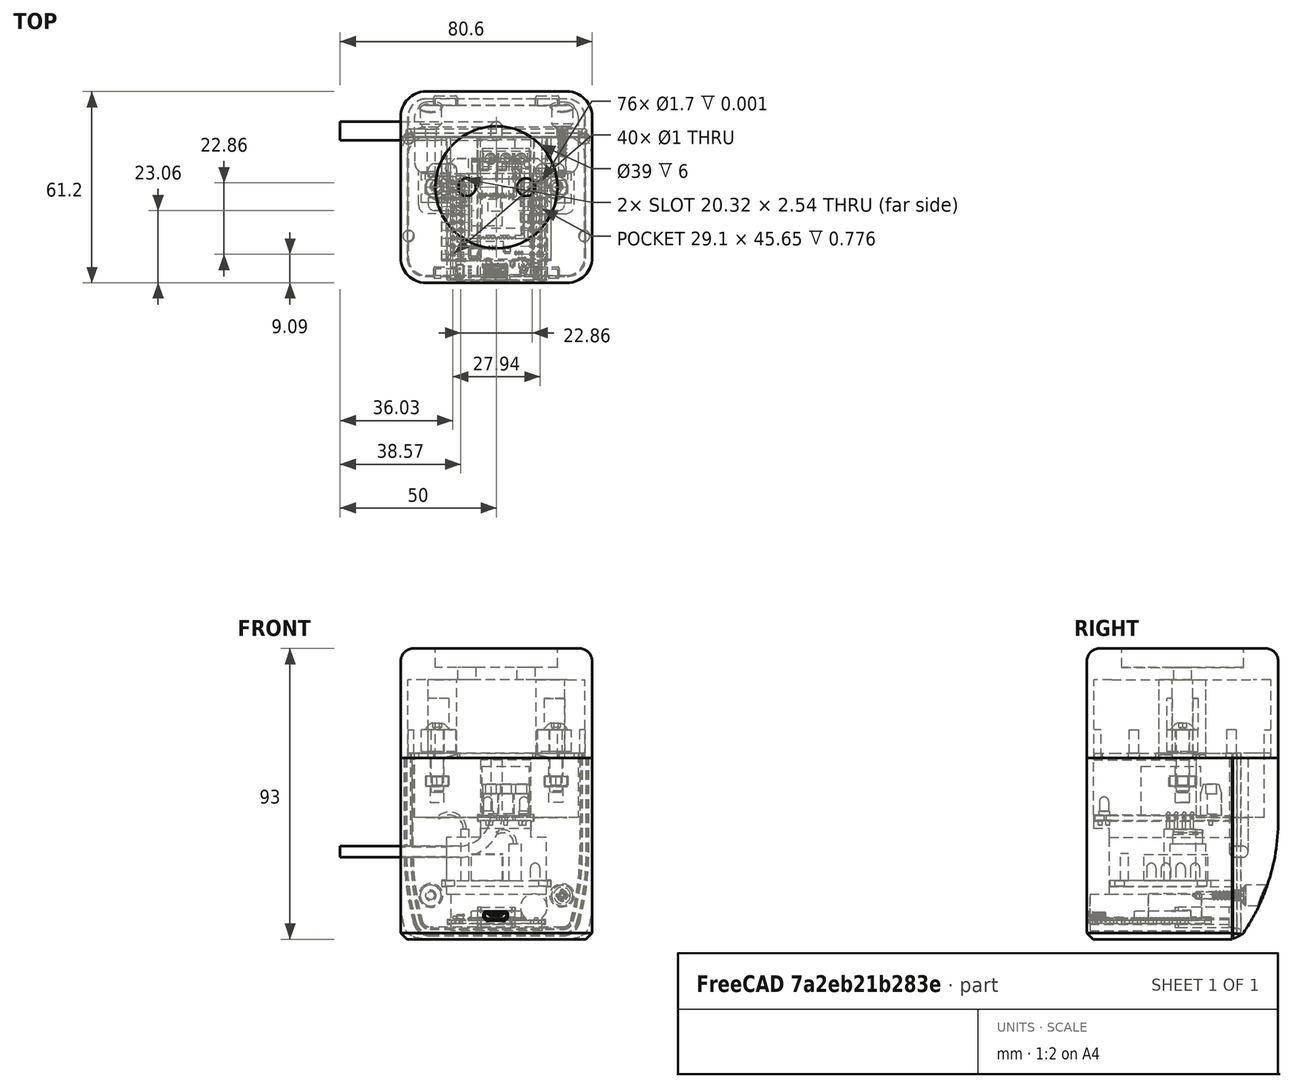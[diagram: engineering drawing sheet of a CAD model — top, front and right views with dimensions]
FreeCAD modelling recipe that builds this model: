
FCSTD DOCUMENT  (FreeCAD 1.0R39109 (Git))
Label: BedroomFan V3
License: All rights reserved
LicenseURL: http://en.wikipedia.org/wiki/All_rights_reserved
objects: Sketcher::SketchObject×80, PartDesign::SubShapeBinder×46, PartDesign::Plane×24, PartDesign::Body×22, PartDesign::Pad×19, PartDesign::Pocket×17, PartDesign::Revolution×11, PartDesign::Mirrored×6, Part::FeaturePython×4, PartDesign::Fillet×3, PartDesign::AdditivePipe×3, PartDesign::Point×3, PartDesign::Chamfer×3, PartDesign::SubtractivePipe×3, Part::Compound×2, PartDesign::Groove×2, PartDesign::LinearPattern×2, Part::MultiCommon×2, Part::Feature×1, PartDesign::MultiTransform×1, +2 more types
note: 470 computed .brp shape members not serialized (recipe doc carries the construction recipe); baked Part::Feature solids carry a one-line shape summary decoded from their .brp

FEATURE [Part::Feature] Part__Feature  label="MH-ET_LIVE_MiniKit"
  shape: bbox 31.02 x 99.68 x 39.44 mm, 5494 faces, 23 solids (baked)
FEATURE [Sketcher::SketchObject] Sketch009
  ArcFitTolerance = 0
  AttachmentSupport = -> [XY_Plane001]
  FullyConstrained = true
  MakeInternals = false
  MapMode = 5
  sketch-geometry (8):
    g0: LineSegment StartX=0 StartY=8.8 StartZ=0 EndX=43.2 EndY=8.8 EndZ=0
    g1: LineSegment StartX=43.2 StartY=8.8 StartZ=0 EndX=43.2 EndY=-8.8 EndZ=0
    g2: LineSegment StartX=43.2 StartY=-8.8 StartZ=0 EndX=0 EndY=-8.8 EndZ=0
    g3: LineSegment StartX=0 StartY=-8.8 StartZ=0 EndX=0 EndY=8.8 EndZ=0
    g4: Circle CenterX=3.2 CenterY=2.54 CenterZ=0 NormalX=0 NormalY=0 NormalZ=1 AngleXU=0 Radius=0.4
    g5: Circle CenterX=3.2 CenterY=0 CenterZ=0 NormalX=0 NormalY=0 NormalZ=1 AngleXU=0 Radius=0.4
    g6: Circle CenterX=3.2 CenterY=-2.54 CenterZ=0 NormalX=0 NormalY=0 NormalZ=1 AngleXU=0 Radius=0.4
    g7: LineSegment [constr] StartX=3.2 StartY=2.54 StartZ=0 EndX=3.2 EndY=-2.54 EndZ=0
  constraints (21):
    c: Coincident(g0,g1)
    c: Coincident(g1,g2)
    c: Coincident(g2,g3)
    c: Coincident(g3,g0)
    c: Horizontal(g0)
    c: Horizontal(g2)
    c: Vertical(g3)
    c: PointOnObject(g0,g-2)
    c: Symmetric(g1,g0,g-1)
    c: DistanceY(g1,g1) = 17.6
    c: DistanceX(g0,g0) = 43.2
    c: PointOnObject(g5,g-1)
    c: Symmetric(g6,g4,g-1)
    c: Coincident(g7,g4)
    c: Coincident(g7,g6)
    c: PointOnObject(g5,g7)
    c: Equal(g6,g5)
    c: Equal(g5,g4)
    c: Radius(g4) = 0.4
    c: DistanceY(g7,g7) = 5.08
    c: DistanceX(g4) = 3.2
FEATURE [PartDesign::Pad] Pad006
  Direction = (0,0,1)
  Length = 1.6
  Length2 = 100
  Profile = -> Sketch009
  Suppressed = false
  Type = 0
FEATURE [PartDesign::Body] Body001  label="PCB"
  AllowCompound = false
  Group = -> [Sketch009,Pad006]
  Origin = -> Origin001
  Tip = -> Pad006
FEATURE [Sketcher::SketchObject] Sketch010
  ArcFitTolerance = 0
  AttachmentOffset = pos=(0,0,1.6) rot=(0,0,1;0rad)
  AttachmentSupport = -> [XY_Plane002]
  FullyConstrained = true
  MakeInternals = false
  MapMode = 5
  Placement = pos=(0,0,1.6) rot=(0,0,1;0rad)
  sketch-geometry (4):
    g0: LineSegment StartX=14.8 StartY=7.6 StartZ=0 EndX=33.8 EndY=7.6 EndZ=0
    g1: LineSegment StartX=33.8 StartY=7.6 StartZ=0 EndX=33.8 EndY=-7.6 EndZ=0
    g2: LineSegment StartX=33.8 StartY=-7.6 StartZ=0 EndX=14.8 EndY=-7.6 EndZ=0
    g3: LineSegment StartX=14.8 StartY=-7.6 StartZ=0 EndX=14.8 EndY=7.6 EndZ=0
  constraints (11):
    c: Coincident(g0,g1)
    c: Coincident(g1,g2)
    c: Coincident(g2,g3)
    c: Coincident(g3,g0)
    c: Horizontal(g0)
    c: Horizontal(g2)
    c: Vertical(g3)
    c: Symmetric(g1,g0,g-1)
    c: DistanceX(g0,g0) = 19
    c: DistanceY(g1,g1) = 15.2
    c: DistanceX(g0) = 14.8
FEATURE [PartDesign::Pad] Pad007
  Direction = (0,0,1)
  Length = 15.7
  Length2 = 100
  Profile = -> Sketch010
  Suppressed = false
  Type = 0
FEATURE [PartDesign::Body] Body002  label="JQC-3FF-S-Z"
  AllowCompound = false
  Group = -> [Sketch010,Pad007]
  Origin = -> Origin002
  Tip = -> Pad007
FEATURE [Sketcher::SketchObject] Sketch011
  ArcFitTolerance = 0
  AttachmentSupport = -> [XZ_Plane003]
  FullyConstrained = true
  MakeInternals = false
  MapMode = 5
  Placement = pos=(0,0,0) rot=(1,0,0;1.5708rad)
  sketch-geometry (7):
    g0: LineSegment StartX=34.6 StartY=11.6 StartZ=0 EndX=39.6 EndY=11.6 EndZ=0
    g1: LineSegment StartX=40.4 StartY=8.6 StartZ=0 EndX=40.4 EndY=1.6 EndZ=0
    g2: LineSegment StartX=40.4 StartY=1.6 StartZ=0 EndX=33.8 EndY=1.6 EndZ=0
    g3: LineSegment StartX=33.8 StartY=1.6 StartZ=0 EndX=33.8 EndY=8.6 EndZ=0
    g4: LineSegment StartX=34.6 StartY=11.6 StartZ=0 EndX=33.8 EndY=8.6 EndZ=0
    g5: LineSegment StartX=39.6 StartY=11.6 StartZ=0 EndX=40.4 EndY=8.6 EndZ=0
    g6: LineSegment [constr] StartX=37.1 StartY=11.6 StartZ=0 EndX=37.1 EndY=1.6 EndZ=0
  constraints (19):
    c: Coincident(g1,g2)
    c: Coincident(g2,g3)
    c: Horizontal(g0)
    c: Vertical(g1)
    c: DistanceY(g1) = 1.6
    c: Coincident(g3,g4)
    c: Coincident(g4,g0)
    c: Coincident(g0,g5)
    c: Coincident(g1,g5)
    c: PointOnObject(g6,g0)
    c: PointOnObject(g6,g2)
    c: Symmetric(g1,g2,g6)
    c: Symmetric(g1,g3,g6)
    c: Symmetric(g0,g0,g6)
    c: DistanceX(g2) = 33.8
    c: DistanceX(g0,g0) = 5
    c: DistanceY(g1,g0) = 10
    c: DistanceY(g1,g1) = 7
    c: DistanceX(g1) = 40.4
FEATURE [PartDesign::Pad] Pad008
  Direction = (0,-1,2e-16)
  Length = 15
  Length2 = 100
  Midplane = true
  Placement = pos=(0,0,0) rot=(1,0,0;1.5708rad)
  Profile = -> Sketch011
  Suppressed = false
  Type = 0
FEATURE [Sketcher::SketchObject] Sketch012
  ArcFitTolerance = 0
  AttachmentOffset = pos=(0,0,36) rot=(0,0,1;0rad)
  AttachmentSupport = -> [YZ_Plane003]
  FullyConstrained = true
  MakeInternals = false
  MapMode = 5
  Placement = pos=(36,0,0) rot=(0.57735,0.57735,0.57735;2.0944rad)
  sketch-geometry (16):
    g0: LineSegment StartX=-7.05 StartY=8.6 StartZ=0 EndX=-2.65 EndY=8.6 EndZ=0
    g1: LineSegment StartX=-2.65 StartY=8.6 StartZ=0 EndX=-2.65 EndY=2.1 EndZ=0
    g2: LineSegment StartX=-2.65 StartY=2.1 StartZ=0 EndX=-7.05 EndY=2.1 EndZ=0
    g3: LineSegment StartX=-7.05 StartY=2.1 StartZ=0 EndX=-7.05 EndY=8.6 EndZ=0
    g4: LineSegment [constr] StartX=-7.05 StartY=8.6 StartZ=0 EndX=-7.5 EndY=8.6 EndZ=0
    g5: LineSegment [constr] StartX=-2.2 StartY=8.6 StartZ=0 EndX=-2.65 EndY=8.6 EndZ=0
    g6: LineSegment StartX=-2.2 StartY=8.6 StartZ=0 EndX=2.2 EndY=8.6 EndZ=0
    g7: LineSegment StartX=2.2 StartY=8.6 StartZ=0 EndX=2.2 EndY=2.1 EndZ=0
    g8: LineSegment StartX=2.2 StartY=2.1 StartZ=0 EndX=-2.2 EndY=2.1 EndZ=0
    g9: LineSegment StartX=-2.2 StartY=2.1 StartZ=0 EndX=-2.2 EndY=8.6 EndZ=0
    g10: LineSegment StartX=2.65 StartY=8.6 StartZ=0 EndX=7.05 EndY=8.6 EndZ=0
    g11: LineSegment StartX=7.05 StartY=8.6 StartZ=0 EndX=7.05 EndY=2.1 EndZ=0
    g12: LineSegment StartX=7.05 StartY=2.1 StartZ=0 EndX=2.65 EndY=2.1 EndZ=0
    g13: LineSegment StartX=2.65 StartY=2.1 StartZ=0 EndX=2.65 EndY=8.6 EndZ=0
    g14: LineSegment [constr] StartX=2.65 StartY=8.6 StartZ=0 EndX=2.2 EndY=8.6 EndZ=0
    g15: LineSegment [constr] StartX=7.05 StartY=8.6 StartZ=0 EndX=7.5 EndY=8.6 EndZ=0
  constraints (45):
    c: Coincident(g0,g1)
    c: Coincident(g1,g2)
    c: Coincident(g2,g3)
    c: Coincident(g3,g0)
    c: Horizontal(g0)
    c: Horizontal(g2)
    c: Vertical(g1)
    c: Vertical(g3)
    c: DistanceX(g0,g0) = 4.4
    c: DistanceY(g0) = 8.6
    c: DistanceY(g3,g3) = 6.5
    c: Coincident(g4,g0)
    c: Horizontal(g4)
    c: Coincident(g5,g0)
    c: Equal(g5,g4)
    c: Horizontal(g5)
    c: Coincident(g6,g7)
    c: Coincident(g7,g8)
    c: Coincident(g8,g9)
    c: Coincident(g9,g6)
    c: Horizontal(g6)
    c: Horizontal(g8)
    c: Vertical(g7)
    c: Vertical(g9)
    c: Coincident(g6,g5)
    c: Coincident(g10,g11)
    c: Coincident(g11,g12)
    c: Coincident(g12,g13)
    c: Coincident(g13,g10)
    c: Horizontal(g10)
    c: Horizontal(g12)
    c: Vertical(g11)
    c: Vertical(g13)
    c: Coincident(g14,g10)
    c: Coincident(g14,g6)
    c: Horizontal(g14)
    c: Coincident(g15,g10)
    c: Equal(g15,g14)
    c: Equal(g14,g5)
    c: DistanceX(g4,g15) = 15
    c: Equal(g0,g6)
    c: Equal(g6,g10)
    c: Symmetric(g4,g15,g-2)
    c: Equal(g1,g9)
    c: Equal(g9,g13)
FEATURE [PartDesign::Pocket] Pocket
  BaseFeature = -> Pad008
  Direction = (-1,0,0)
  Length = 5
  Length2 = 100
  Placement = pos=(0,0,0) rot=(1,0,0;1.5708rad)
  Profile = -> Sketch012
  Reversed = true
  Suppressed = false
  Type = 1
FEATURE [Sketcher::SketchObject] Sketch013
  ArcFitTolerance = 0
  AttachmentOffset = pos=(0,0,8.6) rot=(0,0,1;0rad)
  AttachmentSupport = -> [XY_Plane003]
  ExternalGeometry = -> [Pocket]
  FullyConstrained = true
  MakeInternals = false
  MapMode = 5
  Placement = pos=(0,0,8.6) rot=(0,0,1;0rad)
  sketch-geometry (5):
    g0: Circle CenterX=37.1 CenterY=-4.85 CenterZ=0 NormalX=0 NormalY=0 NormalZ=1 AngleXU=0 Radius=1.75
    g1: LineSegment [constr] StartX=37.1 StartY=-2.65 StartZ=0 EndX=37.1 EndY=-7.05 EndZ=0
    g2: LineSegment [constr] StartX=38.85 StartY=-4.85 StartZ=0 EndX=35.35 EndY=-4.85 EndZ=0
    g3: Circle CenterX=37.1 CenterY=4.85 CenterZ=0 NormalX=0 NormalY=0 NormalZ=1 AngleXU=0 Radius=1.75
    g4: Circle CenterX=37.1 CenterY=0 CenterZ=0 NormalX=0 NormalY=0 NormalZ=1 AngleXU=0 Radius=1.75
  constraints (14):
    c: PointOnObject(g1,g-3)
    c: PointOnObject(g1,g-4)
    c: PointOnObject(g2,g0)
    c: PointOnObject(g2,g0)
    c: PointOnObject(g0,g1)
    c: PointOnObject(g0,g2)
    c: Symmetric(g-3,g-4,g2)
    c: Radius(g0) = 1.75
    c: Symmetric(g-5,g-6,g1)
    c: PointOnObject(g4,g-1)
    c: Symmetric(g3,g0,g-1)
    c: PointOnObject(g4,g1)
    c: Equal(g0,g4)
    c: Equal(g4,g3)
FEATURE [PartDesign::Pocket] Pocket001
  BaseFeature = -> Pocket
  Direction = (0,0,-1)
  Length = 5
  Length2 = 100
  Placement = pos=(0,0,0) rot=(1,0,0;1.5708rad)
  Profile = -> Sketch013
  Reversed = true
  Suppressed = false
  Type = 1
FEATURE [PartDesign::Body] Body003  label="Connectors"
  AllowCompound = false
  Group = -> [Sketch011,Pad008,Sketch012,Pocket,Sketch013,Pocket001]
  Origin = -> Origin003
  Tip = -> Pocket001
FEATURE [Sketcher::SketchObject] Sketch014
  ArcFitTolerance = 0
  AttachmentOffset = pos=(0,0,2.9) rot=(0,0,1;0rad)
  AttachmentSupport = -> [YZ_Plane004]
  FullyConstrained = true
  MakeInternals = false
  MapMode = 5
  Placement = pos=(2.9,0,0) rot=(0.57735,0.57735,0.57735;2.0944rad)
  sketch-geometry (6):
    g0: ArcOfCircle CenterX=0 CenterY=6.05 CenterZ=0 NormalX=0 NormalY=0 NormalZ=1 AngleXU=0 Radius=1.45 StartAngle=1.5708 EndAngle=3.14159
    g1: LineSegment StartX=-1.45 StartY=6.05 StartZ=0 EndX=-1.45 EndY=3 EndZ=0
    g2: LineSegment StartX=-1.45 StartY=3 StartZ=0 EndX=-1.75 EndY=3 EndZ=0
    g3: LineSegment StartX=-1.75 StartY=3 StartZ=0 EndX=-1.75 EndY=1.6 EndZ=0
    g4: LineSegment StartX=-1.75 StartY=1.6 StartZ=0 EndX=0 EndY=1.6 EndZ=0
    g5: LineSegment StartX=0 StartY=1.6 StartZ=0 EndX=0 EndY=7.5 EndZ=0
  constraints (18):
    c: Vertical(g1)
    c: Coincident(g1,g2)
    c: Coincident(g2,g3)
    c: Coincident(g3,g4)
    c: Horizontal(g4)
    c: Coincident(g4,g5)
    c: Coincident(g5,g0)
    c: Vertical(g5)
    c: Tangent(g0,g1) = -1.5708
    c: PointOnObject(g0,g5)
    c: Horizontal(g2)
    c: Vertical(g3)
    c: DistanceY(g3) = 1.6
    c: DistanceY(g0) = 7.5
    c: DistanceX(g0,g0) = 1.45
    c: DistanceX(g4,g4) = 1.75
    c: DistanceY(g2) = 3
    c: PointOnObject(g4,g-2)
FEATURE [PartDesign::Revolution] Revolution001
  Angle = 360
  Angle2 = 60
  Axis = (0,0,1)
  Base = (2.9,0,0)
  Placement = pos=(0,0,0) rot=(0.57735,0.57735,0.57735;2.0944rad)
  Profile = -> Sketch014
  ReferenceAxis = -> Sketch014 [V_Axis]
  Suppressed = false
  Type = 0
FEATURE [PartDesign::Body] Body004  label="LEDgreen"
  AllowCompound = false
  Group = -> [Sketch014,Revolution001]
  Origin = -> Origin004
  Placement = pos=(0,5.8,0) rot=(0,0,1;0rad)
  Tip = -> Revolution001
FEATURE [Sketcher::SketchObject] Sketch015
  ArcFitTolerance = 0
  AttachmentOffset = pos=(0,0,2.9) rot=(0,0,1;0rad)
  AttachmentSupport = -> [YZ_Plane004]
  FullyConstrained = true
  MakeInternals = false
  MapMode = 5
  Placement = pos=(2.9,0,0) rot=(0.57735,0.57735,0.57735;2.0944rad)
  sketch-geometry (6):
    g0: ArcOfCircle CenterX=0 CenterY=6.05 CenterZ=0 NormalX=0 NormalY=0 NormalZ=1 AngleXU=0 Radius=1.45 StartAngle=1.5708 EndAngle=3.14159
    g1: LineSegment StartX=-1.45 StartY=6.05 StartZ=0 EndX=-1.45 EndY=3 EndZ=0
    g2: LineSegment StartX=-1.45 StartY=3 StartZ=0 EndX=-1.75 EndY=3 EndZ=0
    g3: LineSegment StartX=-1.75 StartY=3 StartZ=0 EndX=-1.75 EndY=1.6 EndZ=0
    g4: LineSegment StartX=-1.75 StartY=1.6 StartZ=0 EndX=0 EndY=1.6 EndZ=0
    g5: LineSegment StartX=1e-16 StartY=1.6 StartZ=0 EndX=1e-16 EndY=7.5 EndZ=0
  constraints (18):
    c: Vertical(g1)
    c: Coincident(g1,g2)
    c: Coincident(g2,g3)
    c: Coincident(g3,g4)
    c: Horizontal(g4)
    c: Coincident(g4,g5)
    c: Coincident(g5,g0)
    c: Vertical(g5)
    c: Tangent(g0,g1) = -1.5708
    c: PointOnObject(g0,g5)
    c: Horizontal(g2)
    c: Vertical(g3)
    c: DistanceY(g3) = 1.6
    c: DistanceY(g0) = 7.5
    c: DistanceX(g0,g0) = 1.45
    c: DistanceX(g4,g4) = 1.75
    c: DistanceY(g2) = 3
    c: PointOnObject(g4,g-2)
FEATURE [PartDesign::Revolution] Revolution002
  Angle = 360
  Angle2 = 60
  Axis = (0,0,1)
  Base = (2.9,0,0)
  Placement = pos=(0,0,0) rot=(0.57735,0.57735,0.57735;2.0944rad)
  Profile = -> Sketch015
  ReferenceAxis = -> Sketch015 [V_Axis]
  Suppressed = false
  Type = 0
FEATURE [PartDesign::Body] Body005  label="LEDred"
  AllowCompound = false
  Group = -> [Sketch015,Revolution002]
  Origin = -> Origin005
  Placement = pos=(0,-5.8,0) rot=(0,0,1;0rad)
  Tip = -> Revolution002
FEATURE [Sketcher::SketchObject] Sketch016
  ArcFitTolerance = 0
  AttachmentSupport = -> [YZ_Plane006]
  FullyConstrained = true
  MakeInternals = false
  MapMode = 5
  Placement = pos=(0,0,0) rot=(0.57735,0.57735,0.57735;2.0944rad)
  sketch-geometry (5):
    g0: LineSegment StartX=1.2 StartY=0 StartZ=0 EndX=0 EndY=0 EndZ=0
    g1: LineSegment StartX=0 StartY=0 StartZ=0 EndX=0 EndY=-1.5 EndZ=0
    g2: LineSegment StartX=0 StartY=-1.5 StartZ=0 EndX=0.6 EndY=-1.5 EndZ=0
    g3: LineSegment StartX=0.6 StartY=-1.5 StartZ=0 EndX=0.6 EndY=-0.6 EndZ=0
    g4: ArcOfCircle CenterX=1.2 CenterY=-0.6 CenterZ=0 NormalX=0 NormalY=0 NormalZ=1 AngleXU=0 Radius=0.6 StartAngle=1.5708 EndAngle=3.14159
  constraints (13):
    c: PointOnObject(g0,g-1)
    c: Coincident(g0,g-1)
    c: Coincident(g0,g1)
    c: PointOnObject(g1,g-2)
    c: Coincident(g1,g2)
    c: Horizontal(g2)
    c: Coincident(g2,g3)
    c: Vertical(g3)
    c: Tangent(g0,g4) = -1.5708
    c: Tangent(g3,g4) = 1.5708
    c: DistanceX(g2,g2) = 0.6
    c: DistanceY(g1,g1) = 1.5
    c: Radius(g4) = 0.6
FEATURE [PartDesign::Revolution] Revolution003
  Angle = 360
  Angle2 = 60
  Axis = (0,0,1)
  Base = (0,0,0)
  Placement = pos=(0,0,0) rot=(0.57735,0.57735,0.57735;2.0944rad)
  Profile = -> Sketch016
  ReferenceAxis = -> Sketch016 [V_Axis]
  Reversed = true
  Suppressed = false
  Type = 0
FEATURE [PartDesign::Body] Body006  label="Pin001"
  AllowCompound = false
  Group = -> [Sketch016,Revolution003]
  Origin = -> Origin006
  Placement = pos=(1.7,5.7,0) rot=(0,0,1;0rad)
  Tip = -> Revolution003
FEATURE [Sketcher::SketchObject] Sketch017
  ArcFitTolerance = 0
  AttachmentSupport = -> [YZ_Plane006]
  FullyConstrained = true
  MakeInternals = false
  MapMode = 5
  Placement = pos=(0,0,0) rot=(0.57735,0.57735,0.57735;2.0944rad)
  sketch-geometry (5):
    g0: LineSegment StartX=1.2 StartY=0 StartZ=0 EndX=0 EndY=0 EndZ=0
    g1: LineSegment StartX=0 StartY=0 StartZ=0 EndX=0 EndY=-1.5 EndZ=0
    g2: LineSegment StartX=0 StartY=-1.5 StartZ=0 EndX=0.6 EndY=-1.5 EndZ=0
    g3: LineSegment StartX=0.6 StartY=-1.5 StartZ=0 EndX=0.6 EndY=-0.6 EndZ=0
    g4: ArcOfCircle CenterX=1.2 CenterY=-0.6 CenterZ=0 NormalX=0 NormalY=0 NormalZ=1 AngleXU=0 Radius=0.6 StartAngle=1.5708 EndAngle=3.14159
  constraints (13):
    c: PointOnObject(g0,g-1)
    c: Coincident(g0,g-1)
    c: Coincident(g0,g1)
    c: PointOnObject(g1,g-2)
    c: Coincident(g1,g2)
    c: Horizontal(g2)
    c: Coincident(g2,g3)
    c: Vertical(g3)
    c: Tangent(g0,g4) = -1.5708
    c: Tangent(g3,g4) = 1.5708
    c: DistanceX(g2,g2) = 0.6
    c: DistanceY(g1,g1) = 1.5
    c: Radius(g4) = 0.6
FEATURE [PartDesign::Revolution] Revolution004
  Angle = 360
  Angle2 = 60
  Axis = (0,0,1)
  Base = (0,0,0)
  Placement = pos=(0,0,0) rot=(0.57735,0.57735,0.57735;2.0944rad)
  Profile = -> Sketch017
  ReferenceAxis = -> Sketch017 [V_Axis]
  Reversed = true
  Suppressed = false
  Type = 0
FEATURE [PartDesign::Body] Body007  label="Pin002"
  AllowCompound = false
  Group = -> [Sketch017,Revolution004]
  Origin = -> Origin007
  Placement = pos=(4.1,5.7,0) rot=(0,0,1;0rad)
  Tip = -> Revolution004
FEATURE [Sketcher::SketchObject] Sketch018
  ArcFitTolerance = 0
  AttachmentSupport = -> [YZ_Plane006]
  FullyConstrained = true
  MakeInternals = false
  MapMode = 5
  Placement = pos=(0,0,0) rot=(0.57735,0.57735,0.57735;2.0944rad)
  sketch-geometry (5):
    g0: LineSegment StartX=1.2 StartY=0 StartZ=0 EndX=0 EndY=0 EndZ=0
    g1: LineSegment StartX=0 StartY=0 StartZ=0 EndX=0 EndY=-1.5 EndZ=0
    g2: LineSegment StartX=0 StartY=-1.5 StartZ=0 EndX=0.6 EndY=-1.5 EndZ=0
    g3: LineSegment StartX=0.6 StartY=-1.5 StartZ=0 EndX=0.6 EndY=-0.6 EndZ=0
    g4: ArcOfCircle CenterX=1.2 CenterY=-0.6 CenterZ=0 NormalX=0 NormalY=0 NormalZ=1 AngleXU=0 Radius=0.6 StartAngle=1.5708 EndAngle=3.14159
  constraints (13):
    c: PointOnObject(g0,g-1)
    c: Coincident(g0,g-1)
    c: Coincident(g0,g1)
    c: PointOnObject(g1,g-2)
    c: Coincident(g1,g2)
    c: Horizontal(g2)
    c: Coincident(g2,g3)
    c: Vertical(g3)
    c: Tangent(g0,g4) = -1.5708
    c: Tangent(g3,g4) = 1.5708
    c: DistanceX(g2,g2) = 0.6
    c: DistanceY(g1,g1) = 1.5
    c: Radius(g4) = 0.6
FEATURE [PartDesign::Revolution] Revolution005
  Angle = 360
  Angle2 = 60
  Axis = (0,0,1)
  Base = (0,0,0)
  Placement = pos=(0,0,0) rot=(0.57735,0.57735,0.57735;2.0944rad)
  Profile = -> Sketch018
  ReferenceAxis = -> Sketch018 [V_Axis]
  Reversed = true
  Suppressed = false
  Type = 0
FEATURE [PartDesign::Body] Body008  label="Pin003"
  AllowCompound = false
  Group = -> [Sketch018,Revolution005]
  Origin = -> Origin008
  Placement = pos=(4.1,-5.9,0) rot=(0,0,1;0rad)
  Tip = -> Revolution005
FEATURE [Sketcher::SketchObject] Sketch019
  ArcFitTolerance = 0
  AttachmentSupport = -> [YZ_Plane006]
  FullyConstrained = true
  MakeInternals = false
  MapMode = 5
  Placement = pos=(0,0,0) rot=(0.57735,0.57735,0.57735;2.0944rad)
  sketch-geometry (5):
    g0: LineSegment StartX=1.2 StartY=0 StartZ=0 EndX=0 EndY=0 EndZ=0
    g1: LineSegment StartX=0 StartY=0 StartZ=0 EndX=0 EndY=-1.5 EndZ=0
    g2: LineSegment StartX=0 StartY=-1.5 StartZ=0 EndX=0.6 EndY=-1.5 EndZ=0
    g3: LineSegment StartX=0.6 StartY=-1.5 StartZ=0 EndX=0.6 EndY=-0.6 EndZ=0
    g4: ArcOfCircle CenterX=1.2 CenterY=-0.6 CenterZ=0 NormalX=0 NormalY=0 NormalZ=1 AngleXU=0 Radius=0.6 StartAngle=1.5708 EndAngle=3.14159
  constraints (13):
    c: PointOnObject(g0,g-1)
    c: Coincident(g0,g-1)
    c: Coincident(g0,g1)
    c: PointOnObject(g1,g-2)
    c: Coincident(g1,g2)
    c: Horizontal(g2)
    c: Coincident(g2,g3)
    c: Vertical(g3)
    c: Tangent(g0,g4) = -1.5708
    c: Tangent(g3,g4) = 1.5708
    c: DistanceX(g2,g2) = 0.6
    c: DistanceY(g1,g1) = 1.5
    c: Radius(g4) = 0.6
FEATURE [PartDesign::Revolution] Revolution006
  Angle = 360
  Angle2 = 60
  Axis = (0,0,1)
  Base = (0,0,0)
  Placement = pos=(0,0,0) rot=(0.57735,0.57735,0.57735;2.0944rad)
  Profile = -> Sketch019
  ReferenceAxis = -> Sketch019 [V_Axis]
  Reversed = true
  Suppressed = false
  Type = 0
FEATURE [PartDesign::Body] Body009  label="Pin004"
  AllowCompound = false
  Group = -> [Sketch019,Revolution006]
  Origin = -> Origin009
  Placement = pos=(1.7,-5.9,0) rot=(0,0,1;0rad)
  Tip = -> Revolution006
FEATURE [Sketcher::SketchObject] Sketch020
  ArcFitTolerance = 0
  AttachmentSupport = -> [YZ_Plane006]
  FullyConstrained = true
  MakeInternals = false
  MapMode = 5
  Placement = pos=(0,0,0) rot=(0.57735,0.57735,0.57735;2.0944rad)
  sketch-geometry (5):
    g0: LineSegment StartX=1.2 StartY=0 StartZ=0 EndX=0 EndY=0 EndZ=0
    g1: LineSegment StartX=0 StartY=0 StartZ=0 EndX=0 EndY=-1.5 EndZ=0
    g2: LineSegment StartX=0 StartY=-1.5 StartZ=0 EndX=0.6 EndY=-1.5 EndZ=0
    g3: LineSegment StartX=0.6 StartY=-1.5 StartZ=0 EndX=0.6 EndY=-0.6 EndZ=0
    g4: ArcOfCircle CenterX=1.2 CenterY=-0.6 CenterZ=0 NormalX=0 NormalY=0 NormalZ=1 AngleXU=0 Radius=0.6 StartAngle=1.5708 EndAngle=3.14159
  constraints (13):
    c: PointOnObject(g0,g-1)
    c: Coincident(g0,g-1)
    c: Coincident(g0,g1)
    c: PointOnObject(g1,g-2)
    c: Coincident(g1,g2)
    c: Horizontal(g2)
    c: Coincident(g2,g3)
    c: Vertical(g3)
    c: Tangent(g0,g4) = -1.5708
    c: Tangent(g3,g4) = 1.5708
    c: DistanceX(g2,g2) = 0.6
    c: DistanceY(g1,g1) = 1.5
    c: Radius(g4) = 0.6
FEATURE [PartDesign::Revolution] Revolution007
  Angle = 360
  Angle2 = 60
  Axis = (0,0,1)
  Base = (0,0,0)
  Placement = pos=(0,0,0) rot=(0.57735,0.57735,0.57735;2.0944rad)
  Profile = -> Sketch020
  ReferenceAxis = -> Sketch020 [V_Axis]
  Reversed = true
  Suppressed = false
  Type = 0
FEATURE [PartDesign::Body] Body010  label="Pin005"
  AllowCompound = false
  Group = -> [Sketch020,Revolution007]
  Origin = -> Origin010
  Placement = pos=(37.1,-4.8,0) rot=(0,0,1;0rad)
  Tip = -> Revolution007
FEATURE [Sketcher::SketchObject] Sketch021
  ArcFitTolerance = 0
  AttachmentSupport = -> [YZ_Plane006]
  FullyConstrained = true
  MakeInternals = false
  MapMode = 5
  Placement = pos=(0,0,0) rot=(0.57735,0.57735,0.57735;2.0944rad)
  sketch-geometry (5):
    g0: LineSegment StartX=1.2 StartY=0 StartZ=0 EndX=0 EndY=0 EndZ=0
    g1: LineSegment StartX=0 StartY=0 StartZ=0 EndX=0 EndY=-1.5 EndZ=0
    g2: LineSegment StartX=0 StartY=-1.5 StartZ=0 EndX=0.6 EndY=-1.5 EndZ=0
    g3: LineSegment StartX=0.6 StartY=-1.5 StartZ=0 EndX=0.6 EndY=-0.6 EndZ=0
    g4: ArcOfCircle CenterX=1.2 CenterY=-0.6 CenterZ=0 NormalX=0 NormalY=0 NormalZ=1 AngleXU=0 Radius=0.6 StartAngle=1.5708 EndAngle=3.14159
  constraints (13):
    c: PointOnObject(g0,g-1)
    c: Coincident(g0,g-1)
    c: Coincident(g0,g1)
    c: PointOnObject(g1,g-2)
    c: Coincident(g1,g2)
    c: Horizontal(g2)
    c: Coincident(g2,g3)
    c: Vertical(g3)
    c: Tangent(g0,g4) = -1.5708
    c: Tangent(g3,g4) = 1.5708
    c: DistanceX(g2,g2) = 0.6
    c: DistanceY(g1,g1) = 1.5
    c: Radius(g4) = 0.6
FEATURE [PartDesign::Revolution] Revolution008
  Angle = 360
  Angle2 = 60
  Axis = (0,0,1)
  Base = (0,0,0)
  Placement = pos=(0,0,0) rot=(0.57735,0.57735,0.57735;2.0944rad)
  Profile = -> Sketch021
  ReferenceAxis = -> Sketch021 [V_Axis]
  Reversed = true
  Suppressed = false
  Type = 0
FEATURE [PartDesign::Body] Body011  label="Pin006"
  AllowCompound = false
  Group = -> [Sketch021,Revolution008]
  Origin = -> Origin011
  Placement = pos=(37.1,9e-16,0) rot=(0,0,1;0rad)
  Tip = -> Revolution008
FEATURE [Sketcher::SketchObject] Sketch022
  ArcFitTolerance = 0
  AttachmentSupport = -> [YZ_Plane006]
  FullyConstrained = true
  MakeInternals = false
  MapMode = 5
  Placement = pos=(0,0,0) rot=(0.57735,0.57735,0.57735;2.0944rad)
  sketch-geometry (5):
    g0: LineSegment StartX=1.2 StartY=0 StartZ=0 EndX=0 EndY=0 EndZ=0
    g1: LineSegment StartX=0 StartY=0 StartZ=0 EndX=0 EndY=-1.5 EndZ=0
    g2: LineSegment StartX=0 StartY=-1.5 StartZ=0 EndX=0.6 EndY=-1.5 EndZ=0
    g3: LineSegment StartX=0.6 StartY=-1.5 StartZ=0 EndX=0.6 EndY=-0.6 EndZ=0
    g4: ArcOfCircle CenterX=1.2 CenterY=-0.6 CenterZ=0 NormalX=0 NormalY=0 NormalZ=1 AngleXU=0 Radius=0.6 StartAngle=1.5708 EndAngle=3.14159
  constraints (13):
    c: PointOnObject(g0,g-1)
    c: Coincident(g0,g-1)
    c: Coincident(g0,g1)
    c: PointOnObject(g1,g-2)
    c: Coincident(g1,g2)
    c: Horizontal(g2)
    c: Coincident(g2,g3)
    c: Vertical(g3)
    c: Tangent(g0,g4) = -1.5708
    c: Tangent(g3,g4) = 1.5708
    c: DistanceX(g2,g2) = 0.6
    c: DistanceY(g1,g1) = 1.5
    c: Radius(g4) = 0.6
FEATURE [PartDesign::Revolution] Revolution009
  Angle = 360
  Angle2 = 60
  Axis = (0,0,1)
  Base = (0,0,0)
  Placement = pos=(0,0,0) rot=(0.57735,0.57735,0.57735;2.0944rad)
  Profile = -> Sketch022
  ReferenceAxis = -> Sketch022 [V_Axis]
  Reversed = true
  Suppressed = false
  Type = 0
FEATURE [PartDesign::Body] Body012  label="Pin007"
  AllowCompound = false
  Group = -> [Sketch022,Revolution009]
  Origin = -> Origin012
  Placement = pos=(37.1,4.8,0) rot=(0,0,1;0rad)
  Tip = -> Revolution009
FEATURE [Part::Compound] Compound  label="Relay JQC-3FF-S-Z"
  Links = -> [Body001,Body002,Body003,Body004,Body005,Body006,Body007,Body008,Body009,Body010,Body011,Body012]
  Placement = pos=(3,-28,-20) rot=(0,0,1;1.5708rad)
FEATURE [Sketcher::SketchObject] Sketch023
  ArcFitTolerance = 0
  AttachmentSupport = -> [XY_Plane013]
  FullyConstrained = true
  MakeInternals = false
  MapMode = 5
  sketch-geometry (12):
    g0: LineSegment StartX=-22.6 StartY=30.6 StartZ=0 EndX=22.6 EndY=30.6 EndZ=0
    g1: LineSegment StartX=30.6 StartY=22.6 StartZ=0 EndX=30.6 EndY=-22.6 EndZ=0
    g2: LineSegment StartX=22.6 StartY=-30.6 StartZ=0 EndX=-22.6 EndY=-30.6 EndZ=0
    g3: LineSegment StartX=-30.6 StartY=-22.6 StartZ=0 EndX=-30.6 EndY=22.6 EndZ=0
    g4: ArcOfCircle CenterX=-22.6 CenterY=22.6 CenterZ=0 NormalX=0 NormalY=0 NormalZ=1 AngleXU=0 Radius=8 StartAngle=1.5708 EndAngle=3.14159
    g5: ArcOfCircle CenterX=22.6 CenterY=22.6 CenterZ=0 NormalX=0 NormalY=0 NormalZ=1 AngleXU=0 Radius=8 StartAngle=2.39e-14 EndAngle=1.5708
    g6: ArcOfCircle CenterX=22.6 CenterY=-22.6 CenterZ=0 NormalX=0 NormalY=0 NormalZ=1 AngleXU=0 Radius=8 StartAngle=4.71239 EndAngle=6.28319
    g7: ArcOfCircle CenterX=-22.6 CenterY=-22.6 CenterZ=0 NormalX=0 NormalY=0 NormalZ=1 AngleXU=0 Radius=8 StartAngle=3.14159 EndAngle=4.71239
    g8: LineSegment [constr] StartX=-22.6 StartY=22.6 StartZ=0 EndX=22.6 EndY=22.6 EndZ=0
    g9: LineSegment [constr] StartX=22.6 StartY=22.6 StartZ=0 EndX=22.6 EndY=-22.6 EndZ=0
    g10: LineSegment [constr] StartX=22.6 StartY=-22.6 StartZ=0 EndX=-22.6 EndY=-22.6 EndZ=0
    g11: LineSegment [constr] StartX=-22.6 StartY=-22.6 StartZ=0 EndX=-22.6 EndY=22.6 EndZ=0
  constraints (26):
    c: Horizontal(g0)
    c: Horizontal(g2)
    c: Vertical(g1)
    c: Vertical(g3)
    c: Tangent(g3,g4) = 1.5708
    c: Tangent(g0,g4) = 1.5708
    c: Tangent(g0,g5) = 1.5708
    c: Tangent(g1,g5) = 1.5708
    c: Tangent(g1,g6) = 1.5708
    c: Tangent(g2,g6) = 1.5708
    c: Tangent(g2,g7) = 1.5708
    c: Tangent(g3,g7) = 1.5708
    c: Coincident(g8,g9)
    c: Coincident(g9,g10)
    c: Coincident(g10,g11)
    c: Coincident(g11,g8)
    c: Horizontal(g10)
    c: Coincident(g8,g4)
    c: Coincident(g9,g6)
    c: Coincident(g5,g8)
    c: Coincident(g7,g10)
    c: Symmetric(g5,g6,g-1)
    c: Symmetric(g5,g4,g-2)
    c: Equal(g9,g8)
    c: DistanceX(g3,g1) = 61.2
    c: Radius(g5) = 8
FEATURE [PartDesign::Pad] Pad009
  Direction = (0,0,1)
  Length = 35
  Length2 = 100
  Profile = -> Sketch023
  Suppressed = false
  Type = 0
FEATURE [Sketcher::SketchObject] Sketch024
  ArcFitTolerance = 0
  AttachmentSupport = -> [XY_Plane013]
  ExternalGeometry = -> [Sketch023]
  FullyConstrained = true
  MakeInternals = false
  MapMode = 5
  sketch-geometry (12):
    g0: LineSegment [constr] StartX=22.6 StartY=22.6 StartZ=0 EndX=-22.6 EndY=22.6 EndZ=0
    g1: LineSegment [constr] StartX=-22.6 StartY=22.6 StartZ=0 EndX=-22.6 EndY=-22.6 EndZ=0
    g2: LineSegment [constr] StartX=-22.6 StartY=-22.6 StartZ=0 EndX=22.6 EndY=-22.6 EndZ=0
    g3: LineSegment [constr] StartX=22.6 StartY=-22.6 StartZ=0 EndX=22.6 EndY=22.6 EndZ=0
    g4: LineSegment StartX=-22.6 StartY=28.3 StartZ=0 EndX=22.6 EndY=28.3 EndZ=0
    g5: LineSegment StartX=28.3 StartY=22.6 StartZ=0 EndX=28.3 EndY=-22.6 EndZ=0
    g6: LineSegment StartX=22.6 StartY=-28.3 StartZ=0 EndX=-22.6 EndY=-28.3 EndZ=0
    g7: LineSegment StartX=-28.3 StartY=-22.6 StartZ=0 EndX=-28.3 EndY=22.6 EndZ=0
    g8: ArcOfCircle CenterX=22.6 CenterY=22.6 CenterZ=0 NormalX=0 NormalY=0 NormalZ=1 AngleXU=0 Radius=5.7 StartAngle=0 EndAngle=1.5708
    g9: ArcOfCircle CenterX=-22.6 CenterY=22.6 CenterZ=0 NormalX=0 NormalY=0 NormalZ=1 AngleXU=0 Radius=5.7 StartAngle=1.5708 EndAngle=3.14159
    g10: ArcOfCircle CenterX=-22.6 CenterY=-22.6 CenterZ=0 NormalX=0 NormalY=0 NormalZ=1 AngleXU=0 Radius=5.7 StartAngle=3.14159 EndAngle=4.71239
    g11: ArcOfCircle CenterX=22.6 CenterY=-22.6 CenterZ=0 NormalX=0 NormalY=0 NormalZ=1 AngleXU=0 Radius=5.7 StartAngle=4.71239 EndAngle=6.28319
  constraints (25):
    c: Coincident(g0,g1)
    c: Coincident(g1,g2)
    c: Coincident(g2,g3)
    c: Coincident(g3,g0)
    c: Horizontal(g2)
    c: Vertical(g1)
    c: Coincident(g0,g-3)
    c: Symmetric(g0,g2,g-1)
    c: Symmetric(g0,g0,g-2)
    c: Horizontal(g4)
    c: Horizontal(g6)
    c: Vertical(g5)
    c: Tangent(g5,g8) = 1.5708
    c: Tangent(g4,g8) = 1.5708
    c: Tangent(g4,g9) = 1.5708
    c: Tangent(g7,g9) = 1.5708
    c: Tangent(g7,g10) = 1.5708
    c: Tangent(g6,g10) = 1.5708
    c: Tangent(g6,g11) = 1.5708
    c: Tangent(g5,g11) = 1.5708
    c: Coincident(g0,g8)
    c: Coincident(g0,g9)
    c: Coincident(g1,g10)
    c: Coincident(g2,g11)
    c: DistanceX(g5,g-3) = 2.3
FEATURE [PartDesign::Pocket] Pocket002
  BaseFeature = -> Pad009
  Direction = (0,0,-1)
  Length = 25
  Length2 = 100
  Profile = -> Sketch024
  Reversed = true
  Suppressed = false
  Type = 0
FEATURE [Sketcher::SketchObject] Sketch025
  ArcFitTolerance = 0
  AttachmentSupport = -> [XY_Plane013]
  FullyConstrained = true
  MakeInternals = false
  MapMode = 5
  sketch-geometry (4):
    g0: LineSegment StartX=19.5 StartY=28.6 StartZ=0 EndX=13.1 EndY=28.6 EndZ=0
    g1: LineSegment StartX=13.1 StartY=28.6 StartZ=0 EndX=13.1 EndY=26.1 EndZ=0
    g2: LineSegment StartX=13.1 StartY=26.1 StartZ=0 EndX=19.5 EndY=26.1 EndZ=0
    g3: LineSegment StartX=19.5 StartY=26.1 StartZ=0 EndX=19.5 EndY=28.6 EndZ=0
  constraints (12):
    c: Coincident(g0,g1)
    c: Coincident(g1,g2)
    c: Coincident(g2,g3)
    c: Coincident(g3,g0)
    c: Horizontal(g0)
    c: Horizontal(g2)
    c: Vertical(g1)
    c: Vertical(g3)
    c: DistanceX(g2) = 19.5
    c: DistanceX(g2,g2) = 6.4
    c: DistanceY(g2) = 26.1
    c: DistanceY(g3,g3) = 2.5
FEATURE [PartDesign::Pad] Pad010
  BaseFeature = -> Pocket002
  Direction = (0,0,1)
  Length = 9
  Length2 = 100
  Profile = -> Sketch025
  Suppressed = false
  Type = 0
FEATURE [Sketcher::SketchObject] Sketch026
  ArcFitTolerance = 0
  AttachmentSupport = -> [XY_Plane013]
  FullyConstrained = true
  MakeInternals = false
  MapMode = 5
  sketch-geometry (2):
    g0: Circle CenterX=28.1 CenterY=15.6 CenterZ=0 NormalX=0 NormalY=0 NormalZ=1 AngleXU=0 Radius=1.55
    g1: LineSegment [constr] StartX=28.1 StartY=15.6 StartZ=0 EndX=26.55 EndY=15.6 EndZ=0
  constraints (6):
    c: Radius(g0) = 1.55
    c: Coincident(g1,g0)
    c: PointOnObject(g1,g0)
    c: Horizontal(g1)
    c: DistanceX(g1) = 26.55
    c: DistanceY(g0) = 15.6
FEATURE [PartDesign::Pad] Pad011
  BaseFeature = -> Pad010
  Direction = (0,0,1)
  Length = 9
  Length2 = 100
  Profile = -> Sketch026
  Suppressed = false
  Type = 0
FEATURE [Sketcher::SketchObject] Sketch027
  ArcFitTolerance = 0
  AttachmentSupport = -> [XY_Plane013]
  FullyConstrained = true
  MakeInternals = false
  MapMode = 5
  sketch-geometry (6):
    g0: LineSegment StartX=21.8 StartY=3.3 StartZ=0 EndX=12.7 EndY=3.3 EndZ=0
    g1: LineSegment StartX=12.7 StartY=3.3 StartZ=0 EndX=12.7 EndY=5.5 EndZ=0
    g2: LineSegment StartX=14.7 StartY=7.5 StartZ=0 EndX=19.8 EndY=7.5 EndZ=0
    g3: LineSegment StartX=21.8 StartY=5.5 StartZ=0 EndX=21.8 EndY=3.3 EndZ=0
    g4: ArcOfCircle CenterX=19.8 CenterY=5.5 CenterZ=0 NormalX=0 NormalY=0 NormalZ=1 AngleXU=0 Radius=2 StartAngle=6.77e-14 EndAngle=1.5708
    g5: ArcOfCircle CenterX=14.7 CenterY=5.5 CenterZ=0 NormalX=0 NormalY=0 NormalZ=1 AngleXU=0 Radius=2 StartAngle=1.5708 EndAngle=3.14159
  constraints (16):
    c: Coincident(g0,g1)
    c: Coincident(g3,g0)
    c: Horizontal(g0)
    c: Horizontal(g2)
    c: Vertical(g1)
    c: Vertical(g3)
    c: Tangent(g3,g4) = 1.5708
    c: Tangent(g2,g4) = 1.5708
    c: Tangent(g2,g5) = 1.5708
    c: Tangent(g1,g5) = 1.5708
    c: DistanceX(g0,g0) = 9.1
    c: DistanceY(g0,g2) = 4.2
    c: DistanceY(g0) = 3.3
    c: DistanceX(g3) = 21.8
    c: Equal(g5,g4)
    c: Radius(g4) = 2
FEATURE [PartDesign::Pad] Pad012
  BaseFeature = -> Pad011
  Direction = (0,0,1)
  Length = 33
  Length2 = 100
  Profile = -> Sketch027
  Suppressed = false
  Type = 0
FEATURE [PartDesign::Mirrored] Mirrored
  MirrorPlane = -> YZ_Plane014
  Suppressed = false
  TransformMode = 0
FEATURE [PartDesign::Mirrored] Mirrored001
  MirrorPlane = -> XZ_Plane013
  Suppressed = false
  TransformMode = 0
FEATURE [PartDesign::MultiTransform] MultiTransform
  BaseFeature = -> Pad012
  Originals = -> [Pad010,Pad012,Pad011]
  Suppressed = false
  TransformMode = 0
  Transformations = -> [Mirrored,Mirrored001]
FEATURE [Sketcher::SketchObject] Sketch028
  ArcFitTolerance = 0
  AttachmentSupport = -> [XZ_Plane013]
  FullyConstrained = true
  MakeInternals = false
  MapMode = 5
  Placement = pos=(0,0,0) rot=(1,0,0;1.5708rad)
  sketch-geometry (4):
    g0: LineSegment StartX=-12.75 StartY=1 StartZ=0 EndX=12.75 EndY=1 EndZ=0
    g1: LineSegment StartX=12.75 StartY=1 StartZ=0 EndX=17.5 EndY=0 EndZ=0
    g2: LineSegment StartX=17.5 StartY=0 StartZ=0 EndX=-17.5 EndY=0 EndZ=0
    g3: LineSegment StartX=-17.5 StartY=0 StartZ=0 EndX=-12.75 EndY=1 EndZ=0
  constraints (10):
    c: Coincident(g0,g1)
    c: Coincident(g1,g2)
    c: Coincident(g2,g3)
    c: Coincident(g3,g0)
    c: PointOnObject(g1,g-1)
    c: Symmetric(g0,g0,g-2)
    c: Symmetric(g1,g2,g-2)
    c: DistanceX(g2,g2) = 35
    c: DistanceX(g0,g0) = 25.5
    c: DistanceY(g1,g1) = 1
FEATURE [PartDesign::Pocket] Pocket003
  BaseFeature = -> MultiTransform
  Direction = (0,1,-2e-16)
  Length = 20
  Length2 = 100
  Midplane = true
  Profile = -> Sketch028
  Suppressed = false
  Type = 0
FEATURE [Sketcher::SketchObject] Sketch029
  ArcFitTolerance = 0
  AttachmentOffset = pos=(0,0,2) rot=(0,0,1;0rad)
  AttachmentSupport = -> [XY_Plane013]
  FullyConstrained = true
  MakeInternals = false
  MapMode = 5
  Placement = pos=(0,0,2) rot=(0,0,1;0rad)
  sketch-geometry (9):
    g0: LineSegment StartX=23.95 StartY=5 StartZ=0 EndX=12.95 EndY=5 EndZ=0
    g1: LineSegment StartX=12.95 StartY=5 StartZ=0 EndX=12.95 EndY=-5 EndZ=0
    g2: LineSegment StartX=12.95 StartY=-5 StartZ=0 EndX=23.95 EndY=-5 EndZ=0
    g3: LineSegment StartX=23.95 StartY=-5 StartZ=0 EndX=23.95 EndY=-2.25 EndZ=0
    g4: ArcOfCircle CenterX=19 CenterY=0 CenterZ=0 NormalX=0 NormalY=0 NormalZ=1 AngleXU=0 Radius=2.25 StartAngle=1.5708 EndAngle=4.71239
    g5: LineSegment StartX=19 StartY=-2.25 StartZ=0 EndX=23.95 EndY=-2.25 EndZ=0
    g6: LineSegment StartX=19 StartY=2.25 StartZ=0 EndX=23.95 EndY=2.25 EndZ=0
    g7: LineSegment StartX=23.95 StartY=2.25 StartZ=0 EndX=23.95 EndY=5 EndZ=0
    g8: GeomPoint [constr] X=16.75 Y=0 Z=0
  constraints (23):
    c: Coincident(g0,g1)
    c: Coincident(g1,g2)
    c: Coincident(g2,g3)
    c: Coincident(g7,g0)
    c: Horizontal(g0)
    c: Horizontal(g2)
    c: Vertical(g1)
    c: Symmetric(g2,g0,g-1)
    c: Tangent(g4,g6) = 1.5708
    c: Tangent(g4,g5) = -1.5708
    c: Horizontal(g5)
    c: PointOnObject(g4,g-1)
    c: Coincident(g7,g6)
    c: Tangent(g3,g7)
    c: Coincident(g5,g3)
    c: Radius(g4) = 2.25
    c: Horizontal(g6)
    c: PointOnObject(g8,g4)
    c: PointOnObject(g8,g-1)
    c: DistanceX(g4) = 19
    c: DistanceX(g0) = 23.95
    c: DistanceY(g2,g0) = 10
    c: DistanceX(g0,g0) = 11
FEATURE [PartDesign::Pad] Pad013
  BaseFeature = -> Pocket003
  Direction = (0,0,1)
  Length = 7
  Length2 = 100
  Profile = -> Sketch029
  Suppressed = false
  Type = 0
FEATURE [Sketcher::SketchObject] Sketch030
  ArcFitTolerance = 0
  AttachmentOffset = pos=(0,0,9) rot=(0,0,1;0rad)
  AttachmentSupport = -> [XY_Plane013]
  FullyConstrained = true
  MakeInternals = false
  MapMode = 5
  Placement = pos=(0,0,9) rot=(0,0,1;0rad)
  sketch-geometry (4):
    g0: ArcOfCircle CenterX=19 CenterY=0 CenterZ=0 NormalX=0 NormalY=0 NormalZ=1 AngleXU=0 Radius=5 StartAngle=1.5708 EndAngle=4.71239
    g1: LineSegment StartX=19 StartY=-5 StartZ=0 EndX=25 EndY=-5 EndZ=0
    g2: LineSegment StartX=19 StartY=5 StartZ=0 EndX=25 EndY=5 EndZ=0
    g3: LineSegment StartX=25 StartY=5 StartZ=0 EndX=25 EndY=-5 EndZ=0
  constraints (11):
    c: Tangent(g0,g2) = 1.5708
    c: Tangent(g0,g1) = -1.5708
    c: Coincident(g1,g3) = -1.5708
    c: Coincident(g2,g3) = 1.5708
    c: Horizontal(g1)
    c: PointOnObject(g0,g-1)
    c: Vertical(g3)
    c: DistanceX(g0) = 19
    c: Radius(g0) = 5
    c: Horizontal(g2)
    c: DistanceX(g2) = 25
FEATURE [PartDesign::Pocket] Pocket004
  BaseFeature = -> Pad013
  Direction = (0,0,-1)
  Length = 10
  Length2 = 100
  Profile = -> Sketch030
  Reversed = true
  Suppressed = false
  Type = 0
FEATURE [PartDesign::Mirrored] Mirrored002
  BaseFeature = -> Pocket004
  MirrorPlane = -> YZ_Plane014
  Originals = -> [Pad013,Pocket004]
  Suppressed = false
  TransformMode = 0
FEATURE [Sketcher::SketchObject] Sketch031
  ArcFitTolerance = 0
  AttachmentSupport = -> [XZ_Plane013]
  FullyConstrained = true
  MakeInternals = false
  MapMode = 5
  Placement = pos=(0,0,0) rot=(1,0,0;1.5708rad)
  sketch-geometry (4):
    g0: LineSegment StartX=0 StartY=35 StartZ=0 EndX=0 EndY=29 EndZ=0
    g1: LineSegment StartX=0 StartY=29 StartZ=0 EndX=19.5 EndY=29 EndZ=0
    g2: LineSegment StartX=19.5 StartY=29 StartZ=0 EndX=19.5 EndY=35 EndZ=0
    g3: LineSegment StartX=0 StartY=35 StartZ=0 EndX=19.5 EndY=35 EndZ=0
  constraints (12):
    c: Coincident(g0,g1)
    c: Coincident(g1,g2)
    c: Horizontal(g1)
    c: Vertical(g0)
    c: Vertical(g2)
    c: PointOnObject(g0,g-2)
    c: DistanceX(g2) = 19.5
    c: DistanceY(g2) = 35
    c: DistanceY(g2,g2) = 6
    c: Coincident(g3,g0)
    c: Coincident(g3,g2)
    c: Horizontal(g3)
FEATURE [PartDesign::Groove] Groove
  Angle = 360
  Angle2 = 60
  Axis = (-3e-16,3e-16,1)
  Base = (0,0,0)
  BaseFeature = -> Mirrored002
  Profile = -> Sketch031
  ReferenceAxis = -> Z_Axis013
  Suppressed = false
  Type = 0
FEATURE [Sketcher::SketchObject] Sketch032
  ArcFitTolerance = 0
  AttachmentSupport = -> [XY_Plane013]
  FullyConstrained = true
  MakeInternals = false
  MapMode = 5
  sketch-geometry (2):
    g0: Circle CenterX=9.5 CenterY=0 CenterZ=0 NormalX=0 NormalY=0 NormalZ=1 AngleXU=0 Radius=2.85
    g1: Circle CenterX=-9.5 CenterY=0 CenterZ=0 NormalX=0 NormalY=0 NormalZ=1 AngleXU=0 Radius=2.85
  constraints (5):
    c: PointOnObject(g0,g-1)
    c: Symmetric(g0,g1,g-2)
    c: DistanceX(g1,g0) = 19
    c: Equal(g1,g0)
    c: Radius(g0) = 2.85
FEATURE [PartDesign::Pocket] Pocket005
  BaseFeature = -> Groove
  Direction = (0,0,-1)
  Length = 5
  Length2 = 100
  Midplane = true
  Profile = -> Sketch032
  Suppressed = false
  Type = 1
FEATURE [PartDesign::Fillet] Fillet001
  Base = -> Pocket005 [Edge52]
  BaseFeature = -> Pocket005
  Radius = 4
  SupportTransform = false
  Suppressed = false
  UseAllEdges = false
FEATURE [PartDesign::Body] Body013  label="Wallsocket"
  AllowCompound = false
  Group = -> [Sketch023,Pad009,Sketch024,Pocket002,Sketch025,Pad010,Sketch026,Pad011,Sketch027,Pad012,MultiTransform,Mirrored,Mirrored001,Sketch028,Pocket003,Sketch029,Pad013,Sketch030,Pocket004,Mirrored002,Sketch031,Groove,Sketch032,Pocket005,Fillet001]
  Origin = -> Origin013
  Tip = -> Fillet001
FEATURE [Sketcher::SketchObject] Sketch039  label="c cable trj"
  ArcFitTolerance = 0
  AttachmentOffset = pos=(0,0,-18) rot=(0,0,1;0rad)
  AttachmentSupport = -> [XZ_Plane015]
  FullyConstrained = true
  MakeInternals = false
  MapMode = 5
  Placement = pos=(0,18,-4e-15) rot=(1,0,0;1.5708rad)
  sketch-geometry (3):
    g0: LineSegment StartX=0 StartY=0 StartZ=0 EndX=0 EndY=-18 EndZ=0
    g1: ArcOfCircle CenterX=-12 CenterY=-18 CenterZ=0 NormalX=0 NormalY=0 NormalZ=1 AngleXU=0 Radius=12 StartAngle=4.71239 EndAngle=6.28319
    g2: LineSegment StartX=-12 StartY=-30 StartZ=0 EndX=-50 EndY=-30 EndZ=0
  constraints (8):
    c: Vertical(g0)
    c: Tangent(g0,g1) = 1.5708
    c: Tangent(g2,g1) = 1.5708
    c: Horizontal(g2)
    c: DistanceY(g2,g-1) = 30
    c: Radius(g1) = 12
    c: DistanceX(g2,g-1) = 50
    c: Coincident(g0,g-1)
FEATURE [Sketcher::SketchObject] Sketch096  label="pcb"
  ArcFitTolerance = 0
  AttachmentSupport = -> [XY_Plane020]
  FullyConstrained = true
  MakeInternals = false
  MapMode = 5
  sketch-geometry (12):
    g0: LineSegment StartX=-17.35 StartY=16.15 StartZ=0 EndX=17.35 EndY=16.15 EndZ=0
    g1: LineSegment StartX=17.35 StartY=16.15 StartZ=0 EndX=17.35 EndY=-16.15 EndZ=0
    g2: LineSegment StartX=17.35 StartY=-16.15 StartZ=0 EndX=-17.35 EndY=-16.15 EndZ=0
    g3: LineSegment StartX=-17.35 StartY=-16.15 StartZ=0 EndX=-17.35 EndY=16.15 EndZ=0
    g4: LineSegment [constr] StartX=-14.9 StartY=13.2 StartZ=0 EndX=14.9 EndY=13.2 EndZ=0
    g5: LineSegment [constr] StartX=14.9 StartY=13.2 StartZ=0 EndX=14.9 EndY=-13.2 EndZ=0
    g6: LineSegment [constr] StartX=14.9 StartY=-13.2 StartZ=0 EndX=-14.9 EndY=-13.2 EndZ=0
    g7: LineSegment [constr] StartX=-14.9 StartY=-13.2 StartZ=0 EndX=-14.9 EndY=13.2 EndZ=0
    g8: Circle CenterX=14.9 CenterY=13.2 CenterZ=0 NormalX=0 NormalY=0 NormalZ=1 AngleXU=0 Radius=1.5
    g9: Circle CenterX=-14.9 CenterY=13.2 CenterZ=0 NormalX=0 NormalY=0 NormalZ=1 AngleXU=0 Radius=1.5
    g10: Circle CenterX=-14.9 CenterY=-13.2 CenterZ=0 NormalX=0 NormalY=0 NormalZ=1 AngleXU=0 Radius=1.5
    g11: Circle CenterX=14.9 CenterY=-13.2 CenterZ=0 NormalX=0 NormalY=0 NormalZ=1 AngleXU=0 Radius=1.5
  constraints (28):
    c: Coincident(g0,g1)
    c: Coincident(g1,g2)
    c: Coincident(g2,g3)
    c: Coincident(g3,g0)
    c: Horizontal(g2)
    c: Vertical(g3)
    c: DistanceX(g0,g0) = 34.7
    c: Symmetric(g0,g0,g-2)
    c: Symmetric(g1,g0,g-1)
    c: DistanceY(g1,g1) = 32.3
    c: Coincident(g4,g5)
    c: Coincident(g5,g6)
    c: Coincident(g6,g7)
    c: Coincident(g7,g4)
    c: Horizontal(g6)
    c: Vertical(g7)
    c: Symmetric(g4,g4,g-2)
    c: Symmetric(g5,g4,g-1)
    c: DistanceX(g4,g4) = 29.8
    c: DistanceY(g5,g5) = 26.4
    c: Coincident(g8,g4)
    c: Radius(g8) = 1.5
    c: Coincident(g9,g4)
    c: Coincident(g10,g6)
    c: Coincident(g11,g5)
    c: Equal(g11,g10)
    c: Equal(g10,g9)
    c: Equal(g9,g8)
FEATURE [PartDesign::Pad] Pad016  label="PCB001"
  AllowMultiFace = false
  Direction = (0,0,1)
  Length = 1.8
  Length2 = 100
  Profile = -> Sketch096
  Suppressed = false
  Type = 0
FEATURE [PartDesign::Plane] DatumPlane  label="top of pcb"
  AttachmentOffset = pos=(0,0,1.8) rot=(0,0,1;0rad)
  AttachmentSupport = -> [XY_Plane020]
  Length = 60
  MapMode = 5
  Placement = pos=(0,0,1.8) rot=(0,0,1;0rad)
  ResizeMode = 0
  Width = 60
FEATURE [Sketcher::SketchObject] Sketch097
  ArcFitTolerance = 0
  AttachmentSupport = -> [DatumPlane]
  FullyConstrained = true
  MakeInternals = false
  MapMode = 5
  Placement = pos=(0,0,1.8) rot=(0,0,1;0rad)
  sketch-geometry (4):
    g0: LineSegment StartX=4 StartY=14.5 StartZ=0 EndX=8 EndY=14.5 EndZ=0
    g1: LineSegment StartX=8 StartY=14.5 StartZ=0 EndX=8 EndY=3 EndZ=0
    g2: LineSegment StartX=8 StartY=3 StartZ=0 EndX=4 EndY=3 EndZ=0
    g3: LineSegment StartX=4 StartY=3 StartZ=0 EndX=4 EndY=14.5 EndZ=0
  constraints (12):
    c: Coincident(g0,g1)
    c: Coincident(g1,g2)
    c: Coincident(g2,g3)
    c: Coincident(g3,g0)
    c: Horizontal(g0)
    c: Horizontal(g2)
    c: Vertical(g1)
    c: Vertical(g3)
    c: DistanceX(g2) = 4
    c: DistanceY(g2) = 3
    c: DistanceY(g1,g1) = 11.5
    c: DistanceX(g0,g0) = 4
FEATURE [PartDesign::Pad] Pad017
  AllowMultiFace = false
  BaseFeature = -> Pad016
  Direction = (0,0,1)
  Length = 11.8
  Length2 = 100
  Profile = -> Sketch097
  Suppressed = false
  Type = 0
FEATURE [Sketcher::SketchObject] Sketch098
  ArcFitTolerance = 0
  AttachmentOffset = pos=(0,0,-1) rot=(0,0,1;0rad)
  AttachmentSupport = -> [Pad017]
  ExternalGeometry = -> [DatumPlane,Sketch097]
  FullyConstrained = true
  MakeInternals = false
  MapMode = 5
  Placement = pos=(0,4,-2e-16) rot=(1,0,0;1.5708rad)
  sketch-geometry (8):
    g0: ArcOfCircle CenterX=2.1 CenterY=13.6 CenterZ=0 NormalX=0 NormalY=0 NormalZ=1 AngleXU=0 Radius=3.4 StartAngle=0 EndAngle=2.0944
    g1: ArcOfCircle CenterX=2.1 CenterY=13.6 CenterZ=0 NormalX=0 NormalY=0 NormalZ=1 AngleXU=0 Radius=4.4 StartAngle=0 EndAngle=2.0944
    g2: LineSegment StartX=-0.1 StartY=17.4105 StartZ=0 EndX=0.4 EndY=16.5445 EndZ=0
    g3: LineSegment [constr] StartX=2.1 StartY=18 StartZ=0 EndX=2.1 EndY=13.6 EndZ=0
    g4: LineSegment [constr] StartX=6 StartY=1.8 StartZ=0 EndX=6 EndY=13.6 EndZ=0
    g5: LineSegment StartX=6.5 StartY=13.6 StartZ=0 EndX=6.5 EndY=1.8 EndZ=0
    g6: LineSegment StartX=6.5 StartY=1.8 StartZ=0 EndX=5.5 EndY=1.8 EndZ=0
    g7: LineSegment StartX=5.5 StartY=1.8 StartZ=0 EndX=5.5 EndY=13.6 EndZ=0
  constraints (22):
    c: Coincident(g1,g0)
    c: Coincident(g2,g1)
    c: Coincident(g2,g0)
    c: PointOnObject(g0,g2)
    c: PointOnObject(g3,g1)
    c: Coincident(g3,g0)
    c: DistanceY(g3) = 18
    c: Distance(g2) = 1
    c: Symmetric(g1,g0,g4)
    c: Vertical(g3)
    c: Angle(g3,g2) = 0.523599
    c: Coincident(g5,g6)
    c: Coincident(g6,g7)
    c: Horizontal(g6)
    c: Vertical(g5)
    c: PointOnObject(g5,g-3)
    c: Symmetric(g-4,g-4,g4)
    c: PointOnObject(g4,g-3)
    c: DistanceY(g1) = 13.6
    c: Tangent(g0,g7) = -1.5708
    c: Tangent(g1,g5) = 1.5708
    c: Equal(g5,g4)
FEATURE [PartDesign::Pad] Pad018
  AllowMultiFace = false
  BaseFeature = -> Pad017
  Direction = (0,-1,2e-16)
  Length = 9.5
  Length2 = 100
  Profile = -> Sketch098
  Reversed = true
  Suppressed = false
  Type = 0
FEATURE [PartDesign::Fillet] Fillet004
  Base = -> Pad018 [Edge41,Edge46,Edge42,Edge45]
  BaseFeature = -> Pad018
  Radius = 0.4
  SupportTransform = false
  Suppressed = false
  UseAllEdges = false
FEATURE [Sketcher::SketchObject] Sketch099
  ArcFitTolerance = 0
  AttachmentOffset = pos=(0,0,3) rot=(0,0,1;0rad)
  AttachmentSupport = -> [XZ_Plane020]
  ExternalGeometry = -> [DatumPlane]
  FullyConstrained = true
  MakeInternals = false
  MapMode = 5
  Placement = pos=(0,-3,7e-16) rot=(1,0,0;1.5708rad)
  sketch-geometry (5):
    g0: ArcOfCircle CenterX=12.35 CenterY=5.8 CenterZ=0 NormalX=0 NormalY=0 NormalZ=1 AngleXU=0 Radius=1.5 StartAngle=3e-16 EndAngle=1.5708
    g1: LineSegment StartX=13.85 StartY=5.8 StartZ=0 EndX=13.85 EndY=1.8 EndZ=0
    g2: LineSegment StartX=13.85 StartY=1.8 StartZ=0 EndX=12.35 EndY=1.8 EndZ=0
    g3: LineSegment StartX=12.35 StartY=1.8 StartZ=0 EndX=12.35 EndY=7.3 EndZ=0
    g4: LineSegment [constr] StartX=12.35 StartY=7.3 StartZ=0 EndX=12.35 EndY=8.8 EndZ=0
  constraints (15):
    c: Vertical(g1)
    c: Coincident(g1,g2)
    c: Horizontal(g2)
    c: Coincident(g2,g3)
    c: Vertical(g3)
    c: Coincident(g0,g3)
    c: PointOnObject(g0,g3)
    c: Tangent(g0,g1) = 1.5708
    c: DistanceY(g1,g0) = 5.5
    c: Radius(g0) = 1.5
    c: Coincident(g4,g0)
    c: Vertical(g4)
    c: Equal(g2,g4)
    c: DistanceX(g2) = 12.35
    c: PointOnObject(g2,g-3)
FEATURE [PartDesign::Revolution] Revolution013
  AllowMultiFace = false
  Angle = 360
  Angle2 = 60
  Axis = (0,3e-16,1.5)
  Base = (12.35,-3,7.3)
  BaseFeature = -> Fillet004
  Profile = -> Sketch099
  ReferenceAxis = -> Sketch099 [Axis]
  Reversed = true
  Suppressed = false
  Type = 0
FEATURE [PartDesign::LinearPattern] LinearPattern002
  BaseFeature = -> Revolution013
  Direction = -> Y_Axis020
  Length = 14
  Mode = 0
  Occurrences = 4
  Offset = 4.66667
  Originals = -> [Revolution013]
  Suppressed = false
  TransformMode = 0
FEATURE [Sketcher::SketchObject] Sketch100
  ArcFitTolerance = 0
  AttachmentSupport = -> [DatumPlane]
  FullyConstrained = true
  MakeInternals = false
  MapMode = 5
  Placement = pos=(0,0,1.8) rot=(0,0,1;0rad)
  sketch-geometry (4):
    g0: LineSegment StartX=1.95 StartY=15.15 StartZ=0 EndX=-8.05 EndY=15.15 EndZ=0
    g1: LineSegment StartX=-8.05 StartY=15.15 StartZ=0 EndX=-8.05 EndY=-5.35 EndZ=0
    g2: LineSegment StartX=-8.05 StartY=-5.35 StartZ=0 EndX=1.95 EndY=-5.35 EndZ=0
    g3: LineSegment StartX=1.95 StartY=-5.35 StartZ=0 EndX=1.95 EndY=15.15 EndZ=0
  constraints (12):
    c: Coincident(g0,g1)
    c: Coincident(g1,g2)
    c: Coincident(g2,g3)
    c: Coincident(g3,g0)
    c: Horizontal(g0)
    c: Horizontal(g2)
    c: Vertical(g1)
    c: Vertical(g3)
    c: DistanceY(g1,g1) = 20.5
    c: DistanceX(g0,g0) = 10
    c: DistanceX(g2) = 1.95
    c: DistanceY(g2) = -5.35
FEATURE [PartDesign::Pad] Pad019
  AllowMultiFace = false
  BaseFeature = -> LinearPattern002
  Direction = (0,0,1)
  Length = 8.3
  Length2 = 100
  Profile = -> Sketch100
  Suppressed = false
  Type = 0
FEATURE [Sketcher::SketchObject] Sketch101
  ArcFitTolerance = 0
  AttachmentSupport = -> [DatumPlane]
  FullyConstrained = true
  MakeInternals = false
  MapMode = 5
  Placement = pos=(0,0,1.8) rot=(0,0,1;0rad)
  sketch-geometry (4):
    g0: LineSegment StartX=-11.35 StartY=11.35 StartZ=0 EndX=-8.81 EndY=11.35 EndZ=0
    g1: LineSegment StartX=-8.81 StartY=11.35 StartZ=0 EndX=-8.81 EndY=8.81 EndZ=0
    g2: LineSegment StartX=-8.81 StartY=8.81 StartZ=0 EndX=-11.35 EndY=8.81 EndZ=0
    g3: LineSegment StartX=-11.35 StartY=8.81 StartZ=0 EndX=-11.35 EndY=11.35 EndZ=0
  constraints (12):
    c: Coincident(g0,g1)
    c: Coincident(g1,g2)
    c: Coincident(g2,g3)
    c: Coincident(g3,g0)
    c: Horizontal(g0)
    c: Horizontal(g2)
    c: Vertical(g1)
    c: Vertical(g3)
    c: Equal(g3,g0)
    c: DistanceX(g0,g0) = 2.54
    c: DistanceX(g1) = -8.81
    c: DistanceY(g1) = 8.81
FEATURE [PartDesign::Pad] Pad020
  AllowMultiFace = false
  BaseFeature = -> Pad019
  Direction = (0,0,1)
  Length = 16.5
  Length2 = 100
  Profile = -> Sketch101
  Suppressed = false
  Type = 0
FEATURE [Sketcher::SketchObject] Sketch102
  ArcFitTolerance = 0
  AttachmentSupport = -> [DatumPlane]
  ExternalGeometry = -> [Sketch101]
  FullyConstrained = true
  MakeInternals = false
  MapMode = 5
  Placement = pos=(0,0,1.8) rot=(0,0,1;0rad)
  sketch-geometry (2):
    g0: Circle [constr] CenterX=-10.08 CenterY=10.08 CenterZ=0 NormalX=0 NormalY=0 NormalZ=1 AngleXU=0 Radius=1.27
    g1: Circle CenterX=-10.08 CenterY=10.08 CenterZ=0 NormalX=0 NormalY=0 NormalZ=1 AngleXU=0 Radius=0.5
  constraints (5):
    c: Coincident(g1,g0)
    c: Radius(g1) = 0.5
    c: Tangent(g-5,g0)
    c: Tangent(g-3,g0)
    c: Tangent(g0,g-4)
FEATURE [Sketcher::SketchObject] Sketch105
  ArcFitTolerance = 0
  AttachmentSupport = -> [XY_Plane020]
  ExternalGeometry = -> [Sketch101]
  FullyConstrained = true
  MakeInternals = false
  MapMode = 5
  sketch-geometry (1):
    g0: LineSegment StartX=-10.08 StartY=10.08 StartZ=0 EndX=-10.08 EndY=7.54 EndZ=0
  constraints (3):
    c: Symmetric(g-4,g-4,g0)
    c: Symmetric(g0,g0,g-4)
    c: Equal(g0,g-4)
FEATURE [PartDesign::Plane] DatumPlane001  label="wire plane"
  AttachmentSupport = -> [Sketch105,Y_Axis020]
  Length = 60
  MapMode = 7
  Placement = pos=(-10.08,10.08,0) rot=(1,0,0;1.5708rad)
  ResizeMode = 0
  Width = 60
FEATURE [Sketcher::SketchObject] Sketch103
  ArcFitTolerance = 0
  AttachmentSupport = -> [DatumPlane001]
  ExternalGeometry = -> [Sketch101,DatumPlane]
  FullyConstrained = true
  MakeInternals = false
  MapMode = 5
  Placement = pos=(-10.08,10.08,0) rot=(1,0,0;1.5708rad)
  sketch-geometry (3):
    g0: ArcOfCircle CenterX=-5 CenterY=18.2 CenterZ=0 NormalX=0 NormalY=0 NormalZ=1 AngleXU=0 Radius=5 StartAngle=0 EndAngle=2.35619
    g1: LineSegment [constr] StartX=-8.53553 StartY=21.7355 StartZ=0 EndX=-5 EndY=18.2 EndZ=0
    g2: LineSegment StartX=3.6e-15 StartY=18.2 StartZ=0 EndX=3.6e-15 EndY=1.8 EndZ=0
  constraints (8):
    c: Coincident(g1,g0)
    c: Coincident(g1,g0)
    c: Radius(g0) = 5
    c: DistanceY(g0) = 18.2
    c: Symmetric(g-3,g-3,g2)
    c: Tangent(g2,g0) = 1.5708
    c: Angle(g1,g-1) = 0.785398
    c: PointOnObject(g2,g-4)
FEATURE [PartDesign::AdditivePipe] AdditivePipe003
  AuxilleryCurvelinear = true
  AuxillerySpineTangent = false
  BaseFeature = -> Pad020
  Binormal = (0,0,0)
  Mode = 0
  Profile = -> Sketch102
  Refine = true
  Spine = -> Sketch103
  SpineTangent = false
  Suppressed = false
  Transformation = 0
  Transition = 0
FEATURE [PartDesign::LinearPattern] LinearPattern003
  BaseFeature = -> AdditivePipe003
  Direction = -> Y_Axis020
  Length = 7.62
  Mode = 0
  Occurrences = 4
  Offset = 2.54
  Originals = -> [Pad020,AdditivePipe003]
  Reversed = true
  Suppressed = false
  TransformMode = 0
FEATURE [Sketcher::SketchObject] Sketch104
  ArcFitTolerance = 0
  AttachmentSupport = -> [DatumPlane]
  ExternalGeometry = -> [LinearPattern003]
  FullyConstrained = true
  MakeInternals = false
  MapMode = 5
  Placement = pos=(0,0,1.8) rot=(0,0,1;0rad)
  sketch-geometry (4):
    g0: LineSegment StartX=-8.05 StartY=-10.31 StartZ=0 EndX=2.11 EndY=-10.31 EndZ=0
    g1: LineSegment StartX=2.11 StartY=-10.31 StartZ=0 EndX=2.11 EndY=-12.85 EndZ=0
    g2: LineSegment StartX=2.11 StartY=-12.85 StartZ=0 EndX=-8.05 EndY=-12.85 EndZ=0
    g3: LineSegment StartX=-8.05 StartY=-12.85 StartZ=0 EndX=-8.05 EndY=-10.31 EndZ=0
  constraints (12):
    c: Coincident(g0,g1)
    c: Coincident(g1,g2)
    c: Coincident(g2,g3)
    c: Coincident(g3,g0)
    c: Horizontal(g0)
    c: Horizontal(g2)
    c: Vertical(g1)
    c: Vertical(g3)
    c: DistanceY(g3,g3) = 2.54
    c: DistanceX(g0,g0) = 10.16
    c: DistanceX(g0) = 2.11
    c: DistanceY(g0) = -10.31
FEATURE [PartDesign::Pad] Pad021
  AllowMultiFace = false
  BaseFeature = -> LinearPattern003
  Direction = (0,0,1)
  Length = 8.6
  Length2 = 100
  Profile = -> Sketch104
  ReferenceAxis = -> Sketch104 [N_Axis]
  Suppressed = false
  Type = 0
FEATURE [PartDesign::Body] Body020  label="ULN2003"
  AllowCompound = false
  Group = -> [Sketch096,Pad016,Sketch097,DatumPlane,Pad017,Sketch098,Pad018,Fillet004,Sketch099,Revolution013,LinearPattern002,Sketch100,Pad019,Sketch101,Pad020,Sketch102,Sketch103,Sketch105,DatumPlane001,AdditivePipe003,LinearPattern003,Sketch104,Pad021]
  Origin = -> Origin020
  Placement = pos=(0,-7,-41) rot=(0,0,1;0rad)
  Tip = -> Pad021
FEATURE [Part::FeaturePython] Screw002  label="M4x20-Screw002"  # WARN: FeaturePython — macro-defined, semantics opaque (R4)
  Diameter = 2
  Invert = false
  LeftHanded = false
  Length = 6
  LengthCustom = 20
  MatchOuter = false
  Placement = pos=(19,0,9) rot=(0,0,1;0rad)
  Thread = false
  Type = 84
FEATURE [Part::FeaturePython] Nut002  label="M4-Nut001"  # WARN: FeaturePython — macro-defined, semantics opaque (R4)
  Diameter = 6
  Invert = false
  LeftHanded = false
  MatchOuter = false
  Placement = pos=(19,0,-5.8) rot=(0.707107,0.707107,0;3.14159rad)
  Thread = false
  Type = 31
FEATURE [Part::FeaturePython] Screw003  label="M4x20-Screw"  # WARN: FeaturePython — macro-defined, semantics opaque (R4)
  Diameter = 2
  Invert = false
  LeftHanded = false
  Length = 6
  LengthCustom = 20
  MatchOuter = false
  Placement = pos=(-19,0,9) rot=(0,0,1;0rad)
  Thread = false
  Type = 84
FEATURE [Part::FeaturePython] Nut003  label="M4-Nut"  # WARN: FeaturePython — macro-defined, semantics opaque (R4)
  Diameter = 6
  Invert = false
  LeftHanded = false
  MatchOuter = false
  Placement = pos=(-19,0,-5.8) rot=(0.707107,0.707107,0;3.14159rad)
  Thread = false
  Type = 31
FEATURE [PartDesign::SubShapeBinder] Binder  label="cp ref pcb"
  BindCopyOnChange = 0
  BindMode = 0
  ClaimChildren = false
  Context = -> Body [Binder.]
  Fuse = false
  MakeFace = true
  OffsetFill = false
  OffsetIntersection = false
  OffsetJoinType = 0
  OffsetOpenResult = false
  PartialLoad = false
  Refine = true
  Relative = true
  Support = -> [Part__Feature[Face46]]
  _Version = 2
FEATURE [PartDesign::SubShapeBinder] Binder001  label="cp ref housing ESP"
  BindCopyOnChange = 0
  BindMode = 0
  ClaimChildren = false
  Context = -> Body [Binder001.]
  Fuse = false
  MakeFace = true
  OffsetFill = false
  OffsetIntersection = false
  OffsetJoinType = 0
  OffsetOpenResult = false
  PartialLoad = false
  Refine = true
  Relative = true
  Support = -> [Part__Feature[Face987,Face424,Face706]]
  _Version = 2
FEATURE [PartDesign::SubShapeBinder] Binder002  label="cp ref pins"
  BindCopyOnChange = 0
  BindMode = 0
  ClaimChildren = false
  Context = -> Body [Binder002.]
  Fuse = false
  MakeFace = true
  OffsetFill = false
  OffsetIntersection = false
  OffsetJoinType = 0
  OffsetOpenResult = false
  PartialLoad = false
  Refine = true
  Relative = true
  Support = -> [Part__Feature[Edge654,Edge649]]
  _Version = 2
FEATURE [PartDesign::Point] DatumPoint  label="cp ref gnd"
  AttacherType = Attacher::AttachEnginePoint
  AttachmentSupport = -> [Binder002]
  MapMode = 36
  Placement = pos=(11.43,0.999,3.49) rot=(0,1,0;3.14159rad)
FEATURE [PartDesign::Point] DatumPoint001  label="cp ref VCC"
  AttacherType = Attacher::AttachEnginePoint
  AttachmentSupport = -> [Binder002]
  MapMode = 36
  Placement = pos=(11.43,0.999,6.03) rot=(0,1,0;3.14159rad)
FEATURE [PartDesign::Plane] DatumPlane002  label="cp pln capacitor"
  AttachmentOffset = pos=(0,0,-3) rot=(0,0,1;0rad)
  AttachmentSupport = -> [DatumPoint,XY_Plane]
  Length = 60
  MapMode = 6
  Placement = pos=(11.43,0.999,0.49) rot=(0,0,1;3.14159rad)
  ResizeMode = 0
  Width = 60
FEATURE [Sketcher::SketchObject] Sketch
  ArcFitTolerance = 1e-06
  AttachmentSupport = -> [DatumPlane002]
  ExternalGeometry = -> [Binder001]
  FullyConstrained = true
  MakeInternals = false
  MapMode = 5
  Placement = pos=(11.43,0.999,0.49) rot=(0,0,1;3.14159rad)
  sketch-geometry (1):
    g0: Circle CenterX=-0.541184 CenterY=-4.25 CenterZ=0 NormalX=0 NormalY=0 NormalZ=1 AngleXU=0 Radius=4.25
  constraints (3):
    c: Tangent(g0,g-1)
    c: Diameter(g0) = 8.5
    c: PointOnObject(g-4,g0)
FEATURE [PartDesign::Pad] Pad
  Direction = (0,0,1)
  Length = 17
  Length2 = 10
  Placement = pos=(11.43,0.999,0.49) rot=(0,0,1;3.14159rad)
  Profile = -> Sketch
  ReferenceAxis = -> Sketch [N_Axis]
  Refine = true
  Reversed = true
  Suppressed = false
  Type = 0
FEATURE [PartDesign::Body] Body  label="Capacitor 1 mF"
  AllowCompound = false
  Group = -> [Binder,Binder002,DatumPoint,DatumPoint001,Binder001,DatumPlane002,Sketch,Pad]
  Origin = -> Origin
  Tip = -> Pad
FEATURE [Part::Compound] Compound004  label="ESP with Capacitor"
  Links = -> [Part__Feature,Body]
  Placement = pos=(0,-10.4,-53) rot=(1,0,0;1.5708rad)
FEATURE [PartDesign::Plane] DatumPlane003  label="c cable pln crs"
  AttachmentSupport = -> [Sketch039]
  Length = 87.2474
  MapMode = 7
  Placement = pos=(0,18,-4e-15) rot=(0,0,1;0rad)
  ResizeMode = 0
  Width = 62.2474
FEATURE [Sketcher::SketchObject] Sketch038  label="c cable crs"
  ArcFitTolerance = 0
  AttachmentSupport = -> [DatumPlane003]
  FullyConstrained = true
  MakeInternals = false
  MapMode = 5
  Placement = pos=(0,18,-4e-15) rot=(0,0,1;0rad)
  sketch-geometry (6):
    g0: ArcOfCircle CenterX=0 CenterY=1.2 CenterZ=0 NormalX=0 NormalY=0 NormalZ=1 AngleXU=0 Radius=1.8 StartAngle=1e-16 EndAngle=3.14159
    g1: ArcOfCircle CenterX=-1e-16 CenterY=-1.2 CenterZ=0 NormalX=0 NormalY=0 NormalZ=1 AngleXU=0 Radius=1.8 StartAngle=3.14159 EndAngle=6.28319
    g2: LineSegment StartX=1.8 StartY=1.2 StartZ=0 EndX=1.8 EndY=-1.2 EndZ=0
    g3: LineSegment StartX=-1.8 StartY=1.2 StartZ=0 EndX=-1.8 EndY=-1.2 EndZ=0
    g4: GeomPoint X=0 Y=3 Z=0
    g5: GeomPoint X=0 Y=-3 Z=0
  constraints (13):
    c: Tangent(g0,g2) = 1.5708
    c: Tangent(g0,g3) = -1.5708
    c: Tangent(g1,g2) = 1.5708
    c: Tangent(g1,g3) = -1.5708
    c: Equal(g0,g1)
    c: Vertical(g3)
    c: PointOnObject(g0,g-2)
    c: PointOnObject(g4,g0)
    c: PointOnObject(g5,g1)
    c: PointOnObject(g5,g-2)
    c: Symmetric(g4,g5,g-1)
    c: DistanceY(g5,g4) = 6
    c: DistanceX(g0,g0) = 3.6
FEATURE [PartDesign::AdditivePipe] AdditivePipe
  AuxilleryCurvelinear = true
  AuxillerySpineTangent = false
  Binormal = (0,0,0)
  Mode = 0
  Placement = pos=(0,18,-4e-15) rot=(0,0,1;0rad)
  Profile = -> Sketch038
  Refine = true
  Spine = -> Sketch039
  SpineTangent = false
  Suppressed = false
  Transformation = 0
  Transition = 0
FEATURE [PartDesign::Body] Body015  label="Cable"
  AllowCompound = false
  Group = -> [Sketch038,Sketch039,DatumPlane003,AdditivePipe]
  Origin = -> Origin015
  Tip = -> AdditivePipe
FEATURE [PartDesign::SubShapeBinder] Binder003  label="sk ref wallsocket"
  BindCopyOnChange = 0
  BindMode = 0
  ClaimChildren = false
  Context = -> Body021 [Binder003.]
  Fuse = false
  MakeFace = true
  OffsetFill = false
  OffsetIntersection = false
  OffsetJoinType = 0
  OffsetOpenResult = false
  PartialLoad = false
  Refine = true
  Relative = true
  Support = -> [Body013[Fillet001.Face4]]
  _Version = 2
FEATURE [PartDesign::SubShapeBinder] Binder004  label="sk ref nuts"
  BindCopyOnChange = 0
  BindMode = 0
  ClaimChildren = false
  Context = -> Body021 [Binder004.]
  Fuse = false
  MakeFace = true
  OffsetFill = false
  OffsetIntersection = false
  OffsetJoinType = 0
  OffsetOpenResult = false
  PartialLoad = false
  Refine = true
  Relative = true
  Support = -> [Nut003[Face18],Nut002[Face18]]
  _Version = 2
FEATURE [PartDesign::SubShapeBinder] Binder005  label="sk ref relay"
  BindCopyOnChange = 0
  BindMode = 0
  ClaimChildren = false
  Context = -> Body021 [Binder005.]
  Fuse = false
  MakeFace = true
  OffsetFill = false
  OffsetIntersection = false
  OffsetJoinType = 0
  OffsetOpenResult = false
  PartialLoad = false
  Refine = true
  Relative = true
  Support = -> [Compound[Face8,Face9,Face15]]
  _Version = 2
FEATURE [PartDesign::SubShapeBinder] Binder006  label="sk ref ULN2003"
  BindCopyOnChange = 0
  BindMode = 0
  ClaimChildren = false
  Context = -> Body021 [Binder006.]
  Fuse = false
  MakeFace = true
  OffsetFill = false
  OffsetIntersection = false
  OffsetJoinType = 0
  OffsetOpenResult = false
  PartialLoad = false
  Refine = true
  Relative = true
  Support = -> [Body020[Pad021.Face42,Pad021.Face24,Pad021.Face3,Pad021.Face37,Pad021.Face11]]
  _Version = 2
FEATURE [PartDesign::SubShapeBinder] Binder007  label="sk ref ESP32"
  BindCopyOnChange = 0
  BindMode = 0
  ClaimChildren = false
  Context = -> Body021 [Binder007.]
  Fuse = false
  MakeFace = true
  OffsetFill = false
  OffsetIntersection = false
  OffsetJoinType = 0
  OffsetOpenResult = false
  PartialLoad = false
  Refine = true
  Relative = true
  Support = -> [Compound004[Face114,Face113,Face412,Face410,Face5497,Face5496,Edge4629,Edge4648]]
  _Version = 2
FEATURE [PartDesign::SubShapeBinder] Binder008  label="sk ref cable"
  BindCopyOnChange = 0
  BindMode = 0
  ClaimChildren = false
  Context = -> Body021 [Binder008.]
  Fuse = false
  MakeFace = true
  OffsetFill = false
  OffsetIntersection = false
  OffsetJoinType = 0
  OffsetOpenResult = false
  PartialLoad = false
  Refine = true
  Relative = true
  Support = -> [Body015[Sketch038.,Sketch039.]]
  _Version = 2
FEATURE [Sketcher::SketchObject] Sketch106  label="sk right"
  ArcFitTolerance = 1e-06
  AttachmentSupport = -> [YZ_Plane022]
  ExternalGeometry = -> [Binder003,Binder008]
  FullyConstrained = true
  MakeInternals = false
  MapMode = 5
  Placement = pos=(0,0,0) rot=(0.57735,0.57735,0.57735;2.0944rad)
  sketch-geometry (9):
    g0: LineSegment StartX=-30.6 StartY=0 StartZ=0 EndX=-30.6 EndY=-58 EndZ=0
    g1: LineSegment StartX=-30.6 StartY=-58 StartZ=0 EndX=18 EndY=-58 EndZ=0
    g2: LineSegment StartX=30.6 StartY=-20 StartZ=0 EndX=30.6 EndY=0 EndZ=0
    g3: LineSegment StartX=30.6 StartY=0 StartZ=0 EndX=28.3 EndY=0 EndZ=0
    g4: LineSegment StartX=-28.3 StartY=1.5 StartZ=0 EndX=-28.3 EndY=0 EndZ=0
    g5: LineSegment StartX=28.3 StartY=0 StartZ=0 EndX=28.3 EndY=1.5 EndZ=0
    g6: LineSegment StartX=28.3 StartY=1.5 StartZ=0 EndX=-28.3 EndY=1.5 EndZ=0
    g7: LineSegment StartX=-28.3 StartY=0 StartZ=0 EndX=-30.6 EndY=0 EndZ=0
    g8: ArcOfCircle CenterX=-33.0016 CenterY=-20 CenterZ=0 NormalX=0 NormalY=0 NormalZ=1 AngleXU=0 Radius=63.6016 StartAngle=5.64284 EndAngle=6.28319
  constraints (23):
    c: Coincident(g0,g1)
    c: Coincident(g2,g3)
    c: Coincident(g7,g0)
    c: Vertical(g0)
    c: Vertical(g2)
    c: Horizontal(g1)
    c: Coincident(g0,g-3)
    c: Coincident(g2,g-4)
    c: Coincident(g5,g6)
    c: Coincident(g6,g4)
    c: Vertical(g4)
    c: Vertical(g5)
    c: Horizontal(g6)
    c: Coincident(g3,g5)
    c: Coincident(g3,g-5)
    c: Coincident(g4,g7)
    c: Coincident(g4,g-6)
    c: DistanceY(g5,g5) = 1.5
    c: Tangent(g2,g8) = -1.5708
    c: DistanceY(g0,g-1) = 58
    c: Coincident(g1,g8)
    c: DistanceY(g2,g2) = 20
    c: DistanceX(g-1,g1) = 18
FEATURE [Sketcher::SketchObject] Sketch107  label="sk front"
  ArcFitTolerance = 1e-06
  AttachmentSupport = -> [XZ_Plane021]
  ExternalGeometry = -> [Binder003,Sketch106]
  FullyConstrained = true
  MakeInternals = false
  MapMode = 5
  Placement = pos=(0,0,0) rot=(1,0,0;1.5708rad)
  sketch-geometry (8):
    g0: LineSegment StartX=-28.3 StartY=1.5 StartZ=0 EndX=-28.3 EndY=0 EndZ=0
    g1: LineSegment StartX=28.3 StartY=0 StartZ=0 EndX=28.3 EndY=1.5 EndZ=0
    g2: LineSegment StartX=28.3 StartY=1.5 StartZ=0 EndX=-28.3 EndY=1.5 EndZ=0
    g3: LineSegment StartX=-30.6 StartY=0 StartZ=0 EndX=-30.6 EndY=-58 EndZ=0
    g4: LineSegment StartX=-30.6 StartY=-58 StartZ=0 EndX=30.6 EndY=-58 EndZ=0
    g5: LineSegment StartX=30.6 StartY=-58 StartZ=0 EndX=30.6 EndY=0 EndZ=0
    g6: LineSegment StartX=30.6 StartY=0 StartZ=0 EndX=28.3 EndY=0 EndZ=0
    g7: LineSegment StartX=-28.3 StartY=0 StartZ=0 EndX=-30.6 EndY=0 EndZ=0
  constraints (20):
    c: Coincident(g1,g2)
    c: Coincident(g2,g0)
    c: Vertical(g0)
    c: Vertical(g1)
    c: Horizontal(g2)
    c: Coincident(g3,g4)
    c: Coincident(g4,g5)
    c: Coincident(g5,g6)
    c: Coincident(g7,g3)
    c: Vertical(g3)
    c: Vertical(g5)
    c: Horizontal(g4)
    c: Coincident(g3,g-3)
    c: PointOnObject(g-8,g4)
    c: Coincident(g1,g6)
    c: Coincident(g0,g7)
    c: Coincident(g0,g-4)
    c: Coincident(g1,g-5)
    c: Coincident(g5,g-6)
    c: PointOnObject(g-7,g2)
FEATURE [Sketcher::SketchObject] Sketch108  label="sk relay slot"
  ArcFitTolerance = 1e-06
  AttachmentSupport = -> [XZ_Plane021]
  ExternalGeometry = -> [Binder005]
  FullyConstrained = true
  MakeInternals = false
  MapMode = 5
  Placement = pos=(0,0,0) rot=(1,0,0;1.5708rad)
  sketch-geometry (14):
    g0: LineSegment StartX=-5.1 StartY=-0.7 StartZ=0 EndX=-5.1 EndY=-18.15 EndZ=0
    g1: LineSegment StartX=-5.1 StartY=-22.5 StartZ=0 EndX=11.1 EndY=-22.5 EndZ=0
    g2: LineSegment StartX=11.1 StartY=-22.5 StartZ=0 EndX=11.1 EndY=-20.25 EndZ=0
    g3: LineSegment StartX=11.1 StartY=-0.7 StartZ=0 EndX=-5.1 EndY=-0.7 EndZ=0
    g4: LineSegment StartX=-6.05 StartY=-18.15 StartZ=0 EndX=-6.05 EndY=-20.25 EndZ=0
    g5: LineSegment StartX=-6.05 StartY=-20.25 StartZ=0 EndX=-5.1 EndY=-20.25 EndZ=0
    g6: LineSegment StartX=12.05 StartY=-20.25 StartZ=0 EndX=12.05 EndY=-18.15 EndZ=0
    g7: LineSegment StartX=12.05 StartY=-18.15 StartZ=0 EndX=11.1 EndY=-18.15 EndZ=0
    g8: Circle [constr] CenterX=11.8 CenterY=-18.4 CenterZ=0 NormalX=0 NormalY=0 NormalZ=1 AngleXU=0 Radius=0.25
    g9: Circle [constr] CenterX=-5.8 CenterY=-20 CenterZ=0 NormalX=0 NormalY=0 NormalZ=1 AngleXU=0 Radius=0.25
    g10: LineSegment StartX=-5.1 StartY=-18.15 StartZ=0 EndX=-6.05 EndY=-18.15 EndZ=0
    g11: LineSegment StartX=11.1 StartY=-20.25 StartZ=0 EndX=12.05 EndY=-20.25 EndZ=0
    g12: LineSegment StartX=-5.1 StartY=-20.25 StartZ=0 EndX=-5.1 EndY=-22.5 EndZ=0
    g13: LineSegment StartX=11.1 StartY=-18.15 StartZ=0 EndX=11.1 EndY=-0.7 EndZ=0
  constraints (42):
    c: Coincident(g12,g1)
    c: Coincident(g1,g2)
    c: Coincident(g13,g3)
    c: Coincident(g3,g0)
    c: Vertical(g0)
    c: Vertical(g2)
    c: Horizontal(g1)
    c: Horizontal(g3)
    c: Coincident(g4,g5)
    c: Coincident(g11,g6)
    c: Coincident(g6,g7)
    c: Coincident(g10,g4)
    c: Vertical(g4)
    c: Vertical(g6)
    c: Horizontal(g5)
    c: Horizontal(g7)
    c: DistanceX(g-5,g13) = 0.5
    c: DistanceX(g0,g-5) = 0.5
    c: DistanceY(g-5,g0) = 2
    c: Coincident(g8,g-3)
    c: Coincident(g9,g-4)
    c: Tangent(g5,g9)
    c: Tangent(g9,g4)
    c: Tangent(g8,g6)
    c: Tangent(g8,g7)
    c: DistanceX(g8,g6) = 0.25
    c: Equal(g8,g9)
    c: PointOnObject(g7,g13)
    c: Coincident(g0,g10)
    c: PointOnObject(g5,g12)
    c: PointOnObject(g12,g5)
    c: DistanceY(g1,g-4) = 2.5
    c: PointOnObject(g13,g7)
    c: Coincident(g2,g11)
    c: PointOnObject(g0,g7)
    c: PointOnObject(g5,g11)
    c: PointOnObject(g5,g0)
    c: Vertical(g12)
    c: Horizontal(g10)
    c: Vertical(g13)
    c: Horizontal(g11)
    c: PointOnObject(g2,g13)
FEATURE [Sketcher::SketchObject] Sketch109  label="sk ULN2003 slot"
  ArcFitTolerance = 1e-06
  AttachmentSupport = -> [XZ_Plane021]
  ExternalGeometry = -> [Binder006]
  FullyConstrained = true
  MakeInternals = false
  MapMode = 5
  Placement = pos=(0,0,0) rot=(1,0,0;1.5708rad)
  sketch-geometry (14):
    g0: Circle [constr] CenterX=17.35 CenterY=-39.2 CenterZ=0 NormalX=0 NormalY=0 NormalZ=1 AngleXU=0 Radius=0.125
    g1: Circle [constr] CenterX=-17.35 CenterY=-41 CenterZ=0 NormalX=0 NormalY=0 NormalZ=1 AngleXU=0 Radius=0.125
    g2: LineSegment StartX=-17.475 StartY=-39.075 StartZ=0 EndX=-17.475 EndY=-41.125 EndZ=0
    g3: LineSegment StartX=-17.475 StartY=-41.125 StartZ=0 EndX=-15.975 EndY=-41.125 EndZ=0
    g4: LineSegment StartX=17.475 StartY=-41.125 StartZ=0 EndX=17.475 EndY=-39.075 EndZ=0
    g5: LineSegment StartX=17.475 StartY=-39.075 StartZ=0 EndX=15.975 EndY=-39.075 EndZ=0
    g6: LineSegment StartX=15.975 StartY=-25.4 StartZ=0 EndX=-15.975 EndY=-25.4 EndZ=0
    g7: LineSegment StartX=-15.975 StartY=-25.4 StartZ=0 EndX=-15.975 EndY=-39.075 EndZ=0
    g8: LineSegment StartX=-15.975 StartY=-43.625 StartZ=0 EndX=15.975 EndY=-43.625 EndZ=0
    g9: LineSegment StartX=15.975 StartY=-43.625 StartZ=0 EndX=15.975 EndY=-41.125 EndZ=0
    g10: LineSegment StartX=-15.975 StartY=-39.075 StartZ=0 EndX=-17.475 EndY=-39.075 EndZ=0
    g11: LineSegment StartX=-15.975 StartY=-41.125 StartZ=0 EndX=-15.975 EndY=-43.625 EndZ=0
    g12: LineSegment StartX=15.975 StartY=-39.075 StartZ=0 EndX=15.975 EndY=-25.4 EndZ=0
    g13: LineSegment StartX=15.975 StartY=-41.125 StartZ=0 EndX=17.475 EndY=-41.125 EndZ=0
  constraints (42):
    c: Coincident(g0,g-3)
    c: Coincident(g1,g-4)
    c: Coincident(g2,g3)
    c: Coincident(g13,g4)
    c: Coincident(g4,g5)
    c: Coincident(g10,g2)
    c: Vertical(g2)
    c: Vertical(g4)
    c: Horizontal(g3)
    c: Horizontal(g5)
    c: Tangent(g0,g4)
    c: Tangent(g0,g5)
    c: Tangent(g1,g3)
    c: Tangent(g1,g2)
    c: Diameter(g0) = 0.25
    c: Coincident(g6,g7)
    c: Coincident(g11,g8)
    c: Coincident(g8,g9)
    c: Coincident(g12,g6)
    c: Horizontal(g6)
    c: Horizontal(g8)
    c: Vertical(g7)
    c: Vertical(g9)
    c: PointOnObject(g5,g12)
    c: Coincident(g7,g10)
    c: PointOnObject(g12,g5)
    c: PointOnObject(g9,g13)
    c: Coincident(g3,g11)
    c: PointOnObject(g13,g9)
    c: Equal(g0,g1)
    c: Vertical(g11)
    c: PointOnObject(g3,g7)
    c: Horizontal(g10)
    c: PointOnObject(g7,g5)
    c: Horizontal(g13)
    c: PointOnObject(g4,g3)
    c: PointOnObject(g9,g12)
    c: Vertical(g12)
    c: Distance(g5,g5) = 1.5
    c: Equal(g10,g5)
    c: DistanceY(g9,g9) = 2.5
    c: Distance(g-5,g6) = 2
FEATURE [Sketcher::SketchObject] Sketch110  label="sk separation"
  ArcFitTolerance = 1e-06
  AttachmentSupport = -> [YZ_Plane022]
  ExternalGeometry = -> [Sketch106]
  FullyConstrained = true
  MakeInternals = false
  MapMode = 5
  Placement = pos=(0,0,0) rot=(0.57735,0.57735,0.57735;2.0944rad)
  sketch-geometry (6):
    g0: LineSegment StartX=15.85 StartY=0 StartZ=0 EndX=15.85 EndY=-58 EndZ=0
    g1: LineSegment StartX=15.85 StartY=-58 StartZ=0 EndX=16.15 EndY=-58 EndZ=0
    g2: LineSegment StartX=16.15 StartY=-58 StartZ=0 EndX=16.15 EndY=0 EndZ=0
    g3: LineSegment StartX=16.15 StartY=0 StartZ=0 EndX=15.85 EndY=0 EndZ=0
    g4: GeomPoint X=16 Y=0 Z=0
    g5: LineSegment StartX=16 StartY=0 StartZ=0 EndX=16 EndY=-58 EndZ=0
  constraints (16):
    c: Coincident(g0,g1)
    c: Coincident(g1,g2)
    c: Coincident(g2,g3)
    c: Coincident(g3,g0)
    c: Vertical(g0)
    c: Vertical(g2)
    c: Horizontal(g1)
    c: Horizontal(g3)
    c: PointOnObject(g0,g-1)
    c: Distance(g3,g3) = 0.3
    c: Symmetric(g0,g2,g4)
    c: DistanceX(g-1,g4) = 16
    c: PointOnObject(g0,g-3)
    c: Coincident(g5,g4)
    c: PointOnObject(g5,g1)
    c: Vertical(g5)
FEATURE [Sketcher::SketchObject] Sketch111  label="sk ULN2003 slot depth"
  ArcFitTolerance = 1e-06
  AttachmentSupport = -> [YZ_Plane022]
  ExternalGeometry = -> [Sketch109,Sketch110]
  FullyConstrained = true
  MakeInternals = false
  MapMode = 5
  Placement = pos=(0,0,0) rot=(0.57735,0.57735,0.57735;2.0944rad)
  sketch-geometry (3):
    g0: LineSegment StartX=-23.5 StartY=-41.125 StartZ=0 EndX=16 EndY=-41.125 EndZ=0
    g1: GeomPoint X=15.85 Y=-41.125 Z=0
    g2: GeomPoint X=16.15 Y=-41.125 Z=0
  constraints (7):
    c: Horizontal(g0)
    c: PointOnObject(g-3,g0)
    c: PointOnObject(g1,g-5)
    c: PointOnObject(g2,g-6)
    c: Symmetric(g1,g2,g0)
    c: PointOnObject(g1,g0)
    c: DistanceX(g0,g0) = 39.5
FEATURE [Sketcher::SketchObject] Sketch112  label="sk relay slot depth"
  ArcFitTolerance = 1e-06
  AttachmentSupport = -> [YZ_Plane022]
  ExternalGeometry = -> [Sketch108,Sketch110]
  FullyConstrained = true
  MakeInternals = false
  MapMode = 5
  Placement = pos=(0,0,0) rot=(0.57735,0.57735,0.57735;2.0944rad)
  sketch-geometry (3):
    g0: LineSegment StartX=-28.5 StartY=-20.25 StartZ=0 EndX=16 EndY=-20.25 EndZ=0
    g1: GeomPoint X=15.85 Y=-20.25 Z=0
    g2: GeomPoint X=16.15 Y=-20.25 Z=0
  constraints (7):
    c: Horizontal(g0)
    c: PointOnObject(g-3,g0)
    c: PointOnObject(g1,g-4)
    c: PointOnObject(g2,g-5)
    c: Symmetric(g1,g2,g0)
    c: PointOnObject(g1,g0)
    c: DistanceX(g0,g-1) = 28.5
FEATURE [PartDesign::SubShapeBinder] Binder009  label="hs ref front"
  BindCopyOnChange = 0
  BindMode = 0
  ClaimChildren = false
  Context = -> Body022 [Binder009.]
  Fuse = false
  MakeFace = true
  OffsetFill = false
  OffsetIntersection = false
  OffsetJoinType = 0
  OffsetOpenResult = false
  PartialLoad = false
  Refine = true
  Relative = true
  Support = -> [Body021[Sketch107.]]
  _Version = 2
FEATURE [PartDesign::SubShapeBinder] Binder010  label="hs ref right"
  BindCopyOnChange = 0
  BindMode = 0
  ClaimChildren = false
  Context = -> Body022 [Binder010.]
  Fuse = false
  MakeFace = true
  OffsetFill = false
  OffsetIntersection = false
  OffsetJoinType = 0
  OffsetOpenResult = false
  PartialLoad = false
  Refine = true
  Relative = true
  Support = -> [Body021[Sketch106.]]
  _Version = 2
FEATURE [PartDesign::SubShapeBinder] Binder011  label="hr ref relay slot"
  BindCopyOnChange = 0
  BindMode = 0
  ClaimChildren = false
  Context = -> Body022 [Binder011.]
  Fuse = false
  MakeFace = true
  OffsetFill = false
  OffsetIntersection = false
  OffsetJoinType = 0
  OffsetOpenResult = false
  PartialLoad = false
  Refine = true
  Relative = true
  Support = -> [Body021[Sketch108.]]
  _Version = 2
FEATURE [PartDesign::SubShapeBinder] Binder012  label="hs ref separation"
  BindCopyOnChange = 0
  BindMode = 0
  ClaimChildren = false
  Context = -> Body022 [Binder012.]
  Fuse = false
  MakeFace = true
  OffsetFill = false
  OffsetIntersection = false
  OffsetJoinType = 0
  OffsetOpenResult = false
  PartialLoad = false
  Refine = true
  Relative = true
  Support = -> [Body021[Sketch110.]]
  _Version = 2
FEATURE [PartDesign::SubShapeBinder] Binder014  label="hs ref depth ULN 2003 slot"
  BindCopyOnChange = 0
  BindMode = 0
  ClaimChildren = false
  Context = -> Body022 [Binder014.]
  Fuse = false
  MakeFace = true
  OffsetFill = false
  OffsetIntersection = false
  OffsetJoinType = 0
  OffsetOpenResult = false
  PartialLoad = false
  Refine = true
  Relative = true
  Support = -> [Body021[Sketch111.]]
  _Version = 2
FEATURE [PartDesign::SubShapeBinder] Binder015  label="hs ref depth relay slot"
  BindCopyOnChange = 0
  BindMode = 0
  ClaimChildren = false
  Context = -> Body022 [Binder015.]
  Fuse = false
  MakeFace = true
  OffsetFill = false
  OffsetIntersection = false
  OffsetJoinType = 0
  OffsetOpenResult = false
  PartialLoad = false
  Refine = true
  Relative = true
  Support = -> [Body021[Sketch112.]]
  _Version = 2
FEATURE [PartDesign::SubShapeBinder] Binder016  label="hs ref cable"
  BindCopyOnChange = 0
  BindMode = 0
  ClaimChildren = false
  Context = -> Body022 [Binder016.]
  Fuse = false
  MakeFace = true
  OffsetFill = false
  OffsetIntersection = false
  OffsetJoinType = 0
  OffsetOpenResult = false
  PartialLoad = false
  Refine = true
  Relative = true
  Support = -> [Body021[Binder008.]]
  _Version = 2
FEATURE [Sketcher::SketchObject] Sketch113  label="sk slot ESP"
  ArcFitTolerance = 1e-06
  AttachmentSupport = -> [XZ_Plane021]
  ExternalGeometry = -> [Binder007]
  FullyConstrained = true
  MakeInternals = false
  MapMode = 5
  Placement = pos=(0,0,0) rot=(1,0,0;1.5708rad)
  sketch-geometry (15):
    g0: Circle [constr] CenterX=-15.5 CenterY=-53 CenterZ=0 NormalX=0 NormalY=0 NormalZ=1 AngleXU=0 Radius=0.25
    g1: Circle [constr] CenterX=15.5 CenterY=-52 CenterZ=0 NormalX=0 NormalY=0 NormalZ=1 AngleXU=0 Radius=0.25
    g2: LineSegment StartX=-15.75 StartY=-53.25 StartZ=0 EndX=-14.55 EndY=-53.25 EndZ=0
    g3: LineSegment StartX=15.75 StartY=-53.25 StartZ=0 EndX=15.75 EndY=-51.75 EndZ=0
    g4: LineSegment StartX=15.75 StartY=-51.75 StartZ=0 EndX=14.55 EndY=-51.75 EndZ=0
    g5: LineSegment StartX=-15.75 StartY=-51.75 StartZ=0 EndX=-15.75 EndY=-53.25 EndZ=0
    g6: LineSegment StartX=-14.55 StartY=-47.5 StartZ=0 EndX=-14.55 EndY=-51.75 EndZ=0
    g7: LineSegment StartX=-14.55 StartY=-55.25 StartZ=0 EndX=14.55 EndY=-55.25 EndZ=0
    g8: LineSegment StartX=14.55 StartY=-55.25 StartZ=0 EndX=14.55 EndY=-53.25 EndZ=0
    g9: LineSegment StartX=14.55 StartY=-47.5 StartZ=0 EndX=-14.55 EndY=-47.5 EndZ=0
    g10: LineSegment StartX=-14.55 StartY=-53.25 StartZ=0 EndX=-14.55 EndY=-55.25 EndZ=0
    g11: LineSegment StartX=-14.55 StartY=-51.75 StartZ=0 EndX=-15.75 EndY=-51.75 EndZ=0
    g12: LineSegment StartX=14.55 StartY=-53.25 StartZ=0 EndX=15.75 EndY=-53.25 EndZ=0
    g13: LineSegment StartX=14.55 StartY=-51.75 StartZ=0 EndX=14.55 EndY=-47.5 EndZ=0
    g14: Circle CenterX=11.9712 CenterY=-47.751 CenterZ=0 NormalX=0 NormalY=0 NormalZ=1 AngleXU=0 Radius=4.25
  constraints (44):
    c: Coincident(g0,g-3)
    c: Coincident(g1,g-4)
    c: Equal(g1,g0)
    c: Radius(g1) = 0.25
    c: Coincident(g12,g3)
    c: Coincident(g3,g4)
    c: Coincident(g11,g5)
    c: Coincident(g5,g2)
    c: Horizontal(g2)
    c: Horizontal(g4)
    c: Vertical(g3)
    c: Vertical(g5)
    c: Tangent(g1,g4)
    c: Tangent(g1,g3)
    c: Tangent(g0,g5)
    c: Tangent(g0,g2)
    c: Coincident(g10,g7)
    c: Coincident(g7,g8)
    c: Coincident(g13,g9)
    c: Coincident(g9,g6)
    c: Vertical(g6)
    c: Vertical(g8)
    c: Horizontal(g7)
    c: Horizontal(g9)
    c: PointOnObject(g6,g11)
    c: PointOnObject(g4,g13)
    c: PointOnObject(g11,g6)
    c: Coincident(g2,g10)
    c: Coincident(g8,g12)
    c: PointOnObject(g13,g4)
    c: Distance(g4,g4) = 1.2
    c: Vertical(g13)
    c: PointOnObject(g8,g13)
    c: Equal(g11,g4)
    c: PointOnObject(g2,g6)
    c: Vertical(g10)
    c: DistanceY(g8,g8) = 2
    c: Horizontal(g12)
    c: PointOnObject(g3,g2)
    c: Horizontal(g11)
    c: PointOnObject(g6,g4)
    c: DistanceY(g-3,g6) = 4.5
    c: Coincident(g14,g-5)
    c: Equal(g-5,g14)
FEATURE [PartDesign::SubShapeBinder] Binder017  label="sk ref USB"
  BindCopyOnChange = 0
  BindMode = 0
  ClaimChildren = false
  Context = -> Body021 [Binder017.]
  Fuse = false
  MakeFace = true
  OffsetFill = false
  OffsetIntersection = false
  OffsetJoinType = 0
  OffsetOpenResult = false
  PartialLoad = false
  Refine = true
  Relative = true
  Support = -> [Compound004[Edge4865,Edge4871,Edge4862,Edge4938,Edge4639,Edge4948,Edge4904,Edge4901]]
  _Version = 2
FEATURE [Sketcher::SketchObject] Sketch114  label="sk USB"
  ArcFitTolerance = 1e-06
  AttachmentSupport = -> [XZ_Plane021]
  ExternalGeometry = -> [Binder017]
  FullyConstrained = true
  MakeInternals = false
  MapMode = 5
  Placement = pos=(0,0,0) rot=(1,0,0;1.5708rad)
  sketch-geometry (12):
    g0: ArcOfCircle CenterX=-3.4 CenterY=-50.02 CenterZ=0 NormalX=0 NormalY=0 NormalZ=1 AngleXU=0 Radius=0.83581 StartAngle=1.5708 EndAngle=3.14159
    g1: ArcOfCircle CenterX=-3.4 CenterY=-50.7386 CenterZ=0 NormalX=0 NormalY=0 NormalZ=1 AngleXU=0 Radius=0.83581 StartAngle=3.14159 EndAngle=3.92699
    g2: ArcOfCircle CenterX=-2.86863 CenterY=-51.27 CenterZ=0 NormalX=0 NormalY=0 NormalZ=1 AngleXU=0 Radius=0.83581 StartAngle=3.92699 EndAngle=4.71239
    g3: ArcOfCircle CenterX=2.36863 CenterY=-51.27 CenterZ=0 NormalX=0 NormalY=0 NormalZ=1 AngleXU=0 Radius=0.83581 StartAngle=4.71239 EndAngle=5.49779
    g4: ArcOfCircle CenterX=2.9 CenterY=-50.7386 CenterZ=0 NormalX=0 NormalY=0 NormalZ=1 AngleXU=0 Radius=0.83581 StartAngle=5.49779 EndAngle=6.28319
    g5: ArcOfCircle CenterX=2.9 CenterY=-50.02 CenterZ=0 NormalX=0 NormalY=0 NormalZ=1 AngleXU=0 Radius=0.83581 StartAngle=1.7e-15 EndAngle=1.5708
    g6: LineSegment StartX=2.9 StartY=-49.1842 StartZ=0 EndX=-3.4 EndY=-49.1842 EndZ=0
    g7: LineSegment StartX=-4.23581 StartY=-50.02 StartZ=0 EndX=-4.23581 EndY=-50.7386 EndZ=0
    g8: LineSegment StartX=-3.99101 StartY=-51.3296 StartZ=0 EndX=-3.45964 EndY=-51.861 EndZ=0
    g9: LineSegment StartX=-2.86863 StartY=-52.1058 StartZ=0 EndX=2.36863 EndY=-52.1058 EndZ=0
    g10: LineSegment StartX=2.95964 StartY=-51.861 StartZ=0 EndX=3.49101 EndY=-51.3296 EndZ=0
    g11: LineSegment StartX=3.73581 StartY=-50.7386 StartZ=0 EndX=3.73581 EndY=-50.02 EndZ=0
  constraints (24):
    c: Coincident(g0,g-3)
    c: Coincident(g1,g-4)
    c: Coincident(g2,g-5)
    c: Coincident(g3,g-6)
    c: Coincident(g4,g-7)
    c: Coincident(g5,g-8)
    c: Horizontal(g6)
    c: Vertical(g7)
    c: Horizontal(g9)
    c: Vertical(g11)
    c: Tangent(g5,g6) = -1.5708
    c: Tangent(g0,g6) = -1.5708
    c: Tangent(g0,g7) = -1.5708
    c: Tangent(g1,g7) = -1.5708
    c: Tangent(g1,g8) = -1.5708
    c: Tangent(g2,g8) = -1.5708
    c: Tangent(g2,g9) = -1.5708
    c: Tangent(g3,g9) = -1.5708
    c: Tangent(g3,g10) = -1.5708
    c: Tangent(g4,g10) = -1.5708
    c: Tangent(g4,g11) = -1.5708
    c: Tangent(g5,g11) = -1.5708
    c: Parallel(g10,g-9)
    c: Distance(g-10,g6) = 0.1
FEATURE [PartDesign::SubShapeBinder] Binder018  label="hs ref USB"
  BindCopyOnChange = 0
  BindMode = 0
  ClaimChildren = false
  Context = -> Body022 [Binder018.]
  Fuse = false
  MakeFace = true
  OffsetFill = false
  OffsetIntersection = false
  OffsetJoinType = 0
  OffsetOpenResult = false
  PartialLoad = false
  Refine = true
  Relative = true
  Support = -> [Body021[Sketch114.]]
  _Version = 2
FEATURE [Sketcher::SketchObject] Sketch115  label="sk ESP slot depth"
  ArcFitTolerance = 1e-06
  AttachmentSupport = -> [YZ_Plane022]
  ExternalGeometry = -> [Binder008,Sketch113,Binder007]
  FullyConstrained = true
  MakeInternals = false
  MapMode = 5
  Placement = pos=(0,0,0) rot=(0.57735,0.57735,0.57735;2.0944rad)
  sketch-geometry (1):
    g0: LineSegment StartX=9.45 StartY=-55.25 StartZ=0 EndX=-29.65 EndY=-55.25 EndZ=0
  constraints (4):
    c: Horizontal(g0)
    c: PointOnObject(g-4,g0)
    c: Distance(g0,g-5) = 0.25
    c: Distance(g0,g-6) = 0.35
FEATURE [Sketcher::SketchObject] Sketch116  label="sk wall socket interface"
  ArcFitTolerance = 1e-06
  AttachmentSupport = -> [XY_Plane021]
  ExternalGeometry = -> [Binder003]
  FullyConstrained = true
  MakeInternals = false
  MapMode = 5
  sketch-geometry (20):
    g0: LineSegment StartX=-22.6 StartY=-28.15 StartZ=0 EndX=22.6 EndY=-28.15 EndZ=0
    g1: LineSegment StartX=28.15 StartY=-22.6 StartZ=0 EndX=28.15 EndY=22.6 EndZ=0
    g2: LineSegment StartX=22.6 StartY=28.15 StartZ=0 EndX=-22.6 EndY=28.15 EndZ=0
    g3: LineSegment StartX=-28.15 StartY=22.6 StartZ=0 EndX=-28.15 EndY=-22.6 EndZ=0
    g4: ArcOfCircle CenterX=-22.6 CenterY=-22.6 CenterZ=0 NormalX=0 NormalY=0 NormalZ=1 AngleXU=0 Radius=5.55 StartAngle=3.14159 EndAngle=4.71239
    g5: ArcOfCircle CenterX=22.6 CenterY=-22.6 CenterZ=0 NormalX=0 NormalY=0 NormalZ=1 AngleXU=0 Radius=5.55 StartAngle=4.71239 EndAngle=6.28319
    g6: ArcOfCircle CenterX=22.6 CenterY=22.6 CenterZ=0 NormalX=0 NormalY=0 NormalZ=1 AngleXU=0 Radius=5.55 StartAngle=1e-16 EndAngle=1.5708
    g7: ArcOfCircle CenterX=-22.6 CenterY=22.6 CenterZ=0 NormalX=0 NormalY=0 NormalZ=1 AngleXU=0 Radius=5.55 StartAngle=1.5708 EndAngle=3.14159
    g8: GeomPoint [constr] X=-28.15 Y=-28.15 Z=0
    g9: GeomPoint [constr] X=28.15 Y=28.15 Z=0
    g10: LineSegment StartX=-22.6 StartY=-30.6 StartZ=0 EndX=22.6 EndY=-30.6 EndZ=0
    g11: LineSegment StartX=30.6 StartY=-22.6 StartZ=0 EndX=30.6 EndY=22.6 EndZ=0
    g12: LineSegment StartX=22.6 StartY=30.6 StartZ=0 EndX=-22.6 EndY=30.6 EndZ=0
    g13: LineSegment StartX=-30.6 StartY=22.6 StartZ=0 EndX=-30.6 EndY=-22.6 EndZ=0
    g14: ArcOfCircle CenterX=-22.6 CenterY=-22.6 CenterZ=0 NormalX=0 NormalY=0 NormalZ=1 AngleXU=0 Radius=8 StartAngle=3.14159 EndAngle=4.71239
    g15: ArcOfCircle CenterX=22.6 CenterY=-22.6 CenterZ=0 NormalX=0 NormalY=0 NormalZ=1 AngleXU=0 Radius=8 StartAngle=4.71239 EndAngle=6.28319
    g16: ArcOfCircle CenterX=22.6 CenterY=22.6 CenterZ=0 NormalX=0 NormalY=0 NormalZ=1 AngleXU=0 Radius=8 StartAngle=2e-16 EndAngle=1.5708
    g17: ArcOfCircle CenterX=-22.6 CenterY=22.6 CenterZ=0 NormalX=0 NormalY=0 NormalZ=1 AngleXU=0 Radius=8 StartAngle=1.5708 EndAngle=3.14159
    g18: GeomPoint [constr] X=-30.6 Y=-30.6 Z=0
    g19: GeomPoint [constr] X=30.6 Y=30.6 Z=0
  constraints (45):
    c: Tangent(g0,g4) = -1.5708
    c: Tangent(g0,g5) = -1.5708
    c: Tangent(g1,g5) = -1.5708
    c: Tangent(g1,g6) = -1.5708
    c: Tangent(g2,g6) = -1.5708
    c: Tangent(g2,g7) = -1.5708
    c: Tangent(g3,g7) = -1.5708
    c: Tangent(g3,g4) = -1.5708
    c: Horizontal(g0)
    c: Horizontal(g2)
    c: Vertical(g1)
    c: Vertical(g3)
    c: Equal(g4,g5)
    c: Equal(g5,g6)
    c: Equal(g6,g7)
    c: PointOnObject(g8,g0)
    c: PointOnObject(g8,g3)
    c: PointOnObject(g9,g1)
    c: PointOnObject(g9,g2)
    c: Tangent(g10,g14) = -1.5708
    c: Tangent(g10,g15) = -1.5708
    c: Tangent(g11,g15) = -1.5708
    c: Tangent(g11,g16) = -1.5708
    c: Tangent(g12,g16) = -1.5708
    c: Tangent(g12,g17) = -1.5708
    c: Tangent(g13,g17) = -1.5708
    c: Tangent(g13,g14) = -1.5708
    c: Horizontal(g10)
    c: Horizontal(g12)
    c: Vertical(g11)
    c: Vertical(g13)
    c: Equal(g14,g15)
    c: Equal(g15,g16)
    c: Equal(g16,g17)
    c: PointOnObject(g18,g10)
    c: PointOnObject(g18,g13)
    c: PointOnObject(g19,g11)
    c: PointOnObject(g19,g12)
    c: Coincident(g6,g16)
    c: Coincident(g6,g-6)
    c: Coincident(g4,g14)
    c: Coincident(g4,g-4)
    c: Distance(g-5,g1) = 0.15
    c: Equal(g-6,g16)
    c: Radius(g16) = 8
FEATURE [PartDesign::SubShapeBinder] Binder019  label="hs ref ESP slot"
  BindCopyOnChange = 0
  BindMode = 0
  ClaimChildren = false
  Context = -> Body022 [Binder019.]
  Fuse = false
  MakeFace = true
  OffsetFill = false
  OffsetIntersection = false
  OffsetJoinType = 0
  OffsetOpenResult = false
  PartialLoad = false
  Refine = true
  Relative = true
  Support = -> [Body021[Sketch113.]]
  _Version = 2
FEATURE [PartDesign::SubShapeBinder] Binder020  label="hs ref ESP slot depth"
  BindCopyOnChange = 0
  BindMode = 0
  ClaimChildren = false
  Context = -> Body022 [Binder020.]
  Fuse = false
  MakeFace = true
  OffsetFill = false
  OffsetIntersection = false
  OffsetJoinType = 0
  OffsetOpenResult = false
  PartialLoad = false
  Refine = true
  Relative = true
  Support = -> [Body021[Sketch115.]]
  _Version = 2
FEATURE [PartDesign::SubShapeBinder] Binder021  label="hs ref wall socket interface"
  BindCopyOnChange = 0
  BindMode = 0
  ClaimChildren = false
  Context = -> Body022 [Binder021.]
  Fuse = false
  MakeFace = true
  OffsetFill = false
  OffsetIntersection = false
  OffsetJoinType = 0
  OffsetOpenResult = false
  PartialLoad = false
  Refine = true
  Relative = true
  Support = -> [Body021[Sketch116.]]
  _Version = 2
FEATURE [PartDesign::Plane] DatumPlane004  label="hs pln rear"
  AttachmentSupport = -> [Binder009,YZ_Plane023]
  Length = 97.2543
  MapMode = 6
  Placement = pos=(-30.6,0,0) rot=(0,1,0;1.5708rad)
  ResizeMode = 0
  Width = 75.4543
FEATURE [PartDesign::Plane] DatumPlane005  label="hs pln front"
  AttachmentSupport = -> [Binder009,YZ_Plane023]
  Length = 97.2543
  MapMode = 6
  Placement = pos=(30.6,0,0) rot=(0,1,0;1.5708rad)
  ResizeMode = 0
  Width = 75.4543
FEATURE [Sketcher::SketchObject] Sketch117  label="hs base"
  ArcFitTolerance = 1e-06
  AttachmentSupport = -> [DatumPlane005]
  ExternalGeometry = -> [Binder010]
  FullyConstrained = true
  MakeInternals = false
  MapMode = 5
  Placement = pos=(30.6,0,0) rot=(0,1,0;1.5708rad)
  sketch-geometry (5):
    g0: LineSegment StartX=-1.5 StartY=30.6 StartZ=0 EndX=-1.5 EndY=-30.6 EndZ=0
    g1: LineSegment StartX=-1.5 StartY=-30.6 StartZ=0 EndX=58 EndY=-30.6 EndZ=0
    g2: LineSegment StartX=58 StartY=-30.6 StartZ=0 EndX=58 EndY=18 EndZ=0
    g3: LineSegment StartX=20 StartY=30.6 StartZ=0 EndX=-1.5 EndY=30.6 EndZ=0
    g4: ArcOfCircle CenterX=20 CenterY=-33.0016 CenterZ=0 NormalX=0 NormalY=0 NormalZ=1 AngleXU=0 Radius=63.6016 StartAngle=0.930455 EndAngle=1.5708
  constraints (13):
    c: Coincident(g0,g1)
    c: Coincident(g1,g2)
    c: Coincident(g3,g0)
    c: Vertical(g0)
    c: Horizontal(g1)
    c: Horizontal(g3)
    c: Coincident(g1,g-4)
    c: PointOnObject(g-5,g3)
    c: PointOnObject(g-3,g0)
    c: Tangent(g3,g4) = -1.5708
    c: Coincident(g2,g4)
    c: Coincident(g2,g-6)
    c: Equal(g-6,g4)
FEATURE [PartDesign::Pad] Pad022  label="HS Base"
  Direction = (1,0,2e-16)
  Length = 10
  Length2 = 10
  Placement = pos=(30.6,0,0) rot=(0,1,0;1.5708rad)
  Profile = -> Sketch117
  ReferenceAxis = -> Sketch117 [N_Axis]
  Refine = true
  Suppressed = false
  Type = 3
  UpToFace = -> DatumPlane004
FEATURE [Sketcher::SketchObject] Sketch118  label="hs interface wall socket"
  ArcFitTolerance = 1e-06
  AttachmentSupport = -> [XY_Plane022]
  ExternalGeometry = -> [Binder021]
  FullyConstrained = true
  MakeInternals = false
  MapMode = 5
  sketch-geometry (11):
    g0: LineSegment StartX=-22.6 StartY=-28.15 StartZ=0 EndX=22.6 EndY=-28.15 EndZ=0
    g1: LineSegment StartX=28.15 StartY=-22.6 StartZ=0 EndX=28.15 EndY=22.6 EndZ=0
    g2: LineSegment StartX=22.6 StartY=28.15 StartZ=0 EndX=-22.6 EndY=28.15 EndZ=0
    g3: LineSegment StartX=-28.15 StartY=22.6 StartZ=0 EndX=-28.15 EndY=-22.6 EndZ=0
    g4: ArcOfCircle CenterX=-22.6 CenterY=-22.6 CenterZ=0 NormalX=0 NormalY=0 NormalZ=1 AngleXU=0 Radius=5.55 StartAngle=3.14159 EndAngle=4.71239
    g5: ArcOfCircle CenterX=22.6 CenterY=-22.6 CenterZ=0 NormalX=0 NormalY=0 NormalZ=1 AngleXU=0 Radius=5.55 StartAngle=4.71239 EndAngle=6.28319
    g6: ArcOfCircle CenterX=22.6 CenterY=22.6 CenterZ=0 NormalX=0 NormalY=0 NormalZ=1 AngleXU=0 Radius=5.55 StartAngle=3e-15 EndAngle=1.5708
    g7: ArcOfCircle CenterX=-22.6 CenterY=22.6 CenterZ=0 NormalX=0 NormalY=0 NormalZ=1 AngleXU=0 Radius=5.55 StartAngle=1.5708 EndAngle=3.14159
    g8: GeomPoint [constr] X=-28.15 Y=-28.15 Z=0
    g9: GeomPoint [constr] X=28.15 Y=28.15 Z=0
    g10: Circle CenterX=0 CenterY=0 CenterZ=0 NormalX=0 NormalY=0 NormalZ=1 AngleXU=0 Radius=50
  constraints (24):
    c: Tangent(g0,g4) = -1.5708
    c: Tangent(g0,g5) = -1.5708
    c: Tangent(g1,g5) = -1.5708
    c: Tangent(g1,g6) = -1.5708
    c: Tangent(g2,g6) = -1.5708
    c: Tangent(g2,g7) = -1.5708
    c: Tangent(g3,g7) = -1.5708
    c: Tangent(g3,g4) = -1.5708
    c: Horizontal(g0)
    c: Horizontal(g2)
    c: Vertical(g1)
    c: Vertical(g3)
    c: Equal(g4,g5)
    c: Equal(g5,g6)
    c: Equal(g6,g7)
    c: PointOnObject(g8,g0)
    c: PointOnObject(g8,g3)
    c: PointOnObject(g9,g1)
    c: PointOnObject(g9,g2)
    c: Coincident(g6,g-4)
    c: Coincident(g4,g-3)
    c: Equal(g-4,g6)
    c: Coincident(g10,g-1)
    c: Diameter(g10) = 100
FEATURE [PartDesign::Pocket] Pocket033  label="HS Interface wall socket"
  BaseFeature = -> Pad022
  Direction = (0,0,-1)
  Length = 5
  Length2 = 5
  Placement = pos=(30.6,0,0) rot=(0,1,0;1.5708rad)
  Profile = -> Sketch118
  ReferenceAxis = -> Sketch118 [N_Axis]
  Refine = true
  Reversed = true
  Suppressed = false
  Type = 1
FEATURE [Sketcher::SketchObject] Sketch119  label="screw core 001"
  ArcFitTolerance = 0
  AttachmentSupport = -> [XZ_Plane023]
  FullyConstrained = true
  MakeInternals = false
  MapMode = 5
  Placement = pos=(0,0,0) rot=(1,0,0;1.5708rad)
  sketch-geometry (5):
    g0: LineSegment StartX=0 StartY=0 StartZ=0 EndX=2.65 EndY=0 EndZ=0
    g1: LineSegment StartX=2.65 StartY=0 StartZ=0 EndX=1.1 EndY=-1.55 EndZ=0
    g2: LineSegment StartX=1.1 StartY=-1.55 StartZ=0 EndX=1.1 EndY=-14.0947 EndZ=0
    g3: LineSegment StartX=1.1 StartY=-14.0947 StartZ=0 EndX=0 EndY=-16 EndZ=0
    g4: LineSegment StartX=0 StartY=-16 StartZ=0 EndX=0 EndY=0 EndZ=0
  constraints (14):
    c: Coincident(g-1,g0)
    c: PointOnObject(g0,g-1)
    c: Coincident(g0,g1)
    c: Coincident(g1,g2)
    c: Vertical(g2)
    c: Coincident(g2,g3)
    c: PointOnObject(g3,g-2)
    c: Coincident(g3,g4)
    c: Coincident(g4,g0)
    c: DistanceX(g0,g0) = 2.65
    c: Angle(g0,g1) = 0.785398
    c: DistanceX(g1) = 1.1
    c: DistanceY(g4,g4) = 16
    c: Angle(g3,g4) = 0.523599
FEATURE [PartDesign::Revolution] Revolution  label="Screw core 001"
  Angle = 360
  Angle2 = 60
  Axis = (1e-16,1e-16,1)
  Base = (0,0,0)
  Placement = pos=(0,0,0) rot=(1,0,0;1.5708rad)
  Profile = -> Sketch119
  ReferenceAxis = -> Z_Axis023
  Reversed = true
  Suppressed = false
  Type = 0
FEATURE [Sketcher::SketchObject] Sketch001  label="screw helix 001"
  ArcFitTolerance = 0
  AttachmentSupport = -> [XZ_Plane023]
  ExternalGeometry = -> [Sketch119]
  FullyConstrained = true
  MakeInternals = false
  MapMode = 5
  Placement = pos=(0,0,0) rot=(1,0,0;1.5708rad)
  sketch-geometry (4):
    g0: LineSegment StartX=1.1 StartY=-1.05 StartZ=0 EndX=1.5 EndY=-1.3 EndZ=0
    g1: LineSegment StartX=1.5 StartY=-1.3 StartZ=0 EndX=1.1 EndY=-1.55 EndZ=0
    g2: LineSegment [constr] StartX=1.5 StartY=-1.3 StartZ=0 EndX=0.94375 EndY=-1.3 EndZ=0
    g3: ArcOfCircle CenterX=0.94375 CenterY=-1.3 CenterZ=0 NormalX=0 NormalY=0 NormalZ=1 AngleXU=0 Radius=0.294812 StartAngle=1.0122 EndAngle=5.27099
  constraints (10):
    c: Coincident(g0,g1)
    c: Coincident(g2,g0)
    c: Symmetric(g1,g0,g2)
    c: DistanceY(g1,g0) = 0.5
    c: Coincident(g1,g-3)
    c: Tangent(g3,g1) = 1.5708
    c: Tangent(g3,g0) = 1.5708
    c: DistanceX(g0) = 1.5
    c: Coincident(g2,g3)
    c: Horizontal(g2)
FEATURE [Sketcher::SketchObject] Sketch002  label="screw driver pocket 001"
  ArcFitTolerance = 0
  AttachmentSupport = -> [XZ_Plane023]
  ExternalGeometry = -> [Sketch119]
  FullyConstrained = true
  MakeInternals = false
  MapMode = 5
  Placement = pos=(0,0,0) rot=(1,0,0;1.5708rad)
  sketch-geometry (4):
    g0: LineSegment StartX=1.94289 StartY=0 StartZ=0 EndX=0.5 EndY=-1.44289 EndZ=0
    g1: LineSegment StartX=0.5 StartY=-1.44289 StartZ=0 EndX=-0.5 EndY=-1.44289 EndZ=0
    g2: LineSegment StartX=-0.5 StartY=-1.44289 StartZ=0 EndX=-1.94289 EndY=0 EndZ=0
    g3: LineSegment StartX=-1.94289 StartY=0 StartZ=0 EndX=1.94289 EndY=0 EndZ=0
  constraints (10):
    c: PointOnObject(g0,g-1)
    c: Coincident(g0,g1)
    c: Coincident(g1,g2)
    c: Coincident(g2,g3)
    c: Coincident(g3,g0)
    c: Symmetric(g0,g2,g-2)
    c: Symmetric(g0,g1,g-2)
    c: Parallel(g-3,g0)
    c: Distance(g-3,g0) = 0.5
    c: DistanceX(g1,g1) = 1
FEATURE [PartDesign::AdditiveHelix] AdditiveHelix  label="Screw helix 001"
  Angle = 0
  Axis = (0,2e-16,1)
  Base = (0,0,0)
  BaseFeature = -> Revolution
  Growth = 0
  HasBeenEdited = true
  Height = 8.5
  LeftHanded = false
  Mode = 0
  Outside = false
  Pitch = 1.2
  Placement = pos=(0,0,0) rot=(1,0,0;1.5708rad)
  Profile = -> Sketch001
  ReferenceAxis = -> Sketch001 [V_Axis]
  Reversed = true
  Suppressed = false
  Tolerance = 0.1
  Turns = 7.08333
FEATURE [PartDesign::Pocket] Pocket034  label="Screw driver pocket A 001"
  BaseFeature = -> AdditiveHelix
  Direction = (0,1,-2e-16)
  Length = 0.6
  Length2 = 5
  Midplane = true
  Placement = pos=(0,0,0) rot=(1,0,0;1.5708rad)
  Profile = -> Sketch002
  ReferenceAxis = -> Sketch002 [N_Axis]
  Suppressed = false
  Type = 0
FEATURE [PartDesign::PolarPattern] PolarPattern  label="Screw driver pocket B 001"
  Angle = 90
  Axis = -> Z_Axis023
  BaseFeature = -> Pocket034
  Mode = 0
  Occurrences = 2
  Offset = 120
  Originals = -> [Pocket034]
  Placement = pos=(0,0,0) rot=(1,0,0;1.5708rad)
  Suppressed = false
  TransformMode = 0
FEATURE [Sketcher::SketchObject] Sketch003  label="Screw hole 001"
  ArcFitTolerance = 0
  AttachmentSupport = -> [XZ_Plane023]
  ExternalGeometry = -> [Sketch119,Sketch001]
  FullyConstrained = true
  MakeInternals = false
  MapMode = 5
  Placement = pos=(0,0,0) rot=(1,0,0;1.5708rad)
  sketch-geometry (8):
    g0: LineSegment StartX=0 StartY=20 StartZ=0 EndX=3.35 EndY=20 EndZ=0
    g1: LineSegment StartX=3.35 StartY=20 StartZ=0 EndX=3.35 EndY=0.7 EndZ=0
    g2: LineSegment StartX=3.35 StartY=0.7 StartZ=0 EndX=1.7 EndY=-0.95 EndZ=0
    g3: LineSegment StartX=1.7 StartY=-0.95 StartZ=0 EndX=1.7 EndY=-3.5 EndZ=0
    g4: LineSegment StartX=1.7 StartY=-3.5 StartZ=0 EndX=1.25 EndY=-3.5 EndZ=0
    g5: LineSegment StartX=1.25 StartY=-3.5 StartZ=0 EndX=1.25 EndY=-15.0103 EndZ=0
    g6: LineSegment StartX=1.25 StartY=-15.0103 StartZ=0 EndX=0 EndY=-16.5 EndZ=0
    g7: LineSegment StartX=0 StartY=-16.5 StartZ=0 EndX=0 EndY=20 EndZ=0
  constraints (24):
    c: PointOnObject(g0,g-2)
    c: Horizontal(g0)
    c: Coincident(g0,g1)
    c: Coincident(g1,g2)
    c: Coincident(g2,g3)
    c: Vertical(g3)
    c: Coincident(g3,g4)
    c: Horizontal(g4)
    c: Coincident(g4,g5)
    c: Vertical(g5)
    c: Coincident(g5,g6)
    c: Coincident(g7,g0)
    c: Vertical(g1)
    c: PointOnObject(g-3,g2)
    c: Parallel(g2,g-3)
    c: DistanceX(g-4,g2) = 0.2
    c: DistanceX(g4,g-4) = 0.25
    c: DistanceY(g3,g-1) = 3.5
    c: DistanceY(g0) = 20
    c: DistanceX(g-3,g1) = 0.7
    c: Coincident(g6,g7)
    c: PointOnObject(g6,g-2)
    c: DistanceY(g6,g-5) = 0.5
    c: Angle(g6,g-5) = 0.174533
FEATURE [PartDesign::Body] Body023  label="Self tapping screw M3x16_001"
  AllowCompound = false
  Group = -> [Sketch119,Revolution,Sketch001,Sketch002,AdditiveHelix,Pocket034,PolarPattern,Sketch003]
  Origin = -> Origin023
  Placement = pos=(21,19.5,-44) rot=(1,0,0;4.71239rad)
  Tip = -> PolarPattern
FEATURE [PartDesign::Fillet] Fillet  label="HS Fillet"
  Base = -> Pocket033 [Edge29,Edge32,Edge36,Edge34]
  BaseFeature = -> Pocket033
  Placement = pos=(30.6,0,0) rot=(0,1,0;1.5708rad)
  Radius = 8
  Refine = true
  SupportTransform = false
  Suppressed = false
  UseAllEdges = false
FEATURE [PartDesign::Chamfer] Chamfer  label="HS Chamfer"
  Angle = 45
  Base = -> Fillet [Edge17]
  BaseFeature = -> Fillet
  ChamferType = 0
  FlipDirection = false
  Placement = pos=(30.6,0,0) rot=(0,1,0;1.5708rad)
  Refine = true
  Size = 2
  Size2 = 1
  SupportTransform = false
  Suppressed = false
  UseAllEdges = false
FEATURE [PartDesign::SubShapeBinder] Binder022  label="sk ref nut top"
  BindCopyOnChange = 0
  BindMode = 0
  ClaimChildren = false
  Context = -> Body021 [Binder022.]
  Fuse = false
  MakeFace = true
  OffsetFill = false
  OffsetIntersection = false
  OffsetJoinType = 0
  OffsetOpenResult = false
  PartialLoad = false
  Refine = true
  Relative = true
  Support = -> [Nut002[Face13,Face14,Face15,Face16]]
  _Version = 2
FEATURE [PartDesign::Point] DatumPoint002  label="sk pnt nut top"
  AttacherType = Attacher::AttachEnginePoint
  AttachmentSupport = -> [Binder004]
  MapMode = 36
  Placement = pos=(19,0,-5.8) rot=(0.57735,0.57735,-0.57735;4.18879rad)
FEATURE [PartDesign::Plane] DatumPlane006  label="sk pln nut top"
  AttachmentSupport = -> [DatumPoint002,XY_Plane021]
  Length = 60
  MapMode = 6
  Placement = pos=(19,0,-5.8) rot=(0,0,1;3.14159rad)
  ResizeMode = 0
  Width = 60
FEATURE [Sketcher::SketchObject] Sketch120  label="sk nut slot crs"
  ArcFitTolerance = 1e-06
  AttachmentSupport = -> [DatumPlane006]
  ExternalGeometry = -> [Binder022,Sketch110,DatumPoint002]
  FullyConstrained = true
  MakeInternals = false
  MapMode = 5
  Placement = pos=(19,0,-5.8) rot=(1,0,0;3.14159rad)
  sketch-geometry (9):
    g0: LineSegment StartX=-3.8 StartY=-16 StartZ=0 EndX=-3.8 EndY=2.19393 EndZ=0
    g1: LineSegment StartX=-3.8 StartY=2.19393 StartZ=0 EndX=3.1e-15 EndY=4.38786 EndZ=0
    g2: LineSegment StartX=3.1e-15 StartY=4.38786 StartZ=0 EndX=3.8 EndY=2.19393 EndZ=0
    g3: LineSegment StartX=3.8 StartY=2.19393 StartZ=0 EndX=3.8 EndY=-16 EndZ=0
    g4: LineSegment StartX=3.8 StartY=-16 StartZ=0 EndX=-3.8 EndY=-16 EndZ=0
    g5: Circle [constr] CenterX=3.5 CenterY=2.02073 CenterZ=0 NormalX=0 NormalY=0 NormalZ=1 AngleXU=0 Radius=0.3
    g6: Circle [constr] CenterX=3.6e-15 CenterY=4.04145 CenterZ=0 NormalX=0 NormalY=0 NormalZ=1 AngleXU=0 Radius=0.3
    g7: Circle [constr] CenterX=-3.5 CenterY=2.02073 CenterZ=0 NormalX=0 NormalY=0 NormalZ=1 AngleXU=0 Radius=0.3
    g8: Circle CenterX=0 CenterY=0 CenterZ=0 NormalX=0 NormalY=0 NormalZ=1 AngleXU=0 Radius=2.25
  constraints (22):
    c: Vertical(g0)
    c: Coincident(g0,g1)
    c: Coincident(g1,g2)
    c: Coincident(g2,g3)
    c: Vertical(g3)
    c: Coincident(g3,g4)
    c: Coincident(g4,g0)
    c: Coincident(g5,g-4)
    c: Coincident(g6,g-3)
    c: Coincident(g7,g-5)
    c: Equal(g7,g6)
    c: Equal(g6,g5)
    c: Tangent(g7,g0)
    c: Tangent(g7,g1)
    c: Tangent(g6,g1)
    c: Tangent(g6,g2)
    c: Tangent(g5,g2)
    c: Tangent(g5,g3)
    c: DistanceX(g0,g7) = 0.3
    c: Symmetric(g-7,g-6,g4)
    c: Coincident(g8,g-1)
    c: Diameter(g8) = 4.5
FEATURE [PartDesign::Plane] DatumPlane007  label="sk pln nut right"
  AttachmentSupport = -> [DatumPoint002,YZ_Plane022]
  Length = 95.8841
  MapMode = 6
  Placement = pos=(19,0,-5.8) rot=(0,1,0;1.5708rad)
  ResizeMode = 0
  Width = 62.8841
FEATURE [Sketcher::SketchObject] Sketch121  label="sk nut slot trj"
  ArcFitTolerance = 1e-06
  AttachmentSupport = -> [DatumPlane007]
  FullyConstrained = true
  MakeInternals = false
  MapMode = 5
  Placement = pos=(19,0,-5.8) rot=(0,1,0;1.5708rad)
  sketch-geometry (1):
    g0: LineSegment StartX=0 StartY=0 StartZ=0 EndX=3.4 EndY=0 EndZ=0
  constraints (3):
    c: Coincident(g0,g-1)
    c: PointOnObject(g0,g-1)
    c: Distance(g0,g0) = 3.4
FEATURE [PartDesign::Plane] DatumPlane008  label="sk pln separation"
  AttachmentSupport = -> [Sketch110,XZ_Plane021]
  Length = 95.8841
  MapMode = 6
  Placement = pos=(0,16,0) rot=(0.57735,-0.57735,0.57735;2.0944rad)
  ResizeMode = 0
  Width = 62.8841
FEATURE [Sketcher::SketchObject] Sketch122  label="sk separation trj"
  ArcFitTolerance = 1e-06
  AttachmentSupport = -> [DatumPlane008]
  ExternalGeometry = -> [Sketch107]
  FullyConstrained = true
  MakeInternals = false
  MapMode = 5
  Placement = pos=(0,16,0) rot=(0.57735,-0.57735,0.57735;2.0944rad)
  sketch-geometry (7):
    g0: LineSegment StartX=10 StartY=28.1 StartZ=0 EndX=-30 EndY=28.1 EndZ=0
    g1: LineSegment StartX=-55.5 StartY=21.2392 StartZ=0 EndX=-55.5 EndY=-21.2392 EndZ=0
    g2: LineSegment StartX=-30 StartY=-28.1 StartZ=0 EndX=10 EndY=-28.1 EndZ=0
    g3: ArcOfCircle CenterX=-51.5 CenterY=21.2392 CenterZ=0 NormalX=0 NormalY=0 NormalZ=1 AngleXU=0 Radius=4 StartAngle=1.83537 EndAngle=3.14159
    g4: ArcOfCircle CenterX=-51.5 CenterY=-21.2392 CenterZ=0 NormalX=0 NormalY=0 NormalZ=1 AngleXU=0 Radius=4 StartAngle=3.14159 EndAngle=4.44782
    g5: ArcOfCircle CenterX=-30 CenterY=-58.1201 CenterZ=0 NormalX=0 NormalY=0 NormalZ=1 AngleXU=0 Radius=86.2201 StartAngle=1.5708 EndAngle=1.83537
    g6: ArcOfCircle CenterX=-30 CenterY=58.1201 CenterZ=0 NormalX=0 NormalY=0 NormalZ=1 AngleXU=0 Radius=86.2201 StartAngle=4.44782 EndAngle=4.71239
  constraints (18):
    c: Tangent(g1,g3) = -1.5708
    c: Tangent(g1,g4) = -1.5708
    c: Horizontal(g0)
    c: Horizontal(g2)
    c: Vertical(g1)
    c: Equal(g3,g4)
    c: Tangent(g0,g5) = -1.5708
    c: DistanceX(g0,g-1) = 30
    c: Distance(g0,g-3) = 2.5
    c: Tangent(g3,g5) = -1.5708
    c: Tangent(g2,g6) = -1.5708
    c: Tangent(g4,g6) = -1.5708
    c: Distance(g3,g0) = 3
    c: Distance(g-3,g1) = 2.5
    c: Symmetric(g5,g6,g-1)
    c: Distance(g0,g-2) = 10
    c: Symmetric(g0,g2,g-1)
    c: Radius(g3) = 4
FEATURE [Sketcher::SketchObject] Sketch123  label="sk separation crs"
  ArcFitTolerance = 1e-06
  AttachmentSupport = -> [YZ_Plane022]
  ExternalGeometry = -> [Sketch110,Sketch122]
  FullyConstrained = true
  MakeInternals = false
  MapMode = 5
  Placement = pos=(0,0,0) rot=(0.57735,0.57735,0.57735;2.0944rad)
  sketch-geometry (9):
    g0: LineSegment [constr] StartX=15.85 StartY=-55.5 StartZ=0 EndX=17.35 EndY=-55.5 EndZ=0
    g1: LineSegment StartX=16.15 StartY=-54.5216 StartZ=0 EndX=17.35 EndY=-54.9 EndZ=0
    g2: LineSegment StartX=17.35 StartY=-54.9 StartZ=0 EndX=17.35 EndY=-56.1 EndZ=0
    g3: LineSegment StartX=17.35 StartY=-56.1 StartZ=0 EndX=16.15 EndY=-56.4784 EndZ=0
    g4: LineSegment StartX=15.85 StartY=-53.879 StartZ=0 EndX=17.4239 EndY=-54.7694 EndZ=0
    g5: LineSegment StartX=17.4239 StartY=-56.2306 StartZ=0 EndX=15.85 EndY=-57.121 EndZ=0
    g6: ArcOfCircle CenterX=17.0105 CenterY=-55.5 CenterZ=0 NormalX=0 NormalY=0 NormalZ=1 AngleXU=0 Radius=0.839373 StartAngle=5.22726 EndAngle=7.33911
    g7: GeomPoint [constr] X=18.7151 Y=-55.5 Z=0
    g8: LineSegment [constr] StartX=17.4239 StartY=-54.7694 StartZ=0 EndX=17.35 EndY=-54.9 EndZ=0
  constraints (24):
    c: Horizontal(g0)
    c: PointOnObject(g1,g-3)
    c: Coincident(g1,g2)
    c: Coincident(g2,g3)
    c: PointOnObject(g0,g2)
    c: DistanceY(g2,g2) = 1.2
    c: Symmetric(g1,g2,g0)
    c: Distance(g1,g-3) = 1.2
    c: Angle(g1,g3) = 0.610865
    c: Symmetric(g3,g1,g0)
    c: PointOnObject(g0,g-4)
    c: PointOnObject(g4,g-4)
    c: PointOnObject(g7,g4)
    c: PointOnObject(g7,g5)
    c: Tangent(g4,g6) = 1.5708
    c: Tangent(g5,g6) = 1.5708
    c: PointOnObject(g6,g0)
    c: Symmetric(g5,g4,g0)
    c: Distance(g1,g4) = 0.15
    c: Angle(g4,g1) = 0.20944
    c: Coincident(g8,g4)
    c: Coincident(g8,g1)
    c: PointOnObject(g6,g8)
    c: PointOnObject(g-5,g0)
FEATURE [PartDesign::Plane] DatumPlane009  label="hs pln relay slot"
  AttachmentSupport = -> [Binder015,XZ_Plane022]
  Length = 97.2543
  MapMode = 6
  Placement = pos=(0,-28.5,-20.25) rot=(0.57735,-0.57735,0.57735;2.0944rad)
  ResizeMode = 0
  Width = 75.4543
FEATURE [PartDesign::Plane] DatumPlane010  label="hs pln separation"
  AttachmentSupport = -> [Binder012,XZ_Plane022]
  Length = 97.2543
  MapMode = 6
  Placement = pos=(0,16,0) rot=(0.57735,-0.57735,0.57735;2.0944rad)
  ResizeMode = 0
  Width = 75.4543
FEATURE [Sketcher::SketchObject] Sketch124
  ArcFitTolerance = 1e-06
  AttachmentSupport = -> [DatumPlane009]
  ExternalGeometry = -> [Binder011]
  FullyConstrained = true
  MakeInternals = false
  MapMode = 5
  Placement = pos=(0,-28.5,-20.25) rot=(0.57735,-0.57735,0.57735;2.0944rad)
  sketch-geometry (12):
    g0: LineSegment StartX=1.42e-14 StartY=6.05 StartZ=0 EndX=0 EndY=5.1 EndZ=0
    g1: LineSegment StartX=0 StartY=5.1 StartZ=0 EndX=-2.25 EndY=5.1 EndZ=0
    g2: LineSegment StartX=-2.25 StartY=5.1 StartZ=0 EndX=-2.25 EndY=-11.1 EndZ=0
    g3: LineSegment StartX=-2.25 StartY=-11.1 StartZ=0 EndX=0 EndY=-11.1 EndZ=0
    g4: LineSegment StartX=0 StartY=-11.1 StartZ=0 EndX=0 EndY=-12.05 EndZ=0
    g5: LineSegment StartX=0 StartY=-12.05 StartZ=0 EndX=2.1 EndY=-12.05 EndZ=0
    g6: LineSegment StartX=2.1 StartY=-12.05 StartZ=0 EndX=2.1 EndY=-11.1 EndZ=0
    g7: LineSegment StartX=2.1 StartY=-11.1 StartZ=0 EndX=19.55 EndY=-11.1 EndZ=0
    g8: LineSegment StartX=19.55 StartY=-11.1 StartZ=0 EndX=19.55 EndY=5.1 EndZ=0
    g9: LineSegment StartX=19.55 StartY=5.1 StartZ=0 EndX=2.1 EndY=5.1 EndZ=0
    g10: LineSegment StartX=2.1 StartY=5.1 StartZ=0 EndX=2.1 EndY=6.05 EndZ=0
    g11: LineSegment StartX=2.1 StartY=6.05 StartZ=0 EndX=1.42e-14 EndY=6.05 EndZ=0
  constraints (28):
    c: Coincident(g-3,g0)
    c: PointOnObject(g0,g-2)
    c: Coincident(g0,g1)
    c: Coincident(g1,g-5)
    c: Horizontal(g1)
    c: Coincident(g1,g2)
    c: Coincident(g2,g-5)
    c: Coincident(g2,g3)
    c: PointOnObject(g3,g-2)
    c: Horizontal(g3)
    c: Coincident(g3,g4)
    c: Coincident(g4,g-6)
    c: Coincident(g4,g5)
    c: Coincident(g5,g-6)
    c: Coincident(g5,g6)
    c: Coincident(g6,g7)
    c: Coincident(g7,g-4)
    c: Horizontal(g7)
    c: Coincident(g7,g8)
    c: Coincident(g8,g-4)
    c: Coincident(g8,g9)
    c: Horizontal(g9)
    c: Coincident(g9,g10)
    c: Coincident(g10,g-3)
    c: Vertical(g10)
    c: Coincident(g10,g11)
    c: Coincident(g11,g0)
    c: Vertical(g6)
FEATURE [PartDesign::SubShapeBinder] Binder023  label="hs nut slot crs"
  BindCopyOnChange = 0
  BindMode = 0
  ClaimChildren = false
  Context = -> Body022 [Binder023.]
  Fuse = false
  MakeFace = true
  OffsetFill = false
  OffsetIntersection = false
  OffsetJoinType = 0
  OffsetOpenResult = false
  PartialLoad = false
  Refine = true
  Relative = true
  Support = -> [Body021[Sketch120.]]
  _Version = 2
FEATURE [Sketcher::SketchObject] Sketch125
  ArcFitTolerance = 1e-06
  AttachmentOffset = pos=(0,0,-19) rot=(0,0,1;0rad)
  AttachmentSupport = -> [XY_Plane022]
  ExternalGeometry = -> [Sketch118,Binder023]
  FullyConstrained = true
  MakeInternals = false
  MapMode = 5
  Placement = pos=(0,0,-19) rot=(0,0,1;0rad)
  sketch-geometry (11):
    g0: LineSegment StartX=-26.15 StartY=22.6 StartZ=0 EndX=-26.15 EndY=7.93786 EndZ=0
    g1: LineSegment StartX=-22.6 StartY=4.38786 StartZ=0 EndX=22.6 EndY=4.38786 EndZ=0
    g2: LineSegment StartX=26.15 StartY=7.93786 StartZ=0 EndX=26.15 EndY=22.6 EndZ=0
    g3: LineSegment StartX=22.6 StartY=26.15 StartZ=0 EndX=-22.6 EndY=26.15 EndZ=0
    g4: ArcOfCircle CenterX=-22.6 CenterY=22.6 CenterZ=0 NormalX=0 NormalY=0 NormalZ=1 AngleXU=0 Radius=3.55 StartAngle=1.5708 EndAngle=3.14159
    g5: ArcOfCircle CenterX=-22.6 CenterY=7.93786 CenterZ=0 NormalX=0 NormalY=0 NormalZ=1 AngleXU=0 Radius=3.55 StartAngle=3.14159 EndAngle=4.71239
    g6: ArcOfCircle CenterX=22.6 CenterY=7.93786 CenterZ=0 NormalX=0 NormalY=0 NormalZ=1 AngleXU=0 Radius=3.55 StartAngle=4.71239 EndAngle=6.28319
    g7: ArcOfCircle CenterX=22.6 CenterY=22.6 CenterZ=0 NormalX=0 NormalY=0 NormalZ=1 AngleXU=0 Radius=3.55 StartAngle=4e-16 EndAngle=1.5708
    g8: GeomPoint [constr] X=-26.15 Y=26.15 Z=0
    g9: GeomPoint [constr] X=26.15 Y=4.38786 Z=0
    g10: GeomPoint X=19 Y=4.38786 Z=0
  constraints (23):
    c: Tangent(g0,g4) = -1.5708
    c: Tangent(g0,g5) = -1.5708
    c: Tangent(g1,g5) = -1.5708
    c: Tangent(g1,g6) = -1.5708
    c: Tangent(g2,g6) = -1.5708
    c: Tangent(g2,g7) = -1.5708
    c: Tangent(g3,g7) = -1.5708
    c: Tangent(g3,g4) = -1.5708
    c: Vertical(g0)
    c: Vertical(g2)
    c: Horizontal(g1)
    c: Horizontal(g3)
    c: Equal(g4,g5)
    c: Equal(g5,g6)
    c: PointOnObject(g8,g0)
    c: PointOnObject(g8,g3)
    c: PointOnObject(g9,g1)
    c: PointOnObject(g9,g2)
    c: Coincident(g7,g-3)
    c: Distance(g-3,g2) = 2
    c: PointOnObject(g10,g1)
    c: Symmetric(g10,g-5,g-1)
    c: Symmetric(g4,g7,g-2)
FEATURE [PartDesign::SubShapeBinder] Binder024  label="hs nut slot trj"
  BindCopyOnChange = 0
  BindMode = 0
  ClaimChildren = false
  Context = -> Body022 [Binder024.]
  Fuse = false
  MakeFace = true
  OffsetFill = false
  OffsetIntersection = false
  OffsetJoinType = 0
  OffsetOpenResult = false
  PartialLoad = false
  Refine = true
  Relative = true
  Support = -> [Body021[Sketch121.]]
  _Version = 2
FEATURE [PartDesign::SubShapeBinder] Binder025  label="hs ULN2003 slot"
  BindCopyOnChange = 0
  BindMode = 0
  ClaimChildren = false
  Context = -> Body022 [Binder025.]
  Fuse = false
  MakeFace = true
  OffsetFill = false
  OffsetIntersection = false
  OffsetJoinType = 0
  OffsetOpenResult = false
  PartialLoad = false
  Refine = true
  Relative = true
  Support = -> [Body021[Sketch109.]]
  _Version = 2
FEATURE [PartDesign::Plane] DatumPlane011  label="hs pln ULN2003 slot"
  AttachmentSupport = -> [Binder014,XZ_Plane022]
  Length = 97.2543
  MapMode = 6
  Placement = pos=(0,-23.5,-41.125) rot=(0.57735,-0.57735,0.57735;2.0944rad)
  ResizeMode = 0
  Width = 75.4543
FEATURE [Sketcher::SketchObject] Sketch126
  ArcFitTolerance = 1e-06
  AttachmentSupport = -> [DatumPlane011]
  ExternalGeometry = -> [Binder025,Sketch124]
  FullyConstrained = true
  MakeInternals = false
  MapMode = 5
  Placement = pos=(0,-23.5,-41.125) rot=(0.57735,-0.57735,0.57735;2.0944rad)
  sketch-geometry (16):
    g0: LineSegment StartX=-2.5 StartY=15.975 StartZ=0 EndX=-2.5 EndY=-15.975 EndZ=0
    g1: LineSegment StartX=-2.5 StartY=-15.975 StartZ=0 EndX=0 EndY=-15.975 EndZ=0
    g2: LineSegment StartX=15.725 StartY=-15.975 StartZ=0 EndX=15.725 EndY=-11.1 EndZ=0
    g3: LineSegment StartX=15.725 StartY=15.975 StartZ=0 EndX=2.05 EndY=15.975 EndZ=0
    g4: LineSegment StartX=0 StartY=17.475 StartZ=0 EndX=0 EndY=15.975 EndZ=0
    g5: LineSegment StartX=0 StartY=-17.475 StartZ=0 EndX=2.05 EndY=-17.475 EndZ=0
    g6: LineSegment StartX=2.05 StartY=-17.475 StartZ=0 EndX=2.05 EndY=-15.975 EndZ=0
    g7: LineSegment StartX=2.05 StartY=17.475 StartZ=0 EndX=0 EndY=17.475 EndZ=0
    g8: LineSegment StartX=18.625 StartY=5.1 StartZ=0 EndX=15.725 EndY=5.1 EndZ=0
    g9: LineSegment StartX=15.725 StartY=-11.1 StartZ=0 EndX=18.625 EndY=-11.1 EndZ=0
    g10: LineSegment StartX=15.725 StartY=5.1 StartZ=0 EndX=15.725 EndY=15.975 EndZ=0
    g11: LineSegment StartX=2.05 StartY=15.975 StartZ=0 EndX=2.05 EndY=17.475 EndZ=0
    g12: LineSegment StartX=2.05 StartY=-15.975 StartZ=0 EndX=15.725 EndY=-15.975 EndZ=0
    g13: LineSegment StartX=0 StartY=-15.975 StartZ=0 EndX=0 EndY=-17.475 EndZ=0
    g14: LineSegment StartX=0 StartY=15.975 StartZ=0 EndX=-2.5 EndY=15.975 EndZ=0
    g15: ArcOfCircle CenterX=-81.0464 CenterY=-3 CenterZ=0 NormalX=0 NormalY=0 NormalZ=1 AngleXU=0 Radius=100 StartAngle=6.2021 EndAngle=6.36427
  constraints (43):
    c: Coincident(g0,g1)
    c: Coincident(g12,g2)
    c: Coincident(g10,g3)
    c: Coincident(g14,g0)
    c: Vertical(g2)
    c: Horizontal(g1)
    c: Horizontal(g3)
    c: Coincident(g0,g-4)
    c: Coincident(g12,g-3)
    c: Coincident(g13,g5)
    c: Coincident(g5,g6)
    c: Coincident(g11,g7)
    c: Coincident(g7,g4)
    c: Vertical(g4)
    c: Vertical(g6)
    c: Coincident(g4,g-5)
    c: Coincident(g5,g-6)
    c: Horizontal(g8)
    c: Horizontal(g9)
    c: Coincident(g8,g-7)
    c: Coincident(g9,g-7)
    c: PointOnObject(g8,g-3)
    c: PointOnObject(g2,g9)
    c: PointOnObject(g9,g-3)
    c: PointOnObject(g6,g12)
    c: PointOnObject(g1,g13)
    c: PointOnObject(g12,g6)
    c: PointOnObject(g4,g14)
    c: PointOnObject(g13,g1)
    c: Coincident(g3,g11)
    c: PointOnObject(g14,g4)
    c: Horizontal(g12)
    c: Coincident(g3,g-3)
    c: Vertical(g11)
    c: Coincident(g7,g-5)
    c: Horizontal(g14)
    c: Coincident(g8,g10)
    c: Vertical(g13)
    c: Coincident(g0,g-4)
    c: Coincident(g5,g-6)
    c: Coincident(g15,g8)
    c: Coincident(g15,g9)
    c: Radius(g15) = 100
FEATURE [PartDesign::Plane] DatumPlane012  label="hs pln ESP slot"
  AttachmentSupport = -> [Binder020,XZ_Plane022]
  Length = 97.2543
  MapMode = 6
  Placement = pos=(0,-29.65,-55.25) rot=(0.57735,-0.57735,0.57735;2.0944rad)
  ResizeMode = 0
  Width = 75.4543
FEATURE [Sketcher::SketchObject] Sketch127
  ArcFitTolerance = 1e-06
  AttachmentSupport = -> [DatumPlane012]
  ExternalGeometry = -> [Binder019,Binder025]
  FullyConstrained = true
  MakeInternals = false
  MapMode = 5
  Placement = pos=(0,-29.65,-55.25) rot=(0.57735,-0.57735,0.57735;2.0944rad)
  sketch-geometry (14):
    g0: LineSegment StartX=0 StartY=14.55 StartZ=0 EndX=0 EndY=-14.55 EndZ=0
    g1: LineSegment StartX=0 StartY=-14.55 StartZ=0 EndX=2 EndY=-14.55 EndZ=0
    g2: LineSegment StartX=11.625 StartY=-15.975 StartZ=0 EndX=11.625 EndY=14.55 EndZ=0
    g3: LineSegment StartX=11.625 StartY=14.55 StartZ=0 EndX=3.5 EndY=14.55 EndZ=0
    g4: LineSegment StartX=2 StartY=15.75 StartZ=0 EndX=2 EndY=14.55 EndZ=0
    g5: LineSegment StartX=2 StartY=-15.75 StartZ=0 EndX=3.5 EndY=-15.75 EndZ=0
    g6: LineSegment StartX=3.5 StartY=-15.75 StartZ=0 EndX=3.5 EndY=-14.55 EndZ=0
    g7: LineSegment StartX=3.5 StartY=15.75 StartZ=0 EndX=2 EndY=15.75 EndZ=0
    g8: LineSegment StartX=3.5 StartY=-14.55 StartZ=0 EndX=4.1208 EndY=-14.55 EndZ=0
    g9: LineSegment StartX=3.5 StartY=14.55 StartZ=0 EndX=3.5 EndY=15.75 EndZ=0
    g10: LineSegment StartX=2 StartY=-14.55 StartZ=0 EndX=2 EndY=-15.75 EndZ=0
    g11: LineSegment StartX=2 StartY=14.55 StartZ=0 EndX=0 EndY=14.55 EndZ=0
    g12: ArcOfCircle CenterX=7.499 CenterY=-11.9712 CenterZ=0 NormalX=0 NormalY=0 NormalZ=1 AngleXU=0 Radius=4.25 StartAngle=3.7936 EndAngle=4.77393
    g13: LineSegment StartX=7.76039 StartY=-16.2131 StartZ=0 EndX=11.625 EndY=-15.975 EndZ=0
  constraints (35):
    c: Coincident(g0,g1)
    c: Coincident(g2,g3)
    c: Coincident(g11,g0)
    c: Vertical(g2)
    c: Horizontal(g1)
    c: Horizontal(g3)
    c: Coincident(g0,g-4)
    c: Coincident(g0,g-4)
    c: Coincident(g10,g5)
    c: Coincident(g5,g6)
    c: Coincident(g9,g7)
    c: Coincident(g7,g4)
    c: Vertical(g4)
    c: Vertical(g6)
    c: Coincident(g4,g-3)
    c: Coincident(g5,g-6)
    c: PointOnObject(g1,g10)
    c: Coincident(g6,g8)
    c: PointOnObject(g10,g1)
    c: Coincident(g3,g9)
    c: Coincident(g7,g-3)
    c: Coincident(g4,g11)
    c: Vertical(g9)
    c: Horizontal(g11)
    c: PointOnObject(g-5,g3)
    c: Vertical(g10)
    c: Coincident(g5,g-6)
    c: Horizontal(g8)
    c: Coincident(g8,g12)
    c: Equal(g12,g-8)
    c: Coincident(g12,g-8)
    c: PointOnObject(g-5,g8)
    c: Coincident(g2,g-7)
    c: Coincident(g13,g2)
    c: Tangent(g13,g12) = -1.5708
FEATURE [Sketcher::SketchObject] Sketch128
  ArcFitTolerance = 1e-06
  AttachmentSupport = -> [XZ_Plane022]
  ExternalGeometry = -> [Binder018]
  FullyConstrained = true
  MakeInternals = false
  MapMode = 5
  Placement = pos=(0,0,0) rot=(1,0,0;1.5708rad)
  sketch-geometry (12):
    g0: ArcOfCircle CenterX=2.9 CenterY=-50.02 CenterZ=0 NormalX=0 NormalY=0 NormalZ=1 AngleXU=0 Radius=0.83581 StartAngle=-1.8e-15 EndAngle=1.5708
    g1: ArcOfCircle CenterX=-3.4 CenterY=-50.02 CenterZ=0 NormalX=0 NormalY=0 NormalZ=1 AngleXU=0 Radius=0.83581 StartAngle=1.5708 EndAngle=3.14159
    g2: ArcOfCircle CenterX=-3.4 CenterY=-50.7386 CenterZ=0 NormalX=0 NormalY=0 NormalZ=1 AngleXU=0 Radius=0.83581 StartAngle=3.14159 EndAngle=3.92699
    g3: ArcOfCircle CenterX=-2.86863 CenterY=-51.27 CenterZ=0 NormalX=0 NormalY=0 NormalZ=1 AngleXU=0 Radius=0.83581 StartAngle=3.92699 EndAngle=4.71239
    g4: ArcOfCircle CenterX=2.36863 CenterY=-51.27 CenterZ=0 NormalX=0 NormalY=0 NormalZ=1 AngleXU=0 Radius=0.83581 StartAngle=4.71239 EndAngle=5.49779
    g5: ArcOfCircle CenterX=2.9 CenterY=-50.7386 CenterZ=0 NormalX=0 NormalY=0 NormalZ=1 AngleXU=0 Radius=0.83581 StartAngle=5.49779 EndAngle=6.28319
    g6: LineSegment StartX=2.9 StartY=-49.1842 StartZ=0 EndX=-3.4 EndY=-49.1842 EndZ=0
    g7: LineSegment StartX=-4.23581 StartY=-50.02 StartZ=0 EndX=-4.23581 EndY=-50.7386 EndZ=0
    g8: LineSegment StartX=-3.99101 StartY=-51.3296 StartZ=0 EndX=-3.45964 EndY=-51.861 EndZ=0
    g9: LineSegment StartX=-2.86863 StartY=-52.1058 StartZ=0 EndX=2.36863 EndY=-52.1058 EndZ=0
    g10: LineSegment StartX=2.95964 StartY=-51.861 StartZ=0 EndX=3.49101 EndY=-51.3296 EndZ=0
    g11: LineSegment StartX=3.73581 StartY=-50.02 StartZ=0 EndX=3.73581 EndY=-50.7386 EndZ=0
  constraints (24):
    c: Coincident(g0,g-3)
    c: Coincident(g1,g-4)
    c: Coincident(g2,g-5)
    c: Coincident(g3,g-6)
    c: Coincident(g4,g-7)
    c: Coincident(g5,g-8)
    c: Horizontal(g6)
    c: Vertical(g7)
    c: Horizontal(g9)
    c: Vertical(g11)
    c: Tangent(g0,g6) = -1.5708
    c: Tangent(g1,g6) = -1.5708
    c: Tangent(g1,g7) = -1.5708
    c: Tangent(g2,g7) = -1.5708
    c: Tangent(g2,g8) = -1.5708
    c: Tangent(g3,g8) = -1.5708
    c: Tangent(g3,g9) = -1.5708
    c: Tangent(g4,g9) = -1.5708
    c: Tangent(g4,g10) = -1.5708
    c: Tangent(g5,g10) = -1.5708
    c: Tangent(g5,g11) = 1.5708
    c: Tangent(g0,g11) = 1.5708
    c: Equal(g-3,g0)
    c: PointOnObject(g-7,g10)
FEATURE [Sketcher::SketchObject] Sketch129  label="sk ESP retainer"
  ArcFitTolerance = 1e-06
  AttachmentSupport = -> [XZ_Plane021]
  ExternalGeometry = -> [Sketch113]
  FullyConstrained = true
  MakeInternals = false
  MapMode = 5
  Placement = pos=(0,0,0) rot=(1,0,0;1.5708rad)
  sketch-geometry (21):
    g0: LineSegment StartX=5 StartY=-51.75 StartZ=0 EndX=5 EndY=-53.25 EndZ=0
    g1: LineSegment StartX=6 StartY=-54.25 StartZ=0 EndX=10 EndY=-54.25 EndZ=0
    g2: LineSegment StartX=11 StartY=-53.25 StartZ=0 EndX=11 EndY=-51.75 EndZ=0
    g3: LineSegment StartX=10 StartY=-50.75 StartZ=0 EndX=6 EndY=-50.75 EndZ=0
    g4: ArcOfCircle CenterX=6 CenterY=-51.75 CenterZ=0 NormalX=0 NormalY=0 NormalZ=1 AngleXU=0 Radius=1 StartAngle=1.5708 EndAngle=3.14159
    g5: ArcOfCircle CenterX=6 CenterY=-53.25 CenterZ=0 NormalX=0 NormalY=0 NormalZ=1 AngleXU=0 Radius=1 StartAngle=3.14159 EndAngle=4.71239
    g6: ArcOfCircle CenterX=10 CenterY=-53.25 CenterZ=0 NormalX=0 NormalY=0 NormalZ=1 AngleXU=0 Radius=1 StartAngle=4.71239 EndAngle=6.28319
    g7: ArcOfCircle CenterX=10 CenterY=-51.75 CenterZ=0 NormalX=0 NormalY=0 NormalZ=1 AngleXU=0 Radius=1 StartAngle=-2.7e-15 EndAngle=1.5708
    g8: GeomPoint [constr] X=5 Y=-50.75 Z=0
    g9: GeomPoint [constr] X=11 Y=-54.25 Z=0
    g10: LineSegment StartX=4.2 StartY=-51.75 StartZ=0 EndX=4.2 EndY=-53.25 EndZ=0
    g11: LineSegment StartX=6 StartY=-55.05 StartZ=0 EndX=10 EndY=-55.05 EndZ=0
    g12: LineSegment StartX=11.8 StartY=-53.25 StartZ=0 EndX=11.8 EndY=-51.75 EndZ=0
    g13: LineSegment StartX=10 StartY=-49.95 StartZ=0 EndX=6 EndY=-49.95 EndZ=0
    g14: ArcOfCircle CenterX=6 CenterY=-51.75 CenterZ=0 NormalX=0 NormalY=0 NormalZ=1 AngleXU=0 Radius=1.8 StartAngle=1.5708 EndAngle=3.14159
    g15: ArcOfCircle CenterX=6 CenterY=-53.25 CenterZ=0 NormalX=0 NormalY=0 NormalZ=1 AngleXU=0 Radius=1.8 StartAngle=3.14159 EndAngle=4.71239
    g16: ArcOfCircle CenterX=10 CenterY=-53.25 CenterZ=0 NormalX=0 NormalY=0 NormalZ=1 AngleXU=0 Radius=1.8 StartAngle=4.71239 EndAngle=6.28319
    g17: ArcOfCircle CenterX=10 CenterY=-51.75 CenterZ=0 NormalX=0 NormalY=0 NormalZ=1 AngleXU=0 Radius=1.8 StartAngle=1.8e-15 EndAngle=1.5708
    g18: GeomPoint [constr] X=4.2 Y=-49.95 Z=0
    g19: GeomPoint [constr] X=11.8 Y=-55.05 Z=0
    g20: LineSegment [constr] StartX=4.2 StartY=-52.5 StartZ=0 EndX=11.8 EndY=-52.5 EndZ=0
  constraints (47):
    c: Tangent(g0,g4) = -1.5708
    c: Tangent(g0,g5) = -1.5708
    c: Tangent(g1,g5) = -1.5708
    c: Tangent(g1,g6) = -1.5708
    c: Tangent(g2,g6) = -1.5708
    c: Tangent(g2,g7) = -1.5708
    c: Tangent(g3,g7) = -1.5708
    c: Tangent(g3,g4) = -1.5708
    c: Vertical(g0)
    c: Vertical(g2)
    c: Horizontal(g1)
    c: Horizontal(g3)
    c: Equal(g4,g5)
    c: PointOnObject(g8,g0)
    c: PointOnObject(g8,g3)
    c: PointOnObject(g9,g1)
    c: PointOnObject(g9,g2)
    c: Tangent(g10,g14) = -1.5708
    c: Tangent(g10,g15) = -1.5708
    c: Tangent(g11,g15) = -1.5708
    c: Tangent(g11,g16) = -1.5708
    c: Tangent(g12,g16) = -1.5708
    c: Tangent(g12,g17) = -1.5708
    c: Tangent(g13,g17) = -1.5708
    c: Tangent(g13,g14) = -1.5708
    c: Vertical(g10)
    c: Vertical(g12)
    c: Horizontal(g11)
    c: Horizontal(g13)
    c: Equal(g14,g15)
    c: Equal(g15,g16)
    c: PointOnObject(g18,g10)
    c: PointOnObject(g18,g13)
    c: PointOnObject(g19,g11)
    c: PointOnObject(g19,g12)
    c: Coincident(g7,g17)
    c: Coincident(g5,g15)
    c: Distance(g2,g12) = 0.8
    c: PointOnObject(g20,g10)
    c: PointOnObject(g20,g12)
    c: Symmetric(g-4,g-3,g20)
    c: Symmetric(g7,g6,g20)
    c: DistanceY(g-3,g3) = 1
    c: DistanceX(g0,g2) = 6
    c: Radius(g7) = 1
    c: Coincident(g6,g16)
    c: DistanceX(g-1,g0) = 5
FEATURE [PartDesign::Plane] DatumPlane014  label="hs pln nut slot top"
  AttachmentSupport = -> [Binder024]
  Length = 73.44
  MapMode = 7
  Placement = pos=(19,0,-5.8) rot=(0,0,1;0rad)
  ResizeMode = 0
  Width = 73.44
FEATURE [PartDesign::Plane] DatumPlane015  label="hs pln nut slot btm"
  AttachmentSupport = -> [Binder024]
  Length = 73.44
  MapMode = 7
  Placement = pos=(19,0,-9.2) rot=(0,0,1;0rad)
  ResizeMode = 0
  Width = 73.44
FEATURE [Sketcher::SketchObject] Sketch131
  ArcFitTolerance = 1e-06
  AttachmentSupport = -> [DatumPlane015]
  ExternalGeometry = -> [Binder023]
  FullyConstrained = true
  MakeInternals = false
  MapMode = 5
  Placement = pos=(19,0,-9.2) rot=(0,0,1;0rad)
  sketch-geometry (5):
    g0: LineSegment StartX=-3.8 StartY=16 StartZ=0 EndX=-3.8 EndY=-2.19393 EndZ=0
    g1: LineSegment StartX=-3.8 StartY=-2.19393 StartZ=0 EndX=-4e-16 EndY=-4.38786 EndZ=0
    g2: LineSegment StartX=-4e-16 StartY=-4.38786 StartZ=0 EndX=3.8 EndY=-2.19393 EndZ=0
    g3: LineSegment StartX=3.8 StartY=-2.19393 StartZ=0 EndX=3.8 EndY=16 EndZ=0
    g4: LineSegment StartX=3.8 StartY=16 StartZ=0 EndX=-3.8 EndY=16 EndZ=0
  constraints (10):
    c: Coincident(g-3,g0)
    c: Coincident(g0,g-3)
    c: Coincident(g0,g1)
    c: Coincident(g1,g-4)
    c: Coincident(g1,g2)
    c: Coincident(g2,g-5)
    c: Coincident(g2,g3)
    c: Coincident(g3,g-5)
    c: Coincident(g3,g4)
    c: Coincident(g4,g0)
FEATURE [Sketcher::SketchObject] Sketch132
  ArcFitTolerance = 1e-06
  AttachmentSupport = -> [DatumPlane015]
  ExternalGeometry = -> [Binder023]
  FullyConstrained = true
  MakeInternals = false
  MapMode = 5
  Placement = pos=(19,0,-9.2) rot=(0,0,1;0rad)
  sketch-geometry (1):
    g0: Circle CenterX=0 CenterY=0 CenterZ=0 NormalX=0 NormalY=0 NormalZ=1 AngleXU=0 Radius=2.25
  constraints (2):
    c: Coincident(g0,g-1)
    c: Equal(g0,g-3)
FEATURE [PartDesign::SubShapeBinder] Binder027  label="sh ref right"
  BindCopyOnChange = 0
  BindMode = 0
  ClaimChildren = false
  Context = -> Body024 [Binder027.]
  Fuse = false
  MakeFace = true
  OffsetFill = false
  OffsetIntersection = false
  OffsetJoinType = 0
  OffsetOpenResult = false
  PartialLoad = false
  Refine = true
  Relative = true
  Support = -> [Body021[Sketch106.]]
  _Version = 2
FEATURE [PartDesign::SubShapeBinder] Binder028  label="sh ref front"
  BindCopyOnChange = 0
  BindMode = 0
  ClaimChildren = false
  Context = -> Body024 [Binder028.]
  Fuse = false
  MakeFace = true
  OffsetFill = false
  OffsetIntersection = false
  OffsetJoinType = 0
  OffsetOpenResult = false
  PartialLoad = false
  Refine = true
  Relative = true
  Support = -> [Body021[Sketch107.]]
  _Version = 2
FEATURE [PartDesign::SubShapeBinder] Binder029  label="sh ref separation"
  BindCopyOnChange = 0
  BindMode = 0
  ClaimChildren = false
  Context = -> Body024 [Binder029.]
  Fuse = false
  MakeFace = true
  OffsetFill = false
  OffsetIntersection = false
  OffsetJoinType = 0
  OffsetOpenResult = false
  PartialLoad = false
  Refine = true
  Relative = true
  Support = -> [Body021[Sketch110.]]
  _Version = 2
FEATURE [PartDesign::Plane] DatumPlane016  label="sh pln right"
  AttachmentOffset = pos=(0,0,3) rot=(0,0,1;0rad)
  AttachmentSupport = -> [Binder028,YZ_Plane025]
  Length = 100.198
  MapMode = 6
  Placement = pos=(33.6,0,7e-16) rot=(0,1,0;1.5708rad)
  ResizeMode = 0
  Width = 72.798
FEATURE [PartDesign::Plane] DatumPlane017  label="sh pln left"
  AttachmentOffset = pos=(0,0,-3) rot=(0,0,1;0rad)
  AttachmentSupport = -> [Binder028,YZ_Plane025]
  Length = 100.198
  MapMode = 6
  Placement = pos=(-33.6,0,-7e-16) rot=(0,1,0;1.5708rad)
  ResizeMode = 0
  Width = 72.798
FEATURE [Sketcher::SketchObject] Sketch133
  ArcFitTolerance = 1e-06
  AttachmentSupport = -> [DatumPlane016]
  ExternalGeometry = -> [Binder029,Binder027]
  FullyConstrained = true
  MakeInternals = false
  MapMode = 5
  Placement = pos=(33.6,0,7e-16) rot=(0,1,0;1.5708rad)
  sketch-geometry (4):
    g0: LineSegment StartX=-4.5 StartY=15.85 StartZ=0 EndX=-4.5 EndY=-33.6 EndZ=0
    g1: LineSegment StartX=-4.5 StartY=-33.6 StartZ=0 EndX=61 EndY=-33.6 EndZ=0
    g2: LineSegment StartX=61 StartY=-33.6 StartZ=0 EndX=61 EndY=15.85 EndZ=0
    g3: LineSegment StartX=61 StartY=15.85 StartZ=0 EndX=-4.5 EndY=15.85 EndZ=0
  constraints (12):
    c: Coincident(g0,g1)
    c: Coincident(g1,g2)
    c: Coincident(g2,g3)
    c: Coincident(g3,g0)
    c: Vertical(g0)
    c: Vertical(g2)
    c: Horizontal(g1)
    c: Horizontal(g3)
    c: PointOnObject(g-3,g3)
    c: Distance(g0,g-4) = 3
    c: Distance(g-6,g2) = 3
    c: Distance(g-6,g1) = 3
FEATURE [PartDesign::Pad] Pad024  label="SH Base"
  Direction = (1,0,2e-16)
  Length = 10
  Length2 = 10
  Placement = pos=(33.6,0,7e-16) rot=(0,1,0;1.5708rad)
  Profile = -> Sketch133
  ReferenceAxis = -> Sketch133 [N_Axis]
  Refine = true
  Suppressed = false
  Type = 3
  UpToFace = -> DatumPlane017
FEATURE [PartDesign::SubShapeBinder] Binder031  label="sh ref rim trj"
  BindCopyOnChange = 0
  BindMode = 0
  ClaimChildren = false
  Context = -> Body024 [Binder031.]
  Fuse = false
  MakeFace = true
  OffsetFill = false
  OffsetIntersection = false
  OffsetJoinType = 0
  OffsetOpenResult = false
  PartialLoad = false
  Refine = true
  Relative = true
  Support = -> [Body021[Sketch122.]]
  _Version = 2
FEATURE [PartDesign::SubShapeBinder] Binder032  label="sh ref rim crs"
  BindCopyOnChange = 0
  BindMode = 0
  ClaimChildren = false
  Context = -> Body024 [Binder032.]
  Fuse = false
  MakeFace = true
  OffsetFill = false
  OffsetIntersection = false
  OffsetJoinType = 0
  OffsetOpenResult = false
  PartialLoad = false
  Refine = true
  Relative = true
  Support = -> [Body021[Sketch123.]]
  _Version = 2
FEATURE [Sketcher::SketchObject] Sketch135  label="sh rim crs"
  ArcFitTolerance = 1e-06
  AttachmentSupport = -> [YZ_Plane025]
  ExternalGeometry = -> [Binder032,Binder029]
  FullyConstrained = true
  MakeInternals = false
  MapMode = 5
  Placement = pos=(0,0,0) rot=(0.57735,0.57735,0.57735;2.0944rad)
  sketch-geometry (4):
    g0: ArcOfCircle CenterX=15.5117 CenterY=-55.5 CenterZ=0 NormalX=0 NormalY=0 NormalZ=1 AngleXU=0 Radius=1.12502 StartAngle=1.26536 EndAngle=5.01782
    g1: LineSegment StartX=15.85 StartY=-54.4271 StartZ=0 EndX=17.35 EndY=-54.9 EndZ=0
    g2: LineSegment StartX=17.35 StartY=-54.9 StartZ=0 EndX=17.35 EndY=-56.1 EndZ=0
    g3: LineSegment StartX=17.35 StartY=-56.1 StartZ=0 EndX=15.85 EndY=-56.5729 EndZ=0
  constraints (9):
    c: Coincident(g1,g-3)
    c: Coincident(g1,g2)
    c: Coincident(g2,g-4)
    c: Coincident(g2,g3)
    c: Tangent(g0,g3) = 1.5708
    c: Tangent(g0,g1) = 1.5708
    c: PointOnObject(g-3,g1)
    c: PointOnObject(g-4,g3)
    c: PointOnObject(g0,g-5)
FEATURE [Sketcher::SketchObject] Sketch136  label="sh rim trj"
  ArcFitTolerance = 1e-06
  AttachmentSupport = -> [XZ_Plane024]
  ExternalGeometry = -> [Binder031]
  FullyConstrained = true
  MakeInternals = false
  MapMode = 5
  Placement = pos=(0,0,0) rot=(1,0,0;1.5708rad)
  sketch-geometry (8):
    g0: LineSegment StartX=-21.2392 StartY=-55.5 StartZ=0 EndX=21.2392 EndY=-55.5 EndZ=0
    g1: LineSegment StartX=28.1 StartY=-30 StartZ=0 EndX=28.1 EndY=10 EndZ=0
    g2: LineSegment StartX=-28.1 StartY=10 StartZ=0 EndX=-28.1 EndY=-30 EndZ=0
    g3: ArcOfCircle CenterX=-21.2392 CenterY=-51.5 CenterZ=0 NormalX=0 NormalY=0 NormalZ=1 AngleXU=0 Radius=4 StartAngle=3.40616 EndAngle=4.71239
    g4: ArcOfCircle CenterX=21.2392 CenterY=-51.5 CenterZ=0 NormalX=0 NormalY=0 NormalZ=1 AngleXU=0 Radius=4 StartAngle=4.71239 EndAngle=6.01862
    g5: GeomPoint [constr] X=-28.1 Y=-55.5 Z=0
    g6: ArcOfCircle CenterX=-58.1201 CenterY=-30 CenterZ=0 NormalX=0 NormalY=0 NormalZ=1 AngleXU=0 Radius=86.2201 StartAngle=6.01862 EndAngle=6.28319
    g7: ArcOfCircle CenterX=58.1201 CenterY=-30 CenterZ=0 NormalX=0 NormalY=0 NormalZ=1 AngleXU=0 Radius=86.2201 StartAngle=3.14159 EndAngle=3.40616
  constraints (18):
    c: Tangent(g0,g3) = -1.5708
    c: Tangent(g0,g4) = -1.5708
    c: Horizontal(g0)
    c: Vertical(g1)
    c: Vertical(g2)
    c: PointOnObject(g5,g0)
    c: PointOnObject(g5,g2)
    c: Tangent(g4,g6) = -1.5708
    c: Tangent(g1,g6) = -1.5708
    c: Tangent(g2,g7) = -1.5708
    c: Tangent(g3,g7) = -1.5708
    c: Coincident(g3,g-4)
    c: Coincident(g4,g-5)
    c: Equal(g-3,g7)
    c: Horizontal(g-6,g1)
    c: Coincident(g1,g-7)
    c: Coincident(g2,g-8)
    c: Equal(g-4,g3)
FEATURE [PartDesign::AdditivePipe] AdditivePipe004  label="SH Rim"
  AuxilleryCurvelinear = true
  AuxillerySpineTangent = false
  BaseFeature = -> Pad024
  Binormal = (0,0,0)
  Mode = 0
  Placement = pos=(33.6,0,7e-16) rot=(0,1,0;1.5708rad)
  Profile = -> Sketch135
  Refine = true
  Spine = -> Sketch136
  SpineTangent = false
  Suppressed = false
  Transformation = 0
  Transition = 0
FEATURE [PartDesign::SubShapeBinder] Binder034  label="sl ref right"
  BindCopyOnChange = 0
  BindMode = 0
  ClaimChildren = false
  Context = -> Body025 [Binder034.]
  Fuse = false
  MakeFace = true
  OffsetFill = false
  OffsetIntersection = false
  OffsetJoinType = 0
  OffsetOpenResult = false
  PartialLoad = false
  Refine = true
  Relative = true
  Support = -> [Body021[Sketch106.]]
  _Version = 2
FEATURE [PartDesign::SubShapeBinder] Binder035  label="sl ref front"
  BindCopyOnChange = 0
  BindMode = 0
  ClaimChildren = false
  Context = -> Body025 [Binder035.]
  Fuse = false
  MakeFace = true
  OffsetFill = false
  OffsetIntersection = false
  OffsetJoinType = 0
  OffsetOpenResult = false
  PartialLoad = false
  Refine = true
  Relative = true
  Support = -> [Body021[Sketch107.]]
  _Version = 2
FEATURE [PartDesign::SubShapeBinder] Binder036  label="sl ref separation"
  BindCopyOnChange = 0
  BindMode = 0
  ClaimChildren = false
  Context = -> Body025 [Binder036.]
  Fuse = false
  MakeFace = true
  OffsetFill = false
  OffsetIntersection = false
  OffsetJoinType = 0
  OffsetOpenResult = false
  PartialLoad = false
  Refine = true
  Relative = true
  Support = -> [Body021[Sketch110.]]
  _Version = 2
FEATURE [PartDesign::SubShapeBinder] Binder037  label="sl ref ESP retainer"
  BindCopyOnChange = 0
  BindMode = 0
  ClaimChildren = false
  Context = -> Body025 [Binder037.]
  Fuse = false
  MakeFace = true
  OffsetFill = false
  OffsetIntersection = false
  OffsetJoinType = 0
  OffsetOpenResult = false
  PartialLoad = false
  Refine = true
  Relative = true
  Support = -> [Body021[Sketch129.]]
  _Version = 2
FEATURE [PartDesign::SubShapeBinder] Binder038  label="sl ref groove trj"
  BindCopyOnChange = 0
  BindMode = 0
  ClaimChildren = false
  Context = -> Body025 [Binder038.]
  Fuse = false
  MakeFace = true
  OffsetFill = false
  OffsetIntersection = false
  OffsetJoinType = 0
  OffsetOpenResult = false
  PartialLoad = false
  Refine = true
  Relative = true
  Support = -> [Body021[Sketch122.]]
  _Version = 2
FEATURE [PartDesign::SubShapeBinder] Binder039  label="sl ref groove crs"
  BindCopyOnChange = 0
  BindMode = 0
  ClaimChildren = false
  Context = -> Body025 [Binder039.]
  Fuse = false
  MakeFace = true
  OffsetFill = false
  OffsetIntersection = false
  OffsetJoinType = 0
  OffsetOpenResult = false
  PartialLoad = false
  Refine = true
  Relative = true
  Support = -> [Body021[Sketch123.]]
  _Version = 2
FEATURE [PartDesign::Plane] DatumPlane018  label="sl pln right"
  AttachmentOffset = pos=(0,0,3) rot=(0,0,1;0rad)
  AttachmentSupport = -> [Binder035,YZ_Plane026]
  Length = 100.198
  MapMode = 6
  Placement = pos=(33.6,0,7e-16) rot=(0,1,0;1.5708rad)
  ResizeMode = 0
  Width = 72.798
FEATURE [PartDesign::Plane] DatumPlane019  label="sl pln left"
  AttachmentOffset = pos=(0,0,-3) rot=(0,0,1;0rad)
  AttachmentSupport = -> [Binder035,YZ_Plane026]
  Length = 100.198
  MapMode = 6
  Placement = pos=(-33.6,0,-7e-16) rot=(0,1,0;1.5708rad)
  ResizeMode = 0
  Width = 72.798
FEATURE [Sketcher::SketchObject] Sketch137
  ArcFitTolerance = 1e-06
  AttachmentSupport = -> [DatumPlane018]
  ExternalGeometry = -> [Binder034,Binder036]
  FullyConstrained = true
  MakeInternals = false
  MapMode = 5
  Placement = pos=(33.6,0,7e-16) rot=(0,1,0;1.5708rad)
  sketch-geometry (4):
    g0: LineSegment StartX=-4.5 StartY=33.6 StartZ=0 EndX=-4.5 EndY=16.15 EndZ=0
    g1: LineSegment StartX=-4.5 StartY=16.15 StartZ=0 EndX=61 EndY=16.15 EndZ=0
    g2: LineSegment StartX=61 StartY=16.15 StartZ=0 EndX=61 EndY=33.6 EndZ=0
    g3: LineSegment StartX=61 StartY=33.6 StartZ=0 EndX=-4.5 EndY=33.6 EndZ=0
  constraints (12):
    c: Coincident(g0,g1)
    c: Coincident(g1,g2)
    c: Coincident(g2,g3)
    c: Coincident(g3,g0)
    c: Vertical(g0)
    c: Vertical(g2)
    c: Horizontal(g1)
    c: Horizontal(g3)
    c: Distance(g-3,g3) = 3
    c: Distance(g-4,g0) = 3
    c: Distance(g-5,g2) = 3
    c: PointOnObject(g-6,g1)
FEATURE [PartDesign::Pad] Pad025
  Direction = (1,0,2e-16)
  Length = 10
  Length2 = 10
  Placement = pos=(33.6,0,7e-16) rot=(0,1,0;1.5708rad)
  Profile = -> Sketch137
  ReferenceAxis = -> Sketch137 [N_Axis]
  Refine = true
  Suppressed = false
  Type = 3
  UpToFace = -> DatumPlane019
FEATURE [Sketcher::SketchObject] Sketch138  label="sl groove crs"
  ArcFitTolerance = 1e-06
  AttachmentSupport = -> [YZ_Plane026]
  ExternalGeometry = -> [Binder039]
  FullyConstrained = true
  MakeInternals = false
  MapMode = 5
  Placement = pos=(0,0,0) rot=(0.57735,0.57735,0.57735;2.0944rad)
  sketch-geometry (4):
    g0: ArcOfCircle CenterX=14.9329 CenterY=-55.5 CenterZ=0 NormalX=0 NormalY=0 NormalZ=1 AngleXU=0 Radius=1.86246 StartAngle=1.05592 EndAngle=5.22726
    g1: ArcOfCircle CenterX=17.8372 CenterY=-55.5 CenterZ=0 NormalX=0 NormalY=0 NormalZ=1 AngleXU=0 Radius=0.839373 StartAngle=4.19752 EndAngle=8.36885
    g2: LineSegment StartX=15.85 StartY=-53.879 StartZ=0 EndX=17.4239 EndY=-54.7694 EndZ=0
    g3: LineSegment StartX=17.4239 StartY=-56.2306 StartZ=0 EndX=15.85 EndY=-57.121 EndZ=0
  constraints (9):
    c: Coincident(g0,g-3)
    c: Coincident(g0,g-4)
    c: Coincident(g1,g-5)
    c: Coincident(g1,g-5)
    c: Coincident(g2,g1)
    c: Coincident(g3,g1)
    c: Coincident(g3,g0)
    c: Equal(g-5,g1)
    c: Tangent(g2,g0) = 1.5708
FEATURE [Sketcher::SketchObject] Sketch139  label="sl groove trj"
  ArcFitTolerance = 1e-06
  AttachmentSupport = -> [XZ_Plane025]
  ExternalGeometry = -> [Binder038]
  FullyConstrained = true
  MakeInternals = false
  MapMode = 5
  Placement = pos=(0,0,0) rot=(1,0,0;1.5708rad)
  sketch-geometry (7):
    g0: ArcOfCircle CenterX=58.1201 CenterY=-30 CenterZ=0 NormalX=0 NormalY=0 NormalZ=1 AngleXU=0 Radius=86.2201 StartAngle=3.14159 EndAngle=3.40616
    g1: ArcOfCircle CenterX=-21.2392 CenterY=-51.5 CenterZ=0 NormalX=0 NormalY=0 NormalZ=1 AngleXU=0 Radius=4 StartAngle=3.40616 EndAngle=4.71239
    g2: ArcOfCircle CenterX=21.2392 CenterY=-51.5 CenterZ=0 NormalX=0 NormalY=0 NormalZ=1 AngleXU=0 Radius=4 StartAngle=4.71239 EndAngle=6.01862
    g3: ArcOfCircle CenterX=-58.1201 CenterY=-30 CenterZ=0 NormalX=0 NormalY=0 NormalZ=1 AngleXU=0 Radius=86.2201 StartAngle=6.01862 EndAngle=6.28319
    g4: LineSegment StartX=-28.1 StartY=10 StartZ=0 EndX=-28.1 EndY=-30 EndZ=0
    g5: LineSegment StartX=-21.2392 StartY=-55.5 StartZ=0 EndX=21.2392 EndY=-55.5 EndZ=0
    g6: LineSegment StartX=28.1 StartY=-30 StartZ=0 EndX=28.1 EndY=10 EndZ=0
  constraints (16):
    c: Vertical(g4)
    c: Horizontal(g5)
    c: Vertical(g6)
    c: Tangent(g0,g4) = -1.5708
    c: Tangent(g0,g1) = -1.5708
    c: Tangent(g1,g5) = -1.5708
    c: Coincident(g1,g-4)
    c: Tangent(g2,g5) = -1.5708
    c: Tangent(g2,g3) = -1.5708
    c: Coincident(g2,g-5)
    c: Tangent(g3,g6) = -1.5708
    c: Equal(g-6,g3)
    c: Equal(g1,g-4)
    c: Equal(g-3,g0)
    c: Coincident(g6,g-8)
    c: Coincident(g4,g-7)
FEATURE [PartDesign::SubtractivePipe] SubtractivePipe007  label="SL Groove"
  AuxilleryCurvelinear = true
  AuxillerySpineTangent = false
  BaseFeature = -> Pad025
  Binormal = (0,0,0)
  Mode = 0
  Placement = pos=(33.6,0,7e-16) rot=(0,1,0;1.5708rad)
  Profile = -> Sketch138
  Refine = true
  Spine = -> Sketch139
  SpineTangent = false
  Suppressed = false
  Transformation = 0
  Transition = 0
FEATURE [PartDesign::SubShapeBinder] Binder041  label="sl ref ESP slot depth"
  BindCopyOnChange = 0
  BindMode = 0
  ClaimChildren = false
  Context = -> Body025 [Binder041.]
  Fuse = false
  MakeFace = true
  OffsetFill = false
  OffsetIntersection = false
  OffsetJoinType = 0
  OffsetOpenResult = false
  PartialLoad = false
  Refine = true
  Relative = true
  Support = -> [Body021[Sketch115.]]
  _Version = 2
FEATURE [PartDesign::SubShapeBinder] Binder042  label="hs wallsocket interface"
  BindCopyOnChange = 0
  BindMode = 0
  ClaimChildren = false
  Context = -> Body022 [Binder042.]
  Fuse = false
  MakeFace = true
  OffsetFill = false
  OffsetIntersection = false
  OffsetJoinType = 0
  OffsetOpenResult = false
  PartialLoad = false
  Refine = true
  Relative = true
  Support = -> [Body021[Binder003.]]
  _Version = 2
FEATURE [Sketcher::SketchObject] Sketch141
  ArcFitTolerance = 1e-06
  AttachmentOffset = pos=(0,0,-0.1) rot=(0,0,1;0rad)
  AttachmentSupport = -> [XY_Plane022]
  ExternalGeometry = -> [Binder042]
  FullyConstrained = true
  MakeInternals = false
  MapMode = 5
  Placement = pos=(0,0,-0.1) rot=(0,0,1;0rad)
  sketch-geometry (44):
    g0: Circle CenterX=28.1 CenterY=-15.6 CenterZ=0 NormalX=0 NormalY=0 NormalZ=1 AngleXU=0 Radius=1.8
    g1: Circle CenterX=28.1 CenterY=15.6 CenterZ=0 NormalX=0 NormalY=0 NormalZ=1 AngleXU=0 Radius=1.8
    g2: Circle CenterX=-28.1 CenterY=15.6 CenterZ=0 NormalX=0 NormalY=0 NormalZ=1 AngleXU=0 Radius=1.8
    g3: Circle CenterX=-28.1 CenterY=-15.6 CenterZ=0 NormalX=0 NormalY=0 NormalZ=1 AngleXU=0 Radius=1.8
    g4: LineSegment StartX=12.5 StartY=28.6 StartZ=0 EndX=12.5 EndY=26.1 EndZ=0
    g5: LineSegment StartX=13.1 StartY=25.5 StartZ=0 EndX=19.5 EndY=25.5 EndZ=0
    g6: LineSegment StartX=20.1 StartY=26.1 StartZ=0 EndX=20.1 EndY=28.6 EndZ=0
    g7: LineSegment StartX=19.5 StartY=29.2 StartZ=0 EndX=13.1 EndY=29.2 EndZ=0
    g8: ArcOfCircle CenterX=13.1 CenterY=28.6 CenterZ=0 NormalX=0 NormalY=0 NormalZ=1 AngleXU=0 Radius=0.6 StartAngle=1.5708 EndAngle=3.14159
    g9: ArcOfCircle CenterX=13.1 CenterY=26.1 CenterZ=0 NormalX=0 NormalY=0 NormalZ=1 AngleXU=0 Radius=0.6 StartAngle=3.14159 EndAngle=4.71239
    g10: ArcOfCircle CenterX=19.5 CenterY=26.1 CenterZ=0 NormalX=0 NormalY=0 NormalZ=1 AngleXU=0 Radius=0.6 StartAngle=4.71239 EndAngle=6.28319
    g11: ArcOfCircle CenterX=19.5 CenterY=28.6 CenterZ=0 NormalX=0 NormalY=0 NormalZ=1 AngleXU=0 Radius=0.6 StartAngle=8e-16 EndAngle=1.5708
    g12: GeomPoint [constr] X=12.5 Y=29.2 Z=0
    g13: GeomPoint [constr] X=20.1 Y=25.5 Z=0
    g14: LineSegment StartX=-20.1 StartY=28.6 StartZ=0 EndX=-20.1 EndY=26.1 EndZ=0
    g15: LineSegment StartX=-19.5 StartY=25.5 StartZ=0 EndX=-13.1 EndY=25.5 EndZ=0
    g16: LineSegment StartX=-12.5 StartY=26.1 StartZ=0 EndX=-12.5 EndY=28.6 EndZ=0
    g17: LineSegment StartX=-13.1 StartY=29.2 StartZ=0 EndX=-19.5 EndY=29.2 EndZ=0
    g18: ArcOfCircle CenterX=-19.5 CenterY=28.6 CenterZ=0 NormalX=0 NormalY=0 NormalZ=1 AngleXU=0 Radius=0.6 StartAngle=1.5708 EndAngle=3.14159
    g19: ArcOfCircle CenterX=-19.5 CenterY=26.1 CenterZ=0 NormalX=0 NormalY=0 NormalZ=1 AngleXU=0 Radius=0.6 StartAngle=3.14159 EndAngle=4.71239
    g20: ArcOfCircle CenterX=-13.1 CenterY=26.1 CenterZ=0 NormalX=0 NormalY=0 NormalZ=1 AngleXU=0 Radius=0.6 StartAngle=4.71239 EndAngle=6.28319
    g21: ArcOfCircle CenterX=-13.1 CenterY=28.6 CenterZ=0 NormalX=0 NormalY=0 NormalZ=1 AngleXU=0 Radius=0.6 StartAngle=4e-16 EndAngle=1.5708
    g22: GeomPoint [constr] X=-20.1 Y=29.2 Z=0
    g23: GeomPoint [constr] X=-12.5 Y=25.5 Z=0
    g24: LineSegment StartX=19.5 StartY=-25.5 StartZ=0 EndX=13.1 EndY=-25.5 EndZ=0
    g25: LineSegment StartX=12.5 StartY=-26.1 StartZ=0 EndX=12.5 EndY=-28.6 EndZ=0
    g26: LineSegment StartX=13.1 StartY=-29.2 StartZ=0 EndX=19.5 EndY=-29.2 EndZ=0
    g27: LineSegment StartX=20.1 StartY=-28.6 StartZ=0 EndX=20.1 EndY=-26.1 EndZ=0
    g28: ArcOfCircle CenterX=19.5 CenterY=-26.1 CenterZ=0 NormalX=0 NormalY=0 NormalZ=1 AngleXU=0 Radius=0.6 StartAngle=8e-16 EndAngle=1.5708
    g29: ArcOfCircle CenterX=13.1 CenterY=-26.1 CenterZ=0 NormalX=0 NormalY=0 NormalZ=1 AngleXU=0 Radius=0.6 StartAngle=1.5708 EndAngle=3.14159
    g30: ArcOfCircle CenterX=13.1 CenterY=-28.6 CenterZ=0 NormalX=0 NormalY=0 NormalZ=1 AngleXU=0 Radius=0.6 StartAngle=3.14159 EndAngle=4.71239
    g31: ArcOfCircle CenterX=19.5 CenterY=-28.6 CenterZ=0 NormalX=0 NormalY=0 NormalZ=1 AngleXU=0 Radius=0.6 StartAngle=4.71239 EndAngle=6.28319
    g32: GeomPoint [constr] X=20.1 Y=-25.5 Z=0
    g33: GeomPoint [constr] X=12.5 Y=-29.2 Z=0
    g34: LineSegment StartX=-19.5 StartY=-29.2 StartZ=0 EndX=-13.1 EndY=-29.2 EndZ=0
    g35: LineSegment StartX=-12.5 StartY=-28.6 StartZ=0 EndX=-12.5 EndY=-26.1 EndZ=0
    g36: LineSegment StartX=-13.1 StartY=-25.5 StartZ=0 EndX=-19.5 EndY=-25.5 EndZ=0
    g37: LineSegment StartX=-20.1 StartY=-26.1 StartZ=0 EndX=-20.1 EndY=-28.6 EndZ=0
    g38: ArcOfCircle CenterX=-19.5 CenterY=-28.6 CenterZ=0 NormalX=0 NormalY=0 NormalZ=1 AngleXU=0 Radius=0.6 StartAngle=3.14159 EndAngle=4.71239
    g39: ArcOfCircle CenterX=-13.1 CenterY=-28.6 CenterZ=0 NormalX=0 NormalY=0 NormalZ=1 AngleXU=0 Radius=0.6 StartAngle=4.71239 EndAngle=6.28319
    g40: ArcOfCircle CenterX=-13.1 CenterY=-26.1 CenterZ=0 NormalX=0 NormalY=0 NormalZ=1 AngleXU=0 Radius=0.6 StartAngle=1.226e-13 EndAngle=1.5708
    g41: ArcOfCircle CenterX=-19.5 CenterY=-26.1 CenterZ=0 NormalX=0 NormalY=0 NormalZ=1 AngleXU=0 Radius=0.6 StartAngle=1.5708 EndAngle=3.14159
    g42: GeomPoint [constr] X=-20.1 Y=-29.2 Z=0
    g43: GeomPoint [constr] X=-12.5 Y=-25.5 Z=0
  constraints (96):
    c: Coincident(g0,g-10)
    c: Coincident(g1,g-3)
    c: Coincident(g2,g-6)
    c: Coincident(g3,g-7)
    c: Equal(g3,g2)
    c: Equal(g2,g1)
    c: Equal(g1,g0)
    c: Diameter(g1) = 3.6
    c: Tangent(g4,g8) = -1.5708
    c: Tangent(g4,g9) = -1.5708
    c: Tangent(g5,g9) = -1.5708
    c: Tangent(g5,g10) = -1.5708
    c: Tangent(g6,g10) = -1.5708
    c: Tangent(g6,g11) = -1.5708
    c: Tangent(g7,g11) = -1.5708
    c: Tangent(g7,g8) = -1.5708
    c: Vertical(g4)
    c: Vertical(g6)
    c: Horizontal(g5)
    c: Horizontal(g7)
    c: Equal(g8,g9)
    c: Equal(g9,g10)
    c: PointOnObject(g12,g4)
    c: PointOnObject(g12,g7)
    c: PointOnObject(g13,g5)
    c: PointOnObject(g13,g6)
    c: Coincident(g11,g-4)
    c: Coincident(g8,g-4)
    c: DistanceY(g6,g6) = 2.5
    c: Tangent(g14,g18) = -1.5708
    c: Tangent(g14,g19) = -1.5708
    c: Tangent(g15,g19) = -1.5708
    c: Tangent(g15,g20) = -1.5708
    c: Tangent(g16,g20) = -1.5708
    c: Tangent(g16,g21) = -1.5708
    c: Tangent(g17,g21) = -1.5708
    c: Tangent(g17,g18) = -1.5708
    c: Vertical(g14)
    c: Vertical(g16)
    c: Horizontal(g15)
    c: Horizontal(g17)
    c: Equal(g18,g19)
    c: Equal(g19,g20)
    c: PointOnObject(g22,g14)
    c: PointOnObject(g22,g17)
    c: PointOnObject(g23,g15)
    c: PointOnObject(g23,g16)
    c: Coincident(g21,g-5)
    c: Coincident(g18,g-5)
    c: Radius(g11) = 0.6
    c: Equal(g11,g21)
    c: Equal(g16,g6)
    c: Tangent(g24,g28) = -1.5708
    c: Tangent(g24,g29) = -1.5708
    c: Tangent(g25,g29) = -1.5708
    c: Tangent(g25,g30) = -1.5708
    c: Tangent(g26,g30) = -1.5708
    c: Tangent(g26,g31) = -1.5708
    c: Tangent(g27,g31) = -1.5708
    c: Tangent(g27,g28) = -1.5708
    c: Horizontal(g24)
    c: Horizontal(g26)
    c: Vertical(g25)
    c: Vertical(g27)
    c: Equal(g28,g29)
    c: Equal(g29,g30)
    c: PointOnObject(g32,g24)
    c: PointOnObject(g32,g27)
    c: PointOnObject(g33,g25)
    c: PointOnObject(g33,g26)
    c: Coincident(g30,g-9)
    c: Coincident(g31,g-9)
    c: Equal(g28,g11)
    c: Equal(g6,g27)
    c: Tangent(g34,g38) = -1.5708
    c: Tangent(g34,g39) = -1.5708
    c: Tangent(g35,g39) = -1.5708
    c: Tangent(g35,g40) = -1.5708
    c: Tangent(g36,g40) = -1.5708
    c: Tangent(g36,g41) = -1.5708
    c: Tangent(g37,g41) = -1.5708
    c: Tangent(g37,g38) = -1.5708
    c: Horizontal(g34)
    c: Horizontal(g36)
    c: Vertical(g35)
    c: Vertical(g37)
    c: Equal(g39,g40)
    c: Equal(g40,g41)
    c: PointOnObject(g42,g34)
    c: PointOnObject(g42,g37)
    c: PointOnObject(g43,g35)
    c: PointOnObject(g43,g36)
    c: Coincident(g39,g-8)
    c: Coincident(g38,g-8)
    c: Equal(g40,g11)
    c: Equal(g6,g35)
FEATURE [PartDesign::Pocket] Pocket043
  BaseFeature = -> Chamfer
  Direction = (0,0,-1)
  Length = 5
  Length2 = 5
  Placement = pos=(30.6,0,0) rot=(0,1,0;1.5708rad)
  Profile = -> Sketch141
  ReferenceAxis = -> Sketch141 [N_Axis]
  Refine = true
  Reversed = true
  Suppressed = false
  Type = 1
FEATURE [PartDesign::Pocket] Pocket035  label="HS Relay slot"
  BaseFeature = -> Pocket043
  Direction = (0,1,0)
  Length = 0
  Length2 = 5
  Placement = pos=(30.6,0,0) rot=(0,1,0;1.5708rad)
  Profile = -> Sketch124
  ReferenceAxis = -> Sketch124 [N_Axis]
  Refine = true
  Suppressed = false
  Type = 3
  UpToFace = -> DatumPlane010
FEATURE [PartDesign::Pocket] Pocket036  label="HS Relay cable slot"
  BaseFeature = -> Pocket035
  Direction = (0,0,-1)
  Length = 5
  Length2 = 5
  Placement = pos=(30.6,0,0) rot=(0,1,0;1.5708rad)
  Profile = -> Sketch125
  ReferenceAxis = -> Sketch125 [N_Axis]
  Refine = true
  Reversed = true
  Suppressed = false
  Type = 1
FEATURE [PartDesign::Pocket] Pocket037  label="HS ULN2003 slot"
  BaseFeature = -> Pocket036
  Direction = (0,1,0)
  Length = 0
  Length2 = 5
  Placement = pos=(30.6,0,0) rot=(0,1,0;1.5708rad)
  Profile = -> Sketch126
  ReferenceAxis = -> Sketch126 [N_Axis]
  Refine = true
  Suppressed = false
  Type = 3
  UpToFace = -> DatumPlane010
FEATURE [PartDesign::Pocket] Pocket038  label="HS ESP slot"
  BaseFeature = -> Pocket037
  Direction = (0,1,0)
  Length = 0
  Length2 = 5
  Placement = pos=(30.6,0,0) rot=(0,1,0;1.5708rad)
  Profile = -> Sketch127
  ReferenceAxis = -> Sketch127 [N_Axis]
  Refine = true
  Suppressed = false
  Type = 3
  UpToFace = -> DatumPlane010
FEATURE [PartDesign::Pocket] Pocket039  label="HS USB slot"
  BaseFeature = -> Pocket038
  Direction = (0,1,-2e-16)
  Length = 5
  Length2 = 5
  Placement = pos=(30.6,0,0) rot=(0,1,0;1.5708rad)
  Profile = -> Sketch128
  ReferenceAxis = -> Sketch128 [N_Axis]
  Refine = true
  Reversed = true
  Suppressed = false
  Type = 1
FEATURE [PartDesign::Pocket] Pocket040  label="HS Nut slot R"
  BaseFeature = -> Pocket039
  Direction = (0,0,-1)
  Length = 0
  Length2 = 5
  Placement = pos=(30.6,0,0) rot=(0,1,0;1.5708rad)
  Profile = -> Sketch131
  ReferenceAxis = -> Sketch131 [N_Axis]
  Refine = true
  Suppressed = false
  Type = 3
  UpToFace = -> DatumPlane014
FEATURE [PartDesign::Pocket] Pocket041  label="HS Screw hole M4 R"
  BaseFeature = -> Pocket040
  Direction = (0,0,-1)
  Length = 5
  Length2 = 40
  Placement = pos=(30.6,0,0) rot=(0,1,0;1.5708rad)
  Profile = -> Sketch132
  ReferenceAxis = -> Sketch132 [N_Axis]
  Refine = true
  Suppressed = false
  Type = 4
FEATURE [PartDesign::Mirrored] Mirrored008  label="HS Nut and screw L"
  BaseFeature = -> Pocket041
  MirrorPlane = -> YZ_Plane023
  Originals = -> [Pocket040,Pocket041]
  Placement = pos=(30.6,0,0) rot=(0,1,0;1.5708rad)
  Refine = true
  Suppressed = false
  TransformMode = 0
FEATURE [PartDesign::SubShapeBinder] Binder043  label="sl ref cable"
  BindCopyOnChange = 0
  BindMode = 0
  ClaimChildren = false
  Context = -> Body025 [Binder043.]
  Fuse = false
  MakeFace = true
  OffsetFill = false
  OffsetIntersection = false
  OffsetJoinType = 0
  OffsetOpenResult = false
  PartialLoad = false
  Refine = true
  Relative = true
  Support = -> [Body021[Binder008.]]
  _Version = 2
FEATURE [PartDesign::Plane] DatumPlane021  label="sl pln cable crs"
  AttachmentSupport = -> [Binder043]
  Length = 79.7506
  MapMode = 7
  Placement = pos=(0,18,-4e-15) rot=(0,0,1;0rad)
  ResizeMode = 0
  Width = 71.1506
FEATURE [Sketcher::SketchObject] Sketch142  label="sl cable crs"
  ArcFitTolerance = 1e-06
  AttachmentSupport = -> [DatumPlane021]
  ExternalGeometry = -> [Binder043]
  FullyConstrained = true
  MakeInternals = false
  MapMode = 5
  Placement = pos=(0,18,-4e-15) rot=(0,0,1;0rad)
  sketch-geometry (4):
    g0: ArcOfCircle CenterX=0 CenterY=1.2 CenterZ=0 NormalX=0 NormalY=0 NormalZ=1 AngleXU=0 Radius=1.8 StartAngle=1e-16 EndAngle=3.14159
    g1: ArcOfCircle CenterX=0 CenterY=-4.8 CenterZ=0 NormalX=0 NormalY=0 NormalZ=1 AngleXU=0 Radius=1.8 StartAngle=3.14159 EndAngle=6.28319
    g2: LineSegment StartX=1.8 StartY=1.2 StartZ=0 EndX=1.8 EndY=-4.8 EndZ=0
    g3: LineSegment StartX=-1.8 StartY=1.2 StartZ=0 EndX=-1.8 EndY=-4.8 EndZ=0
  constraints (9):
    c: Tangent(g0,g2) = 1.5708
    c: Tangent(g0,g3) = -1.5708
    c: Tangent(g1,g2) = 1.5708
    c: Tangent(g1,g3) = -1.5708
    c: Equal(g0,g1)
    c: Vertical(g2)
    c: DistanceY(g2,g2) = 6
    c: Equal(g-3,g0)
    c: Coincident(g0,g-3)
FEATURE [PartDesign::SubShapeBinder] Binder044  label="sh ref cable"
  BindCopyOnChange = 0
  BindMode = 0
  ClaimChildren = false
  Context = -> Body024 [Binder044.]
  Fuse = false
  MakeFace = true
  OffsetFill = false
  OffsetIntersection = false
  OffsetJoinType = 0
  OffsetOpenResult = false
  PartialLoad = false
  Refine = true
  Relative = true
  Support = -> [Body021[Binder008.]]
  _Version = 2
FEATURE [PartDesign::Plane] DatumPlane022  label="sh pln cable crs"
  AttachmentSupport = -> [Binder044]
  Length = 79.7506
  MapMode = 7
  Placement = pos=(0,18,-4e-15) rot=(0,0,1;0rad)
  ResizeMode = 0
  Width = 71.1506
FEATURE [Sketcher::SketchObject] Sketch144  label="sh cable crs"
  ArcFitTolerance = 1e-06
  AttachmentSupport = -> [DatumPlane022]
  ExternalGeometry = -> [Binder044]
  FullyConstrained = true
  MakeInternals = false
  MapMode = 5
  Placement = pos=(0,18,-4e-15) rot=(0,0,1;0rad)
  sketch-geometry (4):
    g0: ArcOfCircle CenterX=-1e-16 CenterY=-1.2 CenterZ=0 NormalX=0 NormalY=0 NormalZ=1 AngleXU=0 Radius=1.8 StartAngle=3.14159 EndAngle=6.28319
    g1: ArcOfCircle CenterX=0 CenterY=4.8 CenterZ=0 NormalX=0 NormalY=0 NormalZ=1 AngleXU=0 Radius=1.8 StartAngle=0 EndAngle=3.14159
    g2: LineSegment StartX=-1.8 StartY=-1.2 StartZ=0 EndX=-1.8 EndY=4.8 EndZ=0
    g3: LineSegment StartX=1.8 StartY=-1.2 StartZ=0 EndX=1.8 EndY=4.8 EndZ=0
  constraints (9):
    c: Tangent(g0,g2) = 1.5708
    c: Tangent(g0,g3) = -1.5708
    c: Tangent(g1,g2) = 1.5708
    c: Tangent(g1,g3) = -1.5708
    c: Equal(g0,g1)
    c: Vertical(g3)
    c: DistanceY(g3,g3) = 6
    c: Coincident(g0,g-3)
    c: Equal(g0,g-3)
FEATURE [PartDesign::SubShapeBinder] Binder045  label="sk ref wall socket mount"
  BindCopyOnChange = 0
  BindMode = 0
  ClaimChildren = false
  Context = -> Body021 [Binder045.]
  Fuse = false
  MakeFace = true
  OffsetFill = false
  OffsetIntersection = false
  OffsetJoinType = 0
  OffsetOpenResult = false
  PartialLoad = false
  Refine = true
  Relative = true
  Support = -> [Body013[Fillet001.Face123,Fillet001.Face127,Fillet001.Face113,Fillet001.Face106,Fillet001.Face107,Fillet001.Face116,Fillet001.Face117,Fillet001.Face97]]
  _Version = 2
FEATURE [PartDesign::Plane] DatumPlane023  label="sk pln wall socket mount"
  AttachmentSupport = -> [Binder045]
  Length = 60
  MapMode = 5
  Placement = pos=(0,0,0) rot=(1,0,0;3.14159rad)
  ResizeMode = 0
  Width = 60
FEATURE [Sketcher::SketchObject] Sketch146  label="sk wall socket mount"
  ArcFitTolerance = 1e-06
  AttachmentSupport = -> [DatumPlane023]
  ExternalGeometry = -> [Binder045]
  FullyConstrained = true
  MakeInternals = false
  MapMode = 5
  Placement = pos=(0,0,0) rot=(1,0,0;3.14159rad)
  sketch-geometry (10):
    g0: LineSegment StartX=-14.7 StartY=8.5 StartZ=0 EndX=-22 EndY=8.5 EndZ=0
    g1: LineSegment StartX=-24.95 StartY=5.55 StartZ=0 EndX=-24.95 EndY=-5.94441 EndZ=0
    g2: LineSegment StartX=-22 StartY=-8.89441 StartZ=0 EndX=-14.7 EndY=-8.89441 EndZ=0
    g3: LineSegment StartX=-11.75 StartY=-5.94441 StartZ=0 EndX=-11.75 EndY=5.55 EndZ=0
    g4: ArcOfCircle CenterX=-14.7 CenterY=5.55 CenterZ=0 NormalX=0 NormalY=0 NormalZ=1 AngleXU=0 Radius=2.95 StartAngle=8e-16 EndAngle=1.5708
    g5: ArcOfCircle CenterX=-22 CenterY=5.55 CenterZ=0 NormalX=0 NormalY=0 NormalZ=1 AngleXU=0 Radius=2.95 StartAngle=1.5708 EndAngle=3.14159
    g6: ArcOfCircle CenterX=-22 CenterY=-5.94441 CenterZ=0 NormalX=0 NormalY=0 NormalZ=1 AngleXU=0 Radius=2.95 StartAngle=3.14159 EndAngle=4.71239
    g7: ArcOfCircle CenterX=-14.7 CenterY=-5.94441 CenterZ=0 NormalX=0 NormalY=0 NormalZ=1 AngleXU=0 Radius=2.95 StartAngle=4.71239 EndAngle=6.28319
    g8: GeomPoint [constr] X=-11.75 Y=8.5 Z=0
    g9: GeomPoint [constr] X=-24.95 Y=-8.89441 Z=0
  constraints (24):
    c: Tangent(g0,g4) = -1.5708
    c: Tangent(g0,g5) = -1.5708
    c: Tangent(g1,g5) = -1.5708
    c: Tangent(g1,g6) = -1.5708
    c: Tangent(g2,g6) = -1.5708
    c: Tangent(g2,g7) = -1.5708
    c: Tangent(g3,g7) = -1.5708
    c: Tangent(g3,g4) = -1.5708
    c: Horizontal(g0)
    c: Horizontal(g2)
    c: Vertical(g1)
    c: Vertical(g3)
    c: Equal(g4,g5)
    c: Equal(g5,g6)
    c: Equal(g6,g7)
    c: PointOnObject(g8,g0)
    c: PointOnObject(g8,g3)
    c: PointOnObject(g9,g1)
    c: PointOnObject(g9,g2)
    c: Horizontal(g-5,g3)
    c: Vertical(g-4,g2)
    c: Distance(g-6,g0) = 1
    c: Distance(g-3,g1) = 1
    c: Distance(g-5,g3) = 1
FEATURE [PartDesign::Body] Body021  label="Skeleton"
  AllowCompound = false
  Group = -> [Binder003,Binder004,Binder005,Binder006,Binder007,Binder008,Sketch106,Sketch107,Sketch108,Sketch109,Sketch110,Sketch111,Sketch112,Sketch113,Binder017,Sketch114,Sketch115,Sketch116,Binder022,DatumPoint002,Sketch120,DatumPlane006,DatumPlane007,Sketch121,DatumPlane008,Sketch122,Sketch123,Sketch129,Binder045,Sketch146,DatumPlane023]
  Origin = -> Origin021
FEATURE [PartDesign::SubShapeBinder] Binder046  label="hs wall socket mount"
  BindCopyOnChange = 0
  BindMode = 0
  ClaimChildren = false
  Context = -> Body022 [Binder046.]
  Fuse = false
  MakeFace = true
  OffsetFill = false
  OffsetIntersection = false
  OffsetJoinType = 0
  OffsetOpenResult = false
  PartialLoad = false
  Refine = true
  Relative = true
  Support = -> [Body021[Sketch146.]]
  _Version = 2
FEATURE [Sketcher::SketchObject] Sketch147
  ArcFitTolerance = 1e-06
  AttachmentSupport = -> [Binder046]
  ExternalGeometry = -> [Binder046]
  FullyConstrained = true
  MakeInternals = false
  MapMode = 5
  sketch-geometry (10):
    g0: LineSegment StartX=-22 StartY=-8.5 StartZ=0 EndX=-14.7 EndY=-8.5 EndZ=0
    g1: LineSegment StartX=-11.75 StartY=-5.55 StartZ=0 EndX=-11.75 EndY=5.94441 EndZ=0
    g2: LineSegment StartX=-14.7 StartY=8.89441 StartZ=0 EndX=-22 EndY=8.89441 EndZ=0
    g3: LineSegment StartX=-24.95 StartY=5.94441 StartZ=0 EndX=-24.95 EndY=-5.55 EndZ=0
    g4: ArcOfCircle CenterX=-22 CenterY=-5.55 CenterZ=0 NormalX=0 NormalY=0 NormalZ=1 AngleXU=0 Radius=2.95 StartAngle=3.14159 EndAngle=4.71239
    g5: ArcOfCircle CenterX=-14.7 CenterY=-5.55 CenterZ=0 NormalX=0 NormalY=0 NormalZ=1 AngleXU=0 Radius=2.95 StartAngle=4.71239 EndAngle=6.28319
    g6: ArcOfCircle CenterX=-14.7 CenterY=5.94441 CenterZ=0 NormalX=0 NormalY=0 NormalZ=1 AngleXU=0 Radius=2.95 StartAngle=3.4e-15 EndAngle=1.5708
    g7: ArcOfCircle CenterX=-22 CenterY=5.94441 CenterZ=0 NormalX=0 NormalY=0 NormalZ=1 AngleXU=0 Radius=2.95 StartAngle=1.5708 EndAngle=3.14159
    g8: GeomPoint [constr] X=-24.95 Y=-8.5 Z=0
    g9: GeomPoint [constr] X=-11.75 Y=8.89441 Z=0
  constraints (22):
    c: Tangent(g0,g4) = -1.5708
    c: Tangent(g0,g5) = -1.5708
    c: Tangent(g1,g5) = -1.5708
    c: Tangent(g1,g6) = -1.5708
    c: Tangent(g2,g6) = -1.5708
    c: Tangent(g2,g7) = -1.5708
    c: Tangent(g3,g7) = -1.5708
    c: Tangent(g3,g4) = -1.5708
    c: Horizontal(g0)
    c: Horizontal(g2)
    c: Vertical(g1)
    c: Vertical(g3)
    c: Equal(g4,g5)
    c: Equal(g5,g6)
    c: Equal(g6,g7)
    c: PointOnObject(g8,g0)
    c: PointOnObject(g8,g3)
    c: PointOnObject(g9,g1)
    c: PointOnObject(g9,g2)
    c: Coincident(g6,g-3)
    c: Coincident(g4,g-4)
    c: Equal(g-3,g6)
FEATURE [PartDesign::Pocket] Pocket044  label="HS Wall socket mount R"
  BaseFeature = -> Mirrored008
  Direction = (0,0,-1)
  Length = 5
  Length2 = 5
  Placement = pos=(30.6,0,0) rot=(0,1,0;1.5708rad)
  Profile = -> Sketch147
  ReferenceAxis = -> Sketch147 [N_Axis]
  Refine = true
  Reversed = true
  Suppressed = false
  Type = 1
FEATURE [PartDesign::Mirrored] Mirrored011  label="HS Wall socket mount L"
  BaseFeature = -> Pocket044
  MirrorPlane = -> YZ_Plane023
  Originals = -> [Pocket044]
  Placement = pos=(30.6,0,0) rot=(0,1,0;1.5708rad)
  Refine = true
  Suppressed = false
  TransformMode = 0
FEATURE [PartDesign::SubShapeBinder] Binder047  label="hs ref screw hole"
  BindCopyOnChange = 0
  BindMode = 0
  ClaimChildren = false
  Context = -> Body022 [Binder047.]
  Fuse = false
  MakeFace = true
  OffsetFill = false
  OffsetIntersection = false
  OffsetJoinType = 0
  OffsetOpenResult = false
  PartialLoad = false
  Refine = true
  Relative = true
  Support = -> [Body023[Sketch003.]]
  _Version = 2
FEATURE [PartDesign::Groove] Groove011  label="HS Screw hole L"
  Angle = 360
  Angle2 = 60
  Axis = (0,1,-4e-16)
  Base = (21,3,-44)
  BaseFeature = -> Mirrored011
  Placement = pos=(30.6,0,0) rot=(0,1,0;1.5708rad)
  Profile = -> Binder047
  ReferenceAxis = -> Binder047 [Edge8]
  Refine = true
  Suppressed = false
  Type = 0
FEATURE [PartDesign::Mirrored] Mirrored012  label="HS Screw hole R"
  BaseFeature = -> Groove011
  MirrorPlane = -> YZ_Plane023
  Originals = -> [Groove011]
  Placement = pos=(30.6,0,0) rot=(0,1,0;1.5708rad)
  Refine = true
  Suppressed = false
  TransformMode = 0
FEATURE [PartDesign::Chamfer] Chamfer001  label="HS Screw hole chamfer"
  Angle = 45
  Base = -> Mirrored012 [Edge491,Edge493,Edge494,Edge481,Edge482,Edge489]
  BaseFeature = -> Mirrored012
  ChamferType = 0
  FlipDirection = false
  Placement = pos=(30.6,0,0) rot=(0,1,0;1.5708rad)
  Refine = true
  Size = 0.5
  Size2 = 1
  SupportTransform = false
  Suppressed = false
  UseAllEdges = false
FEATURE [PartDesign::Body] Body022  label="Housing"
  AllowCompound = false
  Group = -> [Binder009,Binder010,Binder011,Binder012,Binder014,Binder015,Binder016,Binder018,Binder019,Binder020,Binder021,DatumPlane004,DatumPlane005,Sketch117,Pad022,Sketch118,Pocket033,Fillet,Chamfer,DatumPlane009,DatumPlane010,Sketch124,Sketch141,Pocket043,Pocket035,Sketch125,Binder023,Binder024,Pocket036,Binder025,DatumPlane011,Sketch126,Pocket037,DatumPlane012,Sketch127,Pocket038,Sketch128,Pocket039,+16 more]
  Origin = -> Origin022
  Tip = -> Chamfer001
FEATURE [PartDesign::Plane] DatumPlane024  label="sh pln trj"
  AttachmentSupport = -> [Binder044,XZ_Plane024]
  Length = 101.204
  MapMode = 6
  Placement = pos=(0,18,-4e-15) rot=(0.57735,-0.57735,0.57735;2.0944rad)
  ResizeMode = 0
  Width = 82.4042
FEATURE [Sketcher::SketchObject] Sketch145  label="sh cable trj"
  ArcFitTolerance = 1e-06
  AttachmentSupport = -> [DatumPlane024]
  ExternalGeometry = -> [Binder044]
  FullyConstrained = true
  MakeInternals = false
  MapMode = 5
  Placement = pos=(0,18,-4e-15) rot=(0.57735,-0.57735,0.57735;2.0944rad)
  sketch-geometry (3):
    g0: ArcOfCircle CenterX=-18 CenterY=12 CenterZ=0 NormalX=0 NormalY=0 NormalZ=1 AngleXU=0 Radius=12 StartAngle=3.14159 EndAngle=4.71239
    g1: LineSegment StartX=0 StartY=0 StartZ=0 EndX=-18 EndY=-1.403e-13 EndZ=0
    g2: LineSegment StartX=-30 StartY=50 StartZ=0 EndX=-30 EndY=12 EndZ=0
  constraints (6):
    c: Coincident(g0,g-3)
    c: Coincident(g1,g-1)
    c: Coincident(g2,g-4)
    c: Tangent(g0,g2) = -1.5708
    c: Tangent(g0,g1) = 1.5708
    c: Equal(g0,g-3)
FEATURE [PartDesign::SubtractivePipe] SubtractivePipe009  label="SH Cable duct"
  AuxilleryCurvelinear = true
  AuxillerySpineTangent = false
  BaseFeature = -> AdditivePipe004
  Binormal = (0,0,0)
  Mode = 0
  Placement = pos=(33.6,0,7e-16) rot=(0,1,0;1.5708rad)
  Profile = -> Sketch144
  Refine = true
  Spine = -> Sketch145
  SpineTangent = false
  Suppressed = false
  Transformation = 0
  Transition = 0
FEATURE [PartDesign::Body] Body024  label="Separation housing"
  AllowCompound = false
  Group = -> [Binder027,Binder028,Binder029,DatumPlane016,DatumPlane017,Sketch133,Pad024,Binder031,Binder032,Sketch135,Sketch136,AdditivePipe004,Binder044,DatumPlane022,Sketch144,Sketch145,SubtractivePipe009,DatumPlane024]
  Origin = -> Origin024
  Tip = -> SubtractivePipe009
FEATURE [Part::MultiCommon] Common  label="Housing base"
  Shapes = -> [Body022,Body024]
FEATURE [PartDesign::Plane] DatumPlane025  label="sk pln cable trj"
  AttachmentSupport = -> [Binder043,XZ_Plane025]
  Length = 101.204
  MapMode = 6
  Placement = pos=(0,18,-4e-15) rot=(0.57735,-0.57735,0.57735;2.0944rad)
  ResizeMode = 0
  Width = 82.4042
FEATURE [Sketcher::SketchObject] Sketch143  label="sl cable trj"
  ArcFitTolerance = 1e-06
  AttachmentSupport = -> [DatumPlane025]
  ExternalGeometry = -> [Binder043]
  FullyConstrained = true
  MakeInternals = false
  MapMode = 5
  Placement = pos=(0,18,-4e-15) rot=(0.57735,-0.57735,0.57735;2.0944rad)
  sketch-geometry (3):
    g0: ArcOfCircle CenterX=-18 CenterY=12 CenterZ=0 NormalX=0 NormalY=0 NormalZ=1 AngleXU=0 Radius=12 StartAngle=3.14159 EndAngle=4.71239
    g1: LineSegment StartX=0 StartY=0 StartZ=0 EndX=-18 EndY=0 EndZ=0
    g2: LineSegment StartX=-30 StartY=50 StartZ=0 EndX=-30 EndY=12 EndZ=0
  constraints (6):
    c: Coincident(g0,g-3)
    c: Coincident(g1,g-1)
    c: Coincident(g2,g-4)
    c: Tangent(g0,g2) = -1.5708
    c: Tangent(g0,g1) = 1.5708
    c: Equal(g0,g-3)
FEATURE [PartDesign::SubtractivePipe] SubtractivePipe008  label="SL Cable duct"
  AuxilleryCurvelinear = true
  AuxillerySpineTangent = false
  BaseFeature = -> SubtractivePipe007
  Binormal = (0,0,0)
  Mode = 0
  Placement = pos=(33.6,0,7e-16) rot=(0,1,0;1.5708rad)
  Profile = -> Sketch142
  Refine = true
  Spine = -> Sketch143
  SpineTangent = false
  Suppressed = false
  Transformation = 0
  Transition = 0
FEATURE [PartDesign::Body] Body025  label="Separation lid"
  AllowCompound = false
  Group = -> [Binder034,Binder035,Binder036,Binder037,Binder038,Binder039,DatumPlane018,DatumPlane019,Sketch137,Pad025,Sketch138,Sketch139,SubtractivePipe007,Binder041,Binder043,DatumPlane021,Sketch142,Sketch143,SubtractivePipe008,DatumPlane025]
  Origin = -> Origin025
  Tip = -> SubtractivePipe008
FEATURE [Part::MultiCommon] Common001  label="Lid"
  Shapes = -> [Body025,Body022]
FEATURE [PartDesign::SubShapeBinder] Binder048  label="er ref ESP"
  BindCopyOnChange = 0
  BindMode = 0
  ClaimChildren = false
  Context = -> Body026 [Binder048.]
  Fuse = false
  MakeFace = true
  OffsetFill = false
  OffsetIntersection = false
  OffsetJoinType = 0
  OffsetOpenResult = false
  PartialLoad = false
  Refine = true
  Relative = true
  Support = -> [Compound004[Face993,Face960,Face422,Face413,Face128]]
  _Version = 2
FEATURE [PartDesign::SubShapeBinder] Binder049  label="er ref separation"
  BindCopyOnChange = 0
  BindMode = 0
  ClaimChildren = false
  Context = -> Body026 [Binder049.]
  Fuse = false
  MakeFace = true
  OffsetFill = false
  OffsetIntersection = false
  OffsetJoinType = 0
  OffsetOpenResult = false
  PartialLoad = false
  Refine = true
  Relative = true
  Support = -> [Body021[Sketch110.]]
  _Version = 2
FEATURE [PartDesign::SubShapeBinder] Binder050  label="er ref ESP slot"
  BindCopyOnChange = 0
  BindMode = 0
  ClaimChildren = false
  Context = -> Body026 [Binder050.]
  Fuse = false
  MakeFace = true
  OffsetFill = false
  OffsetIntersection = false
  OffsetJoinType = 0
  OffsetOpenResult = false
  PartialLoad = false
  Refine = true
  Relative = true
  Support = -> [Body021[Sketch113.]]
  _Version = 2
FEATURE [Sketcher::SketchObject] Sketch148
  ArcFitTolerance = 1e-06
  AttachmentSupport = -> [YZ_Plane027]
  ExternalGeometry = -> [Binder048,Binder049,Binder050]
  FullyConstrained = true
  MakeInternals = false
  MapMode = 5
  Placement = pos=(0,0,0) rot=(0.57735,0.57735,0.57735;2.0944rad)
  sketch-geometry (16):
    g0: LineSegment StartX=-2.4 StartY=-47.715 StartZ=0 EndX=-2.4 EndY=-48.765 EndZ=0
    g1: LineSegment StartX=-2.4 StartY=-54.25 StartZ=0 EndX=16 EndY=-54.25 EndZ=0
    g2: LineSegment StartX=16 StartY=-54.25 StartZ=0 EndX=16 EndY=-47.715 EndZ=0
    g3: LineSegment StartX=16 StartY=-47.715 StartZ=0 EndX=-2.4 EndY=-47.715 EndZ=0
    g4: LineSegment StartX=2.8 StartY=-50.965 StartZ=0 EndX=2.8 EndY=-48.765 EndZ=0
    g5: LineSegment StartX=2.8 StartY=-48.765 StartZ=0 EndX=-2.4 EndY=-48.765 EndZ=0
    g6: LineSegment StartX=-2.4 StartY=-53.2 StartZ=0 EndX=9.1 EndY=-53.2 EndZ=0
    g7: LineSegment StartX=9.3 StartY=-53 StartZ=0 EndX=9.3 EndY=-51.165 EndZ=0
    g8: LineSegment StartX=9.1 StartY=-50.965 StartZ=0 EndX=2.8 EndY=-50.965 EndZ=0
    g9: LineSegment StartX=-2.4 StartY=-53.2 StartZ=0 EndX=-2.4 EndY=-54.25 EndZ=0
    g10: Circle [constr] CenterX=2.6 CenterY=-48.965 CenterZ=0 NormalX=0 NormalY=0 NormalZ=1 AngleXU=0 Radius=0.2
    g11: Circle [constr] CenterX=2.6 CenterY=-51.165 CenterZ=0 NormalX=0 NormalY=0 NormalZ=1 AngleXU=0 Radius=0.2
    g12: ArcOfCircle CenterX=9.1 CenterY=-51.165 CenterZ=0 NormalX=0 NormalY=0 NormalZ=1 AngleXU=0 Radius=0.2 StartAngle=1.4e-15 EndAngle=1.5708
    g13: GeomPoint [constr] X=9.3 Y=-50.965 Z=0
    g14: ArcOfCircle CenterX=9.1 CenterY=-53 CenterZ=0 NormalX=0 NormalY=0 NormalZ=1 AngleXU=0 Radius=0.2 StartAngle=4.71239 EndAngle=6.28319
    g15: GeomPoint [constr] X=9.3 Y=-53.2 Z=0
  constraints (41):
    c: Coincident(g9,g1)
    c: Coincident(g1,g2)
    c: Coincident(g2,g3)
    c: Coincident(g3,g0)
    c: Vertical(g0)
    c: Vertical(g2)
    c: Horizontal(g1)
    c: Horizontal(g3)
    c: Coincident(g4,g5)
    c: Vertical(g4)
    c: Horizontal(g5)
    c: Vertical(g7)
    c: Horizontal(g6)
    c: Horizontal(g8)
    c: Coincident(g4,g8)
    c: Coincident(g5,g0)
    c: Coincident(g6,g9)
    c: PointOnObject(g10,g-8)
    c: PointOnObject(g10,g-3)
    c: Diameter(g10) = 0.4
    c: Tangent(g10,g5)
    c: Tangent(g10,g4)
    c: Coincident(g11,g-8)
    c: Tangent(g4,g11)
    c: Tangent(g11,g8)
    c: PointOnObject(g13,g8)
    c: PointOnObject(g13,g7)
    c: Tangent(g8,g12) = -1.5708
    c: Tangent(g7,g12) = -1.5708
    c: PointOnObject(g15,g7)
    c: PointOnObject(g15,g6)
    c: Tangent(g7,g14) = -1.5708
    c: Tangent(g6,g14) = -1.5708
    c: Coincident(g14,g-6)
    c: Coincident(g12,g-5)
    c: Distance(g0,g-8) = 5
    c: PointOnObject(g6,g0)
    c: Vertical(g9)
    c: Distance(g-9,g1) = 1
    c: Equal(g9,g0)
    c: PointOnObject(g1,g-7)
FEATURE [PartDesign::Pad] Pad026
  Direction = (1,0,0)
  Length = 12
  Length2 = 10
  Midplane = true
  Placement = pos=(0,0,0) rot=(1,1,1;2.0944rad)
  Profile = -> Sketch148
  ReferenceAxis = -> Sketch148 [N_Axis]
  Refine = true
  Suppressed = false
  Type = 0
FEATURE [PartDesign::Chamfer] Chamfer002
  Angle = 45
  Base = -> Pad026 [Edge15,Edge3,Edge4,Edge16,Edge9,Edge10]
  BaseFeature = -> Pad026
  ChamferType = 0
  FlipDirection = false
  Placement = pos=(0,0,0) rot=(1,1,1;2.0944rad)
  Refine = true
  Size = 1
  Size2 = 1
  SupportTransform = false
  Suppressed = false
  UseAllEdges = false
FEATURE [PartDesign::Body] Body026  label="ESP retainer"
  AllowCompound = false
  Group = -> [Sketch148,Binder048,Binder049,Binder050,Pad026,Chamfer002]
  Origin = -> Origin026
  Tip = -> Chamfer002
